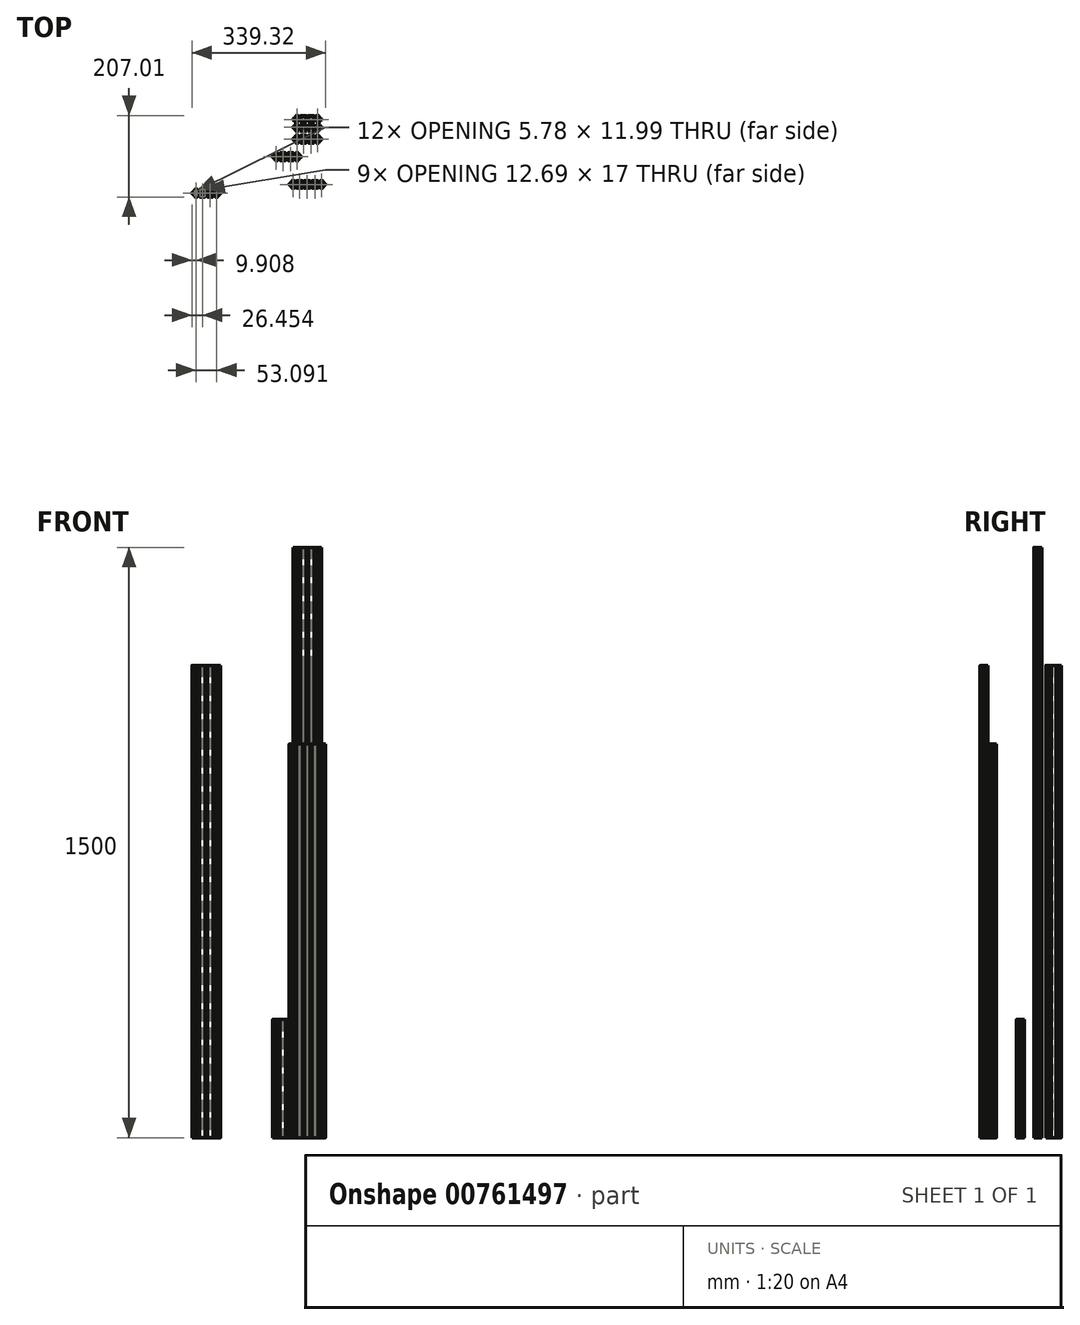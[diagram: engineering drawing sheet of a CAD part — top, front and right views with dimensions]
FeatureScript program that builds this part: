
annotation { "Feature Type Name" : "Feature", "Feature Type Description" : "" }
export const myFeature = defineFeature(function(context is Context, id is Id, definition is map)
    precondition{}
    {
        {
            var Q0;
            Q0=qCreatedBy(makeId("Top.planeOp"),FACE);
            var sketch = newSketch(context, id + "F0", { "sketchPlane" : qUnion([Q0])});
            skLineSegment(sketch, "E0", {"start": v(-3.65, 2.38) * mm, "end": v(-3.65, -2.38) * mm});
            skLineSegment(sketch, "E1", {"start": v(-17.88, 2.3) * mm, "end": v(-17.7, 2.12) * mm});
            skArc(sketch, "E2", {"start": v(-0.8, 1.94) * mm, "mid": v(-0.4, 2.06) * mm, "end": v(0, 2.1) * mm});
            skArc(sketch, "E3", {"start": v(-2.12, 2.3) * mm, "mid": v(-1.36, 2.5) * mm, "end": v(-0.8, 1.94) * mm});
            skLineSegment(sketch, "E4", {"start": v(-2.12, 2.3) * mm, "end": v(-2.3, 2.12) * mm});
            skArc(sketch, "E5", {"start": v(-1.94, 0.8) * mm, "mid": v(-2.5, 1.36) * mm, "end": v(-2.3, 2.12) * mm});
            skArc(sketch, "E6", {"start": v(-1.94, -0.8) * mm, "mid": v(-2.1, 0) * mm, "end": v(-1.94, 0.8) * mm});
            skArc(sketch, "E7", {"start": v(-2.3, -2.12) * mm, "mid": v(-2.5, -1.36) * mm, "end": v(-1.94, -0.8) * mm});
            skLineSegment(sketch, "E8", {"start": v(-2.3, -2.12) * mm, "end": v(-2.12, -2.3) * mm});
            skArc(sketch, "E9", {"start": v(-0.8, -1.94) * mm, "mid": v(-1.36, -2.5) * mm, "end": v(-2.12, -2.3) * mm});
            skArc(sketch, "E10", {"start": v(0, -2.1) * mm, "mid": v(-0.4, -2.06) * mm, "end": v(-0.8, -1.94) * mm});
            skArc(sketch, "E11", {"start": v(-17.88, 2.3) * mm, "mid": v(-18.64, 2.5) * mm, "end": v(-19.2, 1.94) * mm});
            skArc(sketch, "E12", {"start": v(-19.2, 1.94) * mm, "mid": v(-20, 2.1) * mm, "end": v(-20.8, 1.94) * mm});
            skArc(sketch, "E13", {"start": v(-20.8, 1.94) * mm, "mid": v(-21.36, 2.5) * mm, "end": v(-22.12, 2.3) * mm});
            skLineSegment(sketch, "E14", {"start": v(-22.3, 2.12) * mm, "end": v(-22.12, 2.3) * mm});
            skArc(sketch, "E15", {"start": v(-22.3, 2.12) * mm, "mid": v(-22.5, 1.36) * mm, "end": v(-21.94, 0.8) * mm});
            skArc(sketch, "E16", {"start": v(-21.94, 0.8) * mm, "mid": v(-22.1, 0) * mm, "end": v(-21.94, -0.8) * mm});
            skArc(sketch, "E17", {"start": v(-21.94, -0.8) * mm, "mid": v(-22.5, -1.36) * mm, "end": v(-22.3, -2.12) * mm});
            skLineSegment(sketch, "E18", {"start": v(-22.12, -2.3) * mm, "end": v(-22.3, -2.12) * mm});
            skArc(sketch, "E19", {"start": v(-22.12, -2.3) * mm, "mid": v(-21.36, -2.5) * mm, "end": v(-20.8, -1.94) * mm});
            skArc(sketch, "E20", {"start": v(-20.8, -1.94) * mm, "mid": v(-20, -2.1) * mm, "end": v(-19.2, -1.94) * mm});
            skArc(sketch, "E21", {"start": v(-19.2, -1.94) * mm, "mid": v(-18.64, -2.5) * mm, "end": v(-17.88, -2.3) * mm});
            skLineSegment(sketch, "E22", {"start": v(-17.7, -2.12) * mm, "end": v(-17.88, -2.3) * mm});
            skArc(sketch, "E23", {"start": v(-17.7, -2.12) * mm, "mid": v(-17.5, -1.36) * mm, "end": v(-18.06, -0.8) * mm});
            skArc(sketch, "E24", {"start": v(-18.06, -0.8) * mm, "mid": v(-17.9, 0) * mm, "end": v(-18.06, 0.8) * mm});
            skArc(sketch, "E25", {"start": v(-18.06, 0.8) * mm, "mid": v(-17.5, 1.36) * mm, "end": v(-17.7, 2.12) * mm});
            skLineSegment(sketch, "E26", {"start": v(0, -3.65) * mm, "end": v(-2.38, -3.65) * mm});
            skArc(sketch, "E27", {"start": v(-2.74, -3.8) * mm, "mid": v(-2.58, -3.7) * mm, "end": v(-2.38, -3.65) * mm});
            skLineSegment(sketch, "E28", {"start": v(-2.74, -3.8) * mm, "end": v(-5.85, -6.9) * mm});
            skArc(sketch, "E29", {"start": v(-6, -7.27) * mm, "mid": v(-5.96, -7.07) * mm, "end": v(-5.85, -6.9) * mm});
            skLineSegment(sketch, "E30", {"start": v(-6, -7.27) * mm, "end": v(-6, -8) * mm});
            skArc(sketch, "E31", {"start": v(-5.49, -8.5) * mm, "mid": v(-5.85, -8.35) * mm, "end": v(-6, -8) * mm});
            skLineSegment(sketch, "E32", {"start": v(-5.49, -8.5) * mm, "end": v(-3.14, -8.5) * mm});
            skArc(sketch, "E33", {"start": v(-3.14, -8.5) * mm, "mid": v(-2.78, -8.65) * mm, "end": v(-2.63, -9) * mm});
            skLineSegment(sketch, "E34", {"start": v(-2.63, -9.5) * mm, "end": v(-2.63, -9) * mm});
            skArc(sketch, "E35", {"start": v(-2.63, -9.5) * mm, "mid": v(-2.78, -9.85) * mm, "end": v(-3.14, -10) * mm});
            skLineSegment(sketch, "E36", {"start": v(-16.86, -10) * mm, "end": v(-3.14, -10) * mm});
            skArc(sketch, "E37", {"start": v(-17.37, -9.5) * mm, "mid": v(-17.22, -9.85) * mm, "end": v(-16.86, -10) * mm});
            skLineSegment(sketch, "E38", {"start": v(-17.37, -9.5) * mm, "end": v(-17.37, -9) * mm});
            skArc(sketch, "E39", {"start": v(-16.86, -8.5) * mm, "mid": v(-17.22, -8.65) * mm, "end": v(-17.37, -9) * mm});
            skLineSegment(sketch, "E40", {"start": v(-14.51, -8.5) * mm, "end": v(-16.86, -8.5) * mm});
            skArc(sketch, "E41", {"start": v(-14.51, -8.5) * mm, "mid": v(-14.15, -8.35) * mm, "end": v(-14, -8) * mm});
            skLineSegment(sketch, "E42", {"start": v(-14, -7.27) * mm, "end": v(-14, -8) * mm});
            skArc(sketch, "E43", {"start": v(-14, -7.27) * mm, "mid": v(-14.04, -7.07) * mm, "end": v(-14.15, -6.9) * mm});
            skLineSegment(sketch, "E44", {"start": v(-17.26, -3.8) * mm, "end": v(-14.15, -6.9) * mm});
            skArc(sketch, "E45", {"start": v(-17.26, -3.8) * mm, "mid": v(-17.42, -3.7) * mm, "end": v(-17.62, -3.65) * mm});
            skLineSegment(sketch, "E46", {"start": v(-22.38, -3.65) * mm, "end": v(-17.62, -3.65) * mm});
            skArc(sketch, "E47", {"start": v(-22.38, -3.65) * mm, "mid": v(-22.58, -3.7) * mm, "end": v(-22.74, -3.8) * mm});
            skLineSegment(sketch, "E48", {"start": v(-25.85, -6.9) * mm, "end": v(-22.74, -3.8) * mm});
            skArc(sketch, "E49", {"start": v(-25.85, -6.9) * mm, "mid": v(-25.96, -7.07) * mm, "end": v(-26, -7.27) * mm});
            skLineSegment(sketch, "E50", {"start": v(-26, -7.27) * mm, "end": v(-26, -8) * mm});
            skArc(sketch, "E51", {"start": v(-26, -8) * mm, "mid": v(-25.85, -8.35) * mm, "end": v(-25.49, -8.5) * mm});
            skLineSegment(sketch, "E52", {"start": v(-23.14, -8.5) * mm, "end": v(-25.49, -8.5) * mm});
            skArc(sketch, "E53", {"start": v(-22.63, -9) * mm, "mid": v(-22.78, -8.65) * mm, "end": v(-23.14, -8.5) * mm});
            skLineSegment(sketch, "E54", {"start": v(-22.63, -9) * mm, "end": v(-22.63, -9.5) * mm});
            skArc(sketch, "E55", {"start": v(-23.14, -10) * mm, "mid": v(-22.78, -9.85) * mm, "end": v(-22.63, -9.5) * mm});
            skLineSegment(sketch, "E56", {"start": v(-28.5, -10) * mm, "end": v(-23.14, -10) * mm});
            skArc(sketch, "E57", {"start": v(-30, -8.5) * mm, "mid": v(-29.56, -9.56) * mm, "end": v(-28.5, -10) * mm});
            skLineSegment(sketch, "E58", {"start": v(-30, -8.5) * mm, "end": v(-30, -3.14) * mm});
            skArc(sketch, "E59", {"start": v(-29.5, -2.63) * mm, "mid": v(-29.85, -2.78) * mm, "end": v(-30, -3.14) * mm});
            skLineSegment(sketch, "E60", {"start": v(-29.5, -2.63) * mm, "end": v(-29, -2.63) * mm});
            skArc(sketch, "E61", {"start": v(-28.5, -3.14) * mm, "mid": v(-28.65, -2.78) * mm, "end": v(-29, -2.63) * mm});
            skLineSegment(sketch, "E62", {"start": v(-28.5, -5.49) * mm, "end": v(-28.5, -3.14) * mm});
            skArc(sketch, "E63", {"start": v(-28.5, -5.49) * mm, "mid": v(-28.35, -5.85) * mm, "end": v(-28, -6) * mm});
            skLineSegment(sketch, "E64", {"start": v(-27.27, -6) * mm, "end": v(-28, -6) * mm});
            skArc(sketch, "E65", {"start": v(-27.27, -6) * mm, "mid": v(-27.07, -5.96) * mm, "end": v(-26.9, -5.85) * mm});
            skLineSegment(sketch, "E66", {"start": v(-23.8, -2.74) * mm, "end": v(-26.9, -5.85) * mm});
            skArc(sketch, "E67", {"start": v(-23.8, -2.74) * mm, "mid": v(-23.7, -2.58) * mm, "end": v(-23.66, -2.38) * mm});
            skLineSegment(sketch, "E68", {"start": v(-23.66, 2.38) * mm, "end": v(-23.66, -2.38) * mm});
            skArc(sketch, "E69", {"start": v(-23.66, 2.38) * mm, "mid": v(-23.7, 2.58) * mm, "end": v(-23.8, 2.74) * mm});
            skLineSegment(sketch, "E70", {"start": v(-23.8, 2.74) * mm, "end": v(-26.9, 5.85) * mm});
            skArc(sketch, "E71", {"start": v(-26.9, 5.85) * mm, "mid": v(-27.07, 5.96) * mm, "end": v(-27.27, 6) * mm});
            skLineSegment(sketch, "E72", {"start": v(-27.27, 6) * mm, "end": v(-28, 6) * mm});
            skArc(sketch, "E73", {"start": v(-28, 6) * mm, "mid": v(-28.35, 5.85) * mm, "end": v(-28.5, 5.49) * mm});
            skLineSegment(sketch, "E74", {"start": v(-28.5, 5.49) * mm, "end": v(-28.5, 3.14) * mm});
            skArc(sketch, "E75", {"start": v(-29, 2.63) * mm, "mid": v(-28.65, 2.78) * mm, "end": v(-28.5, 3.14) * mm});
            skLineSegment(sketch, "E76", {"start": v(-29, 2.63) * mm, "end": v(-29.5, 2.63) * mm});
            skArc(sketch, "E77", {"start": v(-30, 3.14) * mm, "mid": v(-29.85, 2.78) * mm, "end": v(-29.5, 2.63) * mm});
            skLineSegment(sketch, "E78", {"start": v(-30, 3.14) * mm, "end": v(-30, 8.5) * mm});
            skArc(sketch, "E79", {"start": v(-28.5, 10) * mm, "mid": v(-29.56, 9.56) * mm, "end": v(-30, 8.5) * mm});
            skLineSegment(sketch, "E80", {"start": v(-28.5, 10) * mm, "end": v(-23.14, 10) * mm});
            skArc(sketch, "E81", {"start": v(-22.63, 9.5) * mm, "mid": v(-22.78, 9.85) * mm, "end": v(-23.14, 10) * mm});
            skLineSegment(sketch, "E82", {"start": v(-22.63, 9.5) * mm, "end": v(-22.63, 9) * mm});
            skArc(sketch, "E83", {"start": v(-23.14, 8.5) * mm, "mid": v(-22.78, 8.65) * mm, "end": v(-22.63, 9) * mm});
            skLineSegment(sketch, "E84", {"start": v(-23.14, 8.5) * mm, "end": v(-25.49, 8.5) * mm});
            skArc(sketch, "E85", {"start": v(-25.49, 8.5) * mm, "mid": v(-25.85, 8.35) * mm, "end": v(-26, 8) * mm});
            skLineSegment(sketch, "E86", {"start": v(-26, 8) * mm, "end": v(-26, 7.27) * mm});
            skArc(sketch, "E87", {"start": v(-26, 7.27) * mm, "mid": v(-25.96, 7.07) * mm, "end": v(-25.85, 6.9) * mm});
            skLineSegment(sketch, "E88", {"start": v(-25.85, 6.9) * mm, "end": v(-22.74, 3.8) * mm});
            skArc(sketch, "E89", {"start": v(-22.74, 3.8) * mm, "mid": v(-22.58, 3.7) * mm, "end": v(-22.38, 3.65) * mm});
            skLineSegment(sketch, "E90", {"start": v(-22.38, 3.65) * mm, "end": v(-17.62, 3.65) * mm});
            skArc(sketch, "E91", {"start": v(-17.62, 3.65) * mm, "mid": v(-17.42, 3.7) * mm, "end": v(-17.26, 3.8) * mm});
            skLineSegment(sketch, "E92", {"start": v(-17.26, 3.8) * mm, "end": v(-14.15, 6.9) * mm});
            skArc(sketch, "E93", {"start": v(-14.15, 6.9) * mm, "mid": v(-14.04, 7.07) * mm, "end": v(-14, 7.27) * mm});
            skLineSegment(sketch, "E94", {"start": v(-14, 8) * mm, "end": v(-14, 7.27) * mm});
            skArc(sketch, "E95", {"start": v(-14, 8) * mm, "mid": v(-14.15, 8.35) * mm, "end": v(-14.51, 8.5) * mm});
            skLineSegment(sketch, "E96", {"start": v(-14.51, 8.5) * mm, "end": v(-16.86, 8.5) * mm});
            skArc(sketch, "E97", {"start": v(-17.37, 9) * mm, "mid": v(-17.22, 8.65) * mm, "end": v(-16.86, 8.5) * mm});
            skLineSegment(sketch, "E98", {"start": v(-17.37, 9) * mm, "end": v(-17.37, 9.5) * mm});
            skArc(sketch, "E99", {"start": v(-16.86, 10) * mm, "mid": v(-17.22, 9.85) * mm, "end": v(-17.37, 9.5) * mm});
            skLineSegment(sketch, "E100", {"start": v(-3.14, 10) * mm, "end": v(-16.86, 10) * mm});
            skArc(sketch, "E101", {"start": v(-3.14, 10) * mm, "mid": v(-2.78, 9.85) * mm, "end": v(-2.63, 9.5) * mm});
            skLineSegment(sketch, "E102", {"start": v(-2.63, 9) * mm, "end": v(-2.63, 9.5) * mm});
            skArc(sketch, "E103", {"start": v(-2.63, 9) * mm, "mid": v(-2.78, 8.65) * mm, "end": v(-3.14, 8.5) * mm});
            skLineSegment(sketch, "E104", {"start": v(-5.49, 8.5) * mm, "end": v(-3.14, 8.5) * mm});
            skArc(sketch, "E105", {"start": v(-6, 8) * mm, "mid": v(-5.85, 8.35) * mm, "end": v(-5.49, 8.5) * mm});
            skLineSegment(sketch, "E106", {"start": v(-6, 8) * mm, "end": v(-6, 7.27) * mm});
            skArc(sketch, "E107", {"start": v(-5.85, 6.9) * mm, "mid": v(-5.96, 7.07) * mm, "end": v(-6, 7.27) * mm});
            skLineSegment(sketch, "E108", {"start": v(-2.74, 3.8) * mm, "end": v(-5.85, 6.9) * mm});
            skArc(sketch, "E109", {"start": v(-2.38, 3.65) * mm, "mid": v(-2.58, 3.7) * mm, "end": v(-2.74, 3.8) * mm});
            skLineSegment(sketch, "E110", {"start": v(0, 3.65) * mm, "end": v(-2.38, 3.65) * mm});
            skArc(sketch, "E111", {"start": v(-3.65, 2.38) * mm, "mid": v(-3.7, 2.58) * mm, "end": v(-3.8, 2.74) * mm});
            skLineSegment(sketch, "E112", {"start": v(-3.8, 2.74) * mm, "end": v(-7.35, 6.29) * mm});
            skArc(sketch, "E113", {"start": v(-7.35, 6.29) * mm, "mid": v(-7.46, 6.45) * mm, "end": v(-7.5, 6.64) * mm});
            skLineSegment(sketch, "E114", {"start": v(-7.5, 8) * mm, "end": v(-7.5, 6.64) * mm});
            skArc(sketch, "E115", {"start": v(-8, 8.5) * mm, "mid": v(-7.64, 8.35) * mm, "end": v(-7.5, 8) * mm});
            skLineSegment(sketch, "E116", {"start": v(-12, 8.5) * mm, "end": v(-8, 8.5) * mm});
            skArc(sketch, "E117", {"start": v(-12, 8.5) * mm, "mid": v(-12.36, 8.35) * mm, "end": v(-12.5, 8) * mm});
            skLineSegment(sketch, "E118", {"start": v(-12.5, 8) * mm, "end": v(-12.5, 6.64) * mm});
            skArc(sketch, "E119", {"start": v(-12.65, 6.29) * mm, "mid": v(-12.54, 6.45) * mm, "end": v(-12.5, 6.64) * mm});
            skLineSegment(sketch, "E120", {"start": v(-16.2, 2.74) * mm, "end": v(-12.65, 6.29) * mm});
            skArc(sketch, "E121", {"start": v(-16.2, 2.74) * mm, "mid": v(-16.3, 2.58) * mm, "end": v(-16.35, 2.38) * mm});
            skLineSegment(sketch, "E122", {"start": v(-16.35, 2.38) * mm, "end": v(-16.35, -2.38) * mm});
            skArc(sketch, "E123", {"start": v(-16.35, -2.38) * mm, "mid": v(-16.3, -2.58) * mm, "end": v(-16.2, -2.74) * mm});
            skLineSegment(sketch, "E124", {"start": v(-16.2, -2.74) * mm, "end": v(-12.65, -6.29) * mm});
            skArc(sketch, "E125", {"start": v(-12.5, -6.64) * mm, "mid": v(-12.54, -6.45) * mm, "end": v(-12.65, -6.29) * mm});
            skLineSegment(sketch, "E126", {"start": v(-12.5, -6.64) * mm, "end": v(-12.5, -8) * mm});
            skArc(sketch, "E127", {"start": v(-12.5, -8) * mm, "mid": v(-12.36, -8.35) * mm, "end": v(-12, -8.5) * mm});
            skLineSegment(sketch, "E128", {"start": v(-12, -8.5) * mm, "end": v(-8, -8.5) * mm});
            skArc(sketch, "E129", {"start": v(-7.5, -8) * mm, "mid": v(-7.64, -8.35) * mm, "end": v(-8, -8.5) * mm});
            skLineSegment(sketch, "E130", {"start": v(-7.5, -6.64) * mm, "end": v(-7.5, -8) * mm});
            skArc(sketch, "E131", {"start": v(-7.5, -6.64) * mm, "mid": v(-7.46, -6.45) * mm, "end": v(-7.35, -6.29) * mm});
            skLineSegment(sketch, "E132", {"start": v(-3.8, -2.74) * mm, "end": v(-7.35, -6.29) * mm});
            skArc(sketch, "E133", {"start": v(-3.65, -2.38) * mm, "mid": v(-3.7, -2.58) * mm, "end": v(-3.8, -2.74) * mm});
            skLineSegment(sketch, "E134", {"start": v(3.65, 2.38) * mm, "end": v(3.65, -2.38) * mm});
            skLineSegment(sketch, "E135", {"start": v(17.88, 2.3) * mm, "end": v(17.7, 2.12) * mm});
            skArc(sketch, "E136", {"start": v(0.8, 1.94) * mm, "mid": v(1.36, 2.5) * mm, "end": v(2.12, 2.3) * mm});
            skLineSegment(sketch, "E137", {"start": v(2.12, 2.3) * mm, "end": v(2.3, 2.12) * mm});
            skArc(sketch, "E138", {"start": v(2.3, 2.12) * mm, "mid": v(2.5, 1.36) * mm, "end": v(1.94, 0.8) * mm});
            skArc(sketch, "E139", {"start": v(1.94, 0.8) * mm, "mid": v(2.1, 0) * mm, "end": v(1.94, -0.8) * mm});
            skArc(sketch, "E140", {"start": v(1.94, -0.8) * mm, "mid": v(2.5, -1.36) * mm, "end": v(2.3, -2.12) * mm});
            skLineSegment(sketch, "E141", {"start": v(2.3, -2.12) * mm, "end": v(2.12, -2.3) * mm});
            skArc(sketch, "E142", {"start": v(2.12, -2.3) * mm, "mid": v(1.36, -2.5) * mm, "end": v(0.8, -1.94) * mm});
            skArc(sketch, "E143", {"start": v(19.2, 1.94) * mm, "mid": v(18.64, 2.5) * mm, "end": v(17.88, 2.3) * mm});
            skArc(sketch, "E144", {"start": v(20.8, 1.94) * mm, "mid": v(20, 2.1) * mm, "end": v(19.2, 1.94) * mm});
            skArc(sketch, "E145", {"start": v(22.12, 2.3) * mm, "mid": v(21.36, 2.5) * mm, "end": v(20.8, 1.94) * mm});
            skLineSegment(sketch, "E146", {"start": v(22.3, 2.12) * mm, "end": v(22.12, 2.3) * mm});
            skArc(sketch, "E147", {"start": v(21.94, 0.8) * mm, "mid": v(22.5, 1.36) * mm, "end": v(22.3, 2.12) * mm});
            skArc(sketch, "E148", {"start": v(21.94, -0.8) * mm, "mid": v(22.1, 0) * mm, "end": v(21.94, 0.8) * mm});
            skArc(sketch, "E149", {"start": v(22.3, -2.12) * mm, "mid": v(22.5, -1.36) * mm, "end": v(21.94, -0.8) * mm});
            skLineSegment(sketch, "E150", {"start": v(22.12, -2.3) * mm, "end": v(22.3, -2.12) * mm});
            skArc(sketch, "E151", {"start": v(20.8, -1.94) * mm, "mid": v(21.36, -2.5) * mm, "end": v(22.12, -2.3) * mm});
            skArc(sketch, "E152", {"start": v(19.2, -1.94) * mm, "mid": v(20, -2.1) * mm, "end": v(20.8, -1.94) * mm});
            skArc(sketch, "E153", {"start": v(17.88, -2.3) * mm, "mid": v(18.64, -2.5) * mm, "end": v(19.2, -1.94) * mm});
            skLineSegment(sketch, "E154", {"start": v(17.7, -2.12) * mm, "end": v(17.88, -2.3) * mm});
            skArc(sketch, "E155", {"start": v(18.06, -0.8) * mm, "mid": v(17.5, -1.36) * mm, "end": v(17.7, -2.12) * mm});
            skArc(sketch, "E156", {"start": v(18.06, 0.8) * mm, "mid": v(17.9, 0) * mm, "end": v(18.06, -0.8) * mm});
            skArc(sketch, "E157", {"start": v(17.7, 2.12) * mm, "mid": v(17.5, 1.36) * mm, "end": v(18.06, 0.8) * mm});
            skLineSegment(sketch, "E158", {"start": v(0, -3.65) * mm, "end": v(2.38, -3.65) * mm});
            skArc(sketch, "E159", {"start": v(2.38, -3.65) * mm, "mid": v(2.58, -3.7) * mm, "end": v(2.74, -3.8) * mm});
            skLineSegment(sketch, "E160", {"start": v(2.74, -3.8) * mm, "end": v(5.85, -6.9) * mm});
            skArc(sketch, "E161", {"start": v(5.85, -6.9) * mm, "mid": v(5.96, -7.07) * mm, "end": v(6, -7.27) * mm});
            skLineSegment(sketch, "E162", {"start": v(6, -7.27) * mm, "end": v(6, -8) * mm});
            skArc(sketch, "E163", {"start": v(6, -8) * mm, "mid": v(5.85, -8.35) * mm, "end": v(5.49, -8.5) * mm});
            skLineSegment(sketch, "E164", {"start": v(5.49, -8.5) * mm, "end": v(3.14, -8.5) * mm});
            skArc(sketch, "E165", {"start": v(2.63, -9) * mm, "mid": v(2.78, -8.65) * mm, "end": v(3.14, -8.5) * mm});
            skLineSegment(sketch, "E166", {"start": v(2.63, -9.5) * mm, "end": v(2.63, -9) * mm});
            skArc(sketch, "E167", {"start": v(3.14, -10) * mm, "mid": v(2.78, -9.85) * mm, "end": v(2.63, -9.5) * mm});
            skLineSegment(sketch, "E168", {"start": v(16.86, -10) * mm, "end": v(3.14, -10) * mm});
            skArc(sketch, "E169", {"start": v(16.86, -10) * mm, "mid": v(17.22, -9.85) * mm, "end": v(17.37, -9.5) * mm});
            skLineSegment(sketch, "E170", {"start": v(17.37, -9.5) * mm, "end": v(17.37, -9) * mm});
            skArc(sketch, "E171", {"start": v(17.37, -9) * mm, "mid": v(17.22, -8.65) * mm, "end": v(16.86, -8.5) * mm});
            skLineSegment(sketch, "E172", {"start": v(14.51, -8.5) * mm, "end": v(16.86, -8.5) * mm});
            skArc(sketch, "E173", {"start": v(14, -8) * mm, "mid": v(14.15, -8.35) * mm, "end": v(14.51, -8.5) * mm});
            skLineSegment(sketch, "E174", {"start": v(14, -7.27) * mm, "end": v(14, -8) * mm});
            skArc(sketch, "E175", {"start": v(14.15, -6.9) * mm, "mid": v(14.04, -7.07) * mm, "end": v(14, -7.27) * mm});
            skLineSegment(sketch, "E176", {"start": v(17.26, -3.8) * mm, "end": v(14.15, -6.9) * mm});
            skArc(sketch, "E177", {"start": v(17.62, -3.65) * mm, "mid": v(17.42, -3.7) * mm, "end": v(17.26, -3.8) * mm});
            skLineSegment(sketch, "E178", {"start": v(22.38, -3.65) * mm, "end": v(17.62, -3.65) * mm});
            skArc(sketch, "E179", {"start": v(22.74, -3.8) * mm, "mid": v(22.58, -3.7) * mm, "end": v(22.38, -3.65) * mm});
            skLineSegment(sketch, "E180", {"start": v(25.85, -6.9) * mm, "end": v(22.74, -3.8) * mm});
            skArc(sketch, "E181", {"start": v(26, -7.27) * mm, "mid": v(25.96, -7.07) * mm, "end": v(25.85, -6.9) * mm});
            skLineSegment(sketch, "E182", {"start": v(26, -7.27) * mm, "end": v(26, -8) * mm});
            skArc(sketch, "E183", {"start": v(25.49, -8.5) * mm, "mid": v(25.85, -8.35) * mm, "end": v(26, -8) * mm});
            skLineSegment(sketch, "E184", {"start": v(23.14, -8.5) * mm, "end": v(25.49, -8.5) * mm});
            skArc(sketch, "E185", {"start": v(23.14, -8.5) * mm, "mid": v(22.78, -8.65) * mm, "end": v(22.63, -9) * mm});
            skLineSegment(sketch, "E186", {"start": v(22.63, -9) * mm, "end": v(22.63, -9.5) * mm});
            skArc(sketch, "E187", {"start": v(22.63, -9.5) * mm, "mid": v(22.78, -9.85) * mm, "end": v(23.14, -10) * mm});
            skLineSegment(sketch, "E188", {"start": v(28.5, -10) * mm, "end": v(23.14, -10) * mm});
            skArc(sketch, "E189", {"start": v(28.5, -10) * mm, "mid": v(29.56, -9.56) * mm, "end": v(30, -8.5) * mm});
            skLineSegment(sketch, "E190", {"start": v(30, -8.5) * mm, "end": v(30, -3.14) * mm});
            skArc(sketch, "E191", {"start": v(30, -3.14) * mm, "mid": v(29.85, -2.78) * mm, "end": v(29.5, -2.63) * mm});
            skLineSegment(sketch, "E192", {"start": v(29.5, -2.63) * mm, "end": v(29, -2.63) * mm});
            skArc(sketch, "E193", {"start": v(29, -2.63) * mm, "mid": v(28.65, -2.78) * mm, "end": v(28.5, -3.14) * mm});
            skLineSegment(sketch, "E194", {"start": v(28.5, -5.49) * mm, "end": v(28.5, -3.14) * mm});
            skArc(sketch, "E195", {"start": v(28, -6) * mm, "mid": v(28.35, -5.85) * mm, "end": v(28.5, -5.49) * mm});
            skLineSegment(sketch, "E196", {"start": v(27.27, -6) * mm, "end": v(28, -6) * mm});
            skArc(sketch, "E197", {"start": v(26.9, -5.85) * mm, "mid": v(27.07, -5.96) * mm, "end": v(27.27, -6) * mm});
            skLineSegment(sketch, "E198", {"start": v(23.8, -2.74) * mm, "end": v(26.9, -5.85) * mm});
            skArc(sketch, "E199", {"start": v(23.66, -2.38) * mm, "mid": v(23.7, -2.58) * mm, "end": v(23.8, -2.74) * mm});
            skLineSegment(sketch, "E200", {"start": v(23.66, 2.38) * mm, "end": v(23.66, -2.38) * mm});
            skArc(sketch, "E201", {"start": v(23.8, 2.74) * mm, "mid": v(23.7, 2.58) * mm, "end": v(23.66, 2.38) * mm});
            skLineSegment(sketch, "E202", {"start": v(23.8, 2.74) * mm, "end": v(26.9, 5.85) * mm});
            skArc(sketch, "E203", {"start": v(27.27, 6) * mm, "mid": v(27.07, 5.96) * mm, "end": v(26.9, 5.85) * mm});
            skLineSegment(sketch, "E204", {"start": v(27.27, 6) * mm, "end": v(28, 6) * mm});
            skArc(sketch, "E205", {"start": v(28.5, 5.49) * mm, "mid": v(28.35, 5.85) * mm, "end": v(28, 6) * mm});
            skLineSegment(sketch, "E206", {"start": v(28.5, 5.49) * mm, "end": v(28.5, 3.14) * mm});
            skArc(sketch, "E207", {"start": v(28.5, 3.14) * mm, "mid": v(28.65, 2.78) * mm, "end": v(29, 2.63) * mm});
            skLineSegment(sketch, "E208", {"start": v(29, 2.63) * mm, "end": v(29.5, 2.63) * mm});
            skArc(sketch, "E209", {"start": v(29.5, 2.63) * mm, "mid": v(29.85, 2.78) * mm, "end": v(30, 3.14) * mm});
            skLineSegment(sketch, "E210", {"start": v(30, 3.14) * mm, "end": v(30, 8.5) * mm});
            skArc(sketch, "E211", {"start": v(30, 8.5) * mm, "mid": v(29.56, 9.56) * mm, "end": v(28.5, 10) * mm});
            skLineSegment(sketch, "E212", {"start": v(28.5, 10) * mm, "end": v(23.14, 10) * mm});
            skArc(sketch, "E213", {"start": v(23.14, 10) * mm, "mid": v(22.78, 9.85) * mm, "end": v(22.63, 9.5) * mm});
            skLineSegment(sketch, "E214", {"start": v(22.63, 9.5) * mm, "end": v(22.63, 9) * mm});
            skArc(sketch, "E215", {"start": v(22.63, 9) * mm, "mid": v(22.78, 8.65) * mm, "end": v(23.14, 8.5) * mm});
            skLineSegment(sketch, "E216", {"start": v(23.14, 8.5) * mm, "end": v(25.49, 8.5) * mm});
            skArc(sketch, "E217", {"start": v(26, 8) * mm, "mid": v(25.85, 8.35) * mm, "end": v(25.49, 8.5) * mm});
            skLineSegment(sketch, "E218", {"start": v(26, 8) * mm, "end": v(26, 7.27) * mm});
            skArc(sketch, "E219", {"start": v(25.85, 6.9) * mm, "mid": v(25.96, 7.07) * mm, "end": v(26, 7.27) * mm});
            skLineSegment(sketch, "E220", {"start": v(25.85, 6.9) * mm, "end": v(22.74, 3.8) * mm});
            skArc(sketch, "E221", {"start": v(22.38, 3.65) * mm, "mid": v(22.58, 3.7) * mm, "end": v(22.74, 3.8) * mm});
            skLineSegment(sketch, "E222", {"start": v(22.38, 3.65) * mm, "end": v(17.62, 3.65) * mm});
            skArc(sketch, "E223", {"start": v(17.26, 3.8) * mm, "mid": v(17.42, 3.7) * mm, "end": v(17.62, 3.65) * mm});
            skLineSegment(sketch, "E224", {"start": v(17.26, 3.8) * mm, "end": v(14.15, 6.9) * mm});
            skArc(sketch, "E225", {"start": v(14, 7.27) * mm, "mid": v(14.04, 7.07) * mm, "end": v(14.15, 6.9) * mm});
            skLineSegment(sketch, "E226", {"start": v(14, 8) * mm, "end": v(14, 7.27) * mm});
            skArc(sketch, "E227", {"start": v(14.51, 8.5) * mm, "mid": v(14.15, 8.35) * mm, "end": v(14, 8) * mm});
            skLineSegment(sketch, "E228", {"start": v(14.51, 8.5) * mm, "end": v(16.86, 8.5) * mm});
            skArc(sketch, "E229", {"start": v(16.86, 8.5) * mm, "mid": v(17.22, 8.65) * mm, "end": v(17.37, 9) * mm});
            skLineSegment(sketch, "E230", {"start": v(17.37, 9) * mm, "end": v(17.37, 9.5) * mm});
            skArc(sketch, "E231", {"start": v(17.37, 9.5) * mm, "mid": v(17.22, 9.85) * mm, "end": v(16.86, 10) * mm});
            skLineSegment(sketch, "E232", {"start": v(3.14, 10) * mm, "end": v(16.86, 10) * mm});
            skArc(sketch, "E233", {"start": v(2.63, 9.5) * mm, "mid": v(2.78, 9.85) * mm, "end": v(3.14, 10) * mm});
            skLineSegment(sketch, "E234", {"start": v(2.63, 9) * mm, "end": v(2.63, 9.5) * mm});
            skArc(sketch, "E235", {"start": v(3.14, 8.5) * mm, "mid": v(2.78, 8.65) * mm, "end": v(2.63, 9) * mm});
            skLineSegment(sketch, "E236", {"start": v(5.49, 8.5) * mm, "end": v(3.14, 8.5) * mm});
            skArc(sketch, "E237", {"start": v(5.49, 8.5) * mm, "mid": v(5.85, 8.35) * mm, "end": v(6, 8) * mm});
            skLineSegment(sketch, "E238", {"start": v(6, 8) * mm, "end": v(6, 7.27) * mm});
            skArc(sketch, "E239", {"start": v(6, 7.27) * mm, "mid": v(5.96, 7.07) * mm, "end": v(5.85, 6.9) * mm});
            skLineSegment(sketch, "E240", {"start": v(2.74, 3.8) * mm, "end": v(5.85, 6.9) * mm});
            skArc(sketch, "E241", {"start": v(2.74, 3.8) * mm, "mid": v(2.58, 3.7) * mm, "end": v(2.38, 3.65) * mm});
            skLineSegment(sketch, "E242", {"start": v(0, 3.65) * mm, "end": v(2.38, 3.65) * mm});
            skArc(sketch, "E243", {"start": v(3.8, 2.74) * mm, "mid": v(3.7, 2.58) * mm, "end": v(3.65, 2.38) * mm});
            skLineSegment(sketch, "E244", {"start": v(3.8, 2.74) * mm, "end": v(7.35, 6.29) * mm});
            skArc(sketch, "E245", {"start": v(7.5, 6.64) * mm, "mid": v(7.46, 6.45) * mm, "end": v(7.35, 6.29) * mm});
            skLineSegment(sketch, "E246", {"start": v(7.5, 8) * mm, "end": v(7.5, 6.64) * mm});
            skArc(sketch, "E247", {"start": v(7.5, 8) * mm, "mid": v(7.64, 8.35) * mm, "end": v(8, 8.5) * mm});
            skLineSegment(sketch, "E248", {"start": v(12, 8.5) * mm, "end": v(8, 8.5) * mm});
            skArc(sketch, "E249", {"start": v(12.5, 8) * mm, "mid": v(12.36, 8.35) * mm, "end": v(12, 8.5) * mm});
            skLineSegment(sketch, "E250", {"start": v(12.5, 8) * mm, "end": v(12.5, 6.64) * mm});
            skArc(sketch, "E251", {"start": v(12.5, 6.64) * mm, "mid": v(12.54, 6.45) * mm, "end": v(12.65, 6.29) * mm});
            skLineSegment(sketch, "E252", {"start": v(16.2, 2.74) * mm, "end": v(12.65, 6.29) * mm});
            skArc(sketch, "E253", {"start": v(16.35, 2.38) * mm, "mid": v(16.3, 2.58) * mm, "end": v(16.2, 2.74) * mm});
            skLineSegment(sketch, "E254", {"start": v(16.35, 2.38) * mm, "end": v(16.35, -2.38) * mm});
            skArc(sketch, "E255", {"start": v(16.2, -2.74) * mm, "mid": v(16.3, -2.58) * mm, "end": v(16.35, -2.38) * mm});
            skLineSegment(sketch, "E256", {"start": v(16.2, -2.74) * mm, "end": v(12.65, -6.29) * mm});
            skArc(sketch, "E257", {"start": v(12.65, -6.29) * mm, "mid": v(12.54, -6.45) * mm, "end": v(12.5, -6.64) * mm});
            skLineSegment(sketch, "E258", {"start": v(12.5, -6.64) * mm, "end": v(12.5, -8) * mm});
            skArc(sketch, "E259", {"start": v(12, -8.5) * mm, "mid": v(12.36, -8.35) * mm, "end": v(12.5, -8) * mm});
            skLineSegment(sketch, "E260", {"start": v(12, -8.5) * mm, "end": v(8, -8.5) * mm});
            skArc(sketch, "E261", {"start": v(8, -8.5) * mm, "mid": v(7.64, -8.35) * mm, "end": v(7.5, -8) * mm});
            skLineSegment(sketch, "E262", {"start": v(7.5, -6.64) * mm, "end": v(7.5, -8) * mm});
            skArc(sketch, "E263", {"start": v(7.35, -6.29) * mm, "mid": v(7.46, -6.45) * mm, "end": v(7.5, -6.64) * mm});
            skLineSegment(sketch, "E264", {"start": v(3.8, -2.74) * mm, "end": v(7.35, -6.29) * mm});
            skArc(sketch, "E265", {"start": v(3.8, -2.74) * mm, "mid": v(3.7, -2.58) * mm, "end": v(3.65, -2.38) * mm});
            skArc(sketch, "E266", {"start": v(0, 2.1) * mm, "mid": v(0.4, 2.06) * mm, "end": v(0.8, 1.94) * mm});
            skArc(sketch, "E267", {"start": v(0.8, -1.94) * mm, "mid": v(0.4, -2.06) * mm, "end": v(0, -2.1) * mm});
            skCircle(sketch, "E268", {"center": v(-32.45, 0) * mm, "radius": 4 * mm});
            skCircle(sketch, "E269", {"center": v(32.45, 0) * mm, "radius": 4 * mm});
            skSolve(sketch);
        }
        {
            var Q0;
            Q0=qCreatedBy(makeId("Top.planeOp"),FACE);
            var sketch = newSketch(context, id + "F1", { "sketchPlane" : qUnion([Q0])});
            skLineSegment(sketch, "E270", {"start": v(-3.65, 52.38) * mm, "end": v(-3.65, 47.62) * mm});
            skLineSegment(sketch, "E271", {"start": v(-17.88, 52.3) * mm, "end": v(-17.7, 52.12) * mm});
            skArc(sketch, "E272", {"start": v(-0.8, 51.94) * mm, "mid": v(-0.4, 52.06) * mm, "end": v(0, 52.1) * mm});
            skArc(sketch, "E273", {"start": v(-2.12, 52.3) * mm, "mid": v(-1.36, 52.5) * mm, "end": v(-0.8, 51.94) * mm});
            skLineSegment(sketch, "E274", {"start": v(-2.12, 52.3) * mm, "end": v(-2.3, 52.12) * mm});
            skArc(sketch, "E275", {"start": v(-1.94, 50.8) * mm, "mid": v(-2.5, 51.36) * mm, "end": v(-2.3, 52.12) * mm});
            skArc(sketch, "E276", {"start": v(-1.94, 49.2) * mm, "mid": v(-2.1, 50) * mm, "end": v(-1.94, 50.8) * mm});
            skArc(sketch, "E277", {"start": v(-2.3, 47.88) * mm, "mid": v(-2.5, 48.64) * mm, "end": v(-1.94, 49.2) * mm});
            skLineSegment(sketch, "E278", {"start": v(-2.3, 47.88) * mm, "end": v(-2.12, 47.7) * mm});
            skArc(sketch, "E279", {"start": v(-0.8, 48.06) * mm, "mid": v(-1.36, 47.5) * mm, "end": v(-2.12, 47.7) * mm});
            skArc(sketch, "E280", {"start": v(0, 47.9) * mm, "mid": v(-0.4, 47.94) * mm, "end": v(-0.8, 48.06) * mm});
            skArc(sketch, "E281", {"start": v(-17.88, 52.3) * mm, "mid": v(-18.64, 52.5) * mm, "end": v(-19.2, 51.94) * mm});
            skArc(sketch, "E282", {"start": v(-19.2, 51.94) * mm, "mid": v(-20, 52.1) * mm, "end": v(-20.8, 51.94) * mm});
            skArc(sketch, "E283", {"start": v(-20.8, 51.94) * mm, "mid": v(-21.36, 52.5) * mm, "end": v(-22.12, 52.3) * mm});
            skLineSegment(sketch, "E284", {"start": v(-22.3, 52.12) * mm, "end": v(-22.12, 52.3) * mm});
            skArc(sketch, "E285", {"start": v(-22.3, 52.12) * mm, "mid": v(-22.5, 51.36) * mm, "end": v(-21.94, 50.8) * mm});
            skArc(sketch, "E286", {"start": v(-21.94, 50.8) * mm, "mid": v(-22.1, 50) * mm, "end": v(-21.94, 49.2) * mm});
            skArc(sketch, "E287", {"start": v(-21.94, 49.2) * mm, "mid": v(-22.5, 48.64) * mm, "end": v(-22.3, 47.88) * mm});
            skLineSegment(sketch, "E288", {"start": v(-22.12, 47.7) * mm, "end": v(-22.3, 47.88) * mm});
            skArc(sketch, "E289", {"start": v(-22.12, 47.7) * mm, "mid": v(-21.36, 47.5) * mm, "end": v(-20.8, 48.06) * mm});
            skArc(sketch, "E290", {"start": v(-20.8, 48.06) * mm, "mid": v(-20, 47.9) * mm, "end": v(-19.2, 48.06) * mm});
            skArc(sketch, "E291", {"start": v(-19.2, 48.06) * mm, "mid": v(-18.64, 47.5) * mm, "end": v(-17.88, 47.7) * mm});
            skLineSegment(sketch, "E292", {"start": v(-17.7, 47.88) * mm, "end": v(-17.88, 47.7) * mm});
            skArc(sketch, "E293", {"start": v(-17.7, 47.88) * mm, "mid": v(-17.5, 48.64) * mm, "end": v(-18.06, 49.2) * mm});
            skArc(sketch, "E294", {"start": v(-18.06, 49.2) * mm, "mid": v(-17.9, 50) * mm, "end": v(-18.06, 50.8) * mm});
            skArc(sketch, "E295", {"start": v(-18.06, 50.8) * mm, "mid": v(-17.5, 51.36) * mm, "end": v(-17.7, 52.12) * mm});
            skLineSegment(sketch, "E296", {"start": v(0, 46.35) * mm, "end": v(-2.38, 46.35) * mm});
            skArc(sketch, "E297", {"start": v(-2.74, 46.2) * mm, "mid": v(-2.58, 46.3) * mm, "end": v(-2.38, 46.35) * mm});
            skLineSegment(sketch, "E298", {"start": v(-2.74, 46.2) * mm, "end": v(-5.85, 43.1) * mm});
            skLineSegment(sketch, "E299", {"start": v(-17.26, 46.2) * mm, "end": v(-14.15, 43.1) * mm});
            skArc(sketch, "E300", {"start": v(-17.26, 46.2) * mm, "mid": v(-17.42, 46.3) * mm, "end": v(-17.62, 46.35) * mm});
            skLineSegment(sketch, "E301", {"start": v(-22.38, 46.35) * mm, "end": v(-17.62, 46.35) * mm});
            skArc(sketch, "E302", {"start": v(-22.38, 46.35) * mm, "mid": v(-22.58, 46.3) * mm, "end": v(-22.74, 46.2) * mm});
            skLineSegment(sketch, "E303", {"start": v(-25.85, 43.1) * mm, "end": v(-22.74, 46.2) * mm});
            skLineSegment(sketch, "E304", {"start": v(-30, 38.5) * mm, "end": v(-30, 46.86) * mm});
            skArc(sketch, "E305", {"start": v(-29.5, 47.37) * mm, "mid": v(-29.85, 47.22) * mm, "end": v(-30, 46.86) * mm});
            skLineSegment(sketch, "E306", {"start": v(-29.5, 47.37) * mm, "end": v(-29, 47.37) * mm});
            skArc(sketch, "E307", {"start": v(-28.5, 46.86) * mm, "mid": v(-28.65, 47.22) * mm, "end": v(-29, 47.37) * mm});
            skLineSegment(sketch, "E308", {"start": v(-28.5, 44.51) * mm, "end": v(-28.5, 46.86) * mm});
            skArc(sketch, "E309", {"start": v(-28.5, 44.51) * mm, "mid": v(-28.35, 44.15) * mm, "end": v(-28, 44) * mm});
            skLineSegment(sketch, "E310", {"start": v(-27.27, 44) * mm, "end": v(-28, 44) * mm});
            skArc(sketch, "E311", {"start": v(-27.27, 44) * mm, "mid": v(-27.07, 44.04) * mm, "end": v(-26.9, 44.15) * mm});
            skLineSegment(sketch, "E312", {"start": v(-23.8, 47.26) * mm, "end": v(-26.9, 44.15) * mm});
            skArc(sketch, "E313", {"start": v(-23.8, 47.26) * mm, "mid": v(-23.7, 47.42) * mm, "end": v(-23.65, 47.62) * mm});
            skLineSegment(sketch, "E314", {"start": v(-23.65, 52.38) * mm, "end": v(-23.65, 47.62) * mm});
            skArc(sketch, "E315", {"start": v(-23.65, 52.38) * mm, "mid": v(-23.7, 52.58) * mm, "end": v(-23.8, 52.74) * mm});
            skLineSegment(sketch, "E316", {"start": v(-23.8, 52.74) * mm, "end": v(-26.9, 55.85) * mm});
            skArc(sketch, "E317", {"start": v(-26.9, 55.85) * mm, "mid": v(-27.07, 55.96) * mm, "end": v(-27.27, 56) * mm});
            skLineSegment(sketch, "E318", {"start": v(-27.27, 56) * mm, "end": v(-28, 56) * mm});
            skArc(sketch, "E319", {"start": v(-28, 56) * mm, "mid": v(-28.35, 55.85) * mm, "end": v(-28.5, 55.49) * mm});
            skLineSegment(sketch, "E320", {"start": v(-28.5, 55.49) * mm, "end": v(-28.5, 53.14) * mm});
            skArc(sketch, "E321", {"start": v(-29, 52.63) * mm, "mid": v(-28.65, 52.78) * mm, "end": v(-28.5, 53.14) * mm});
            skLineSegment(sketch, "E322", {"start": v(-29, 52.63) * mm, "end": v(-29.5, 52.63) * mm});
            skArc(sketch, "E323", {"start": v(-30, 53.14) * mm, "mid": v(-29.85, 52.78) * mm, "end": v(-29.5, 52.63) * mm});
            skLineSegment(sketch, "E324", {"start": v(-30, 53.14) * mm, "end": v(-30, 58.5) * mm});
            skArc(sketch, "E325", {"start": v(-28.5, 60) * mm, "mid": v(-29.56, 59.56) * mm, "end": v(-30, 58.5) * mm});
            skLineSegment(sketch, "E326", {"start": v(-28.5, 60) * mm, "end": v(-23.14, 60) * mm});
            skArc(sketch, "E327", {"start": v(-22.63, 59.5) * mm, "mid": v(-22.78, 59.85) * mm, "end": v(-23.14, 60) * mm});
            skLineSegment(sketch, "E328", {"start": v(-22.63, 59.5) * mm, "end": v(-22.63, 59) * mm});
            skArc(sketch, "E329", {"start": v(-23.14, 58.5) * mm, "mid": v(-22.78, 58.65) * mm, "end": v(-22.63, 59) * mm});
            skLineSegment(sketch, "E330", {"start": v(-23.14, 58.5) * mm, "end": v(-25.49, 58.5) * mm});
            skArc(sketch, "E331", {"start": v(-25.49, 58.5) * mm, "mid": v(-25.85, 58.35) * mm, "end": v(-26, 58) * mm});
            skLineSegment(sketch, "E332", {"start": v(-26, 58) * mm, "end": v(-26, 57.27) * mm});
            skArc(sketch, "E333", {"start": v(-26, 57.27) * mm, "mid": v(-25.96, 57.07) * mm, "end": v(-25.85, 56.9) * mm});
            skLineSegment(sketch, "E334", {"start": v(-25.85, 56.9) * mm, "end": v(-22.74, 53.8) * mm});
            skArc(sketch, "E335", {"start": v(-22.74, 53.8) * mm, "mid": v(-22.58, 53.7) * mm, "end": v(-22.38, 53.66) * mm});
            skLineSegment(sketch, "E336", {"start": v(-22.38, 53.66) * mm, "end": v(-17.62, 53.66) * mm});
            skArc(sketch, "E337", {"start": v(-17.62, 53.66) * mm, "mid": v(-17.42, 53.7) * mm, "end": v(-17.26, 53.8) * mm});
            skLineSegment(sketch, "E338", {"start": v(-17.26, 53.8) * mm, "end": v(-14.15, 56.9) * mm});
            skArc(sketch, "E339", {"start": v(-14.15, 56.9) * mm, "mid": v(-14.04, 57.07) * mm, "end": v(-14, 57.27) * mm});
            skLineSegment(sketch, "E340", {"start": v(-14, 58) * mm, "end": v(-14, 57.27) * mm});
            skArc(sketch, "E341", {"start": v(-14, 58) * mm, "mid": v(-14.15, 58.35) * mm, "end": v(-14.51, 58.5) * mm});
            skLineSegment(sketch, "E342", {"start": v(-14.51, 58.5) * mm, "end": v(-16.86, 58.5) * mm});
            skArc(sketch, "E343", {"start": v(-17.37, 59) * mm, "mid": v(-17.22, 58.65) * mm, "end": v(-16.86, 58.5) * mm});
            skLineSegment(sketch, "E344", {"start": v(-17.37, 59) * mm, "end": v(-17.37, 59.5) * mm});
            skArc(sketch, "E345", {"start": v(-16.86, 60) * mm, "mid": v(-17.22, 59.85) * mm, "end": v(-17.37, 59.5) * mm});
            skLineSegment(sketch, "E346", {"start": v(-3.14, 60) * mm, "end": v(-16.86, 60) * mm});
            skArc(sketch, "E347", {"start": v(-3.14, 60) * mm, "mid": v(-2.78, 59.85) * mm, "end": v(-2.63, 59.5) * mm});
            skLineSegment(sketch, "E348", {"start": v(-2.63, 59) * mm, "end": v(-2.63, 59.5) * mm});
            skArc(sketch, "E349", {"start": v(-2.63, 59) * mm, "mid": v(-2.78, 58.65) * mm, "end": v(-3.14, 58.5) * mm});
            skLineSegment(sketch, "E350", {"start": v(-5.49, 58.5) * mm, "end": v(-3.14, 58.5) * mm});
            skArc(sketch, "E351", {"start": v(-6, 58) * mm, "mid": v(-5.85, 58.35) * mm, "end": v(-5.49, 58.5) * mm});
            skLineSegment(sketch, "E352", {"start": v(-6, 58) * mm, "end": v(-6, 57.27) * mm});
            skArc(sketch, "E353", {"start": v(-5.85, 56.9) * mm, "mid": v(-5.96, 57.07) * mm, "end": v(-6, 57.27) * mm});
            skLineSegment(sketch, "E354", {"start": v(-2.74, 53.8) * mm, "end": v(-5.85, 56.9) * mm});
            skArc(sketch, "E355", {"start": v(-2.38, 53.66) * mm, "mid": v(-2.58, 53.7) * mm, "end": v(-2.74, 53.8) * mm});
            skLineSegment(sketch, "E356", {"start": v(0, 53.66) * mm, "end": v(-2.38, 53.66) * mm});
            skArc(sketch, "E357", {"start": v(-3.65, 52.38) * mm, "mid": v(-3.7, 52.58) * mm, "end": v(-3.8, 52.74) * mm});
            skLineSegment(sketch, "E358", {"start": v(-3.8, 52.74) * mm, "end": v(-7.35, 56.29) * mm});
            skArc(sketch, "E359", {"start": v(-7.35, 56.29) * mm, "mid": v(-7.46, 56.45) * mm, "end": v(-7.5, 56.64) * mm});
            skLineSegment(sketch, "E360", {"start": v(-7.5, 58) * mm, "end": v(-7.5, 56.64) * mm});
            skArc(sketch, "E361", {"start": v(-8, 58.5) * mm, "mid": v(-7.64, 58.35) * mm, "end": v(-7.5, 58) * mm});
            skLineSegment(sketch, "E362", {"start": v(-12, 58.5) * mm, "end": v(-8, 58.5) * mm});
            skArc(sketch, "E363", {"start": v(-12, 58.5) * mm, "mid": v(-12.36, 58.35) * mm, "end": v(-12.5, 58) * mm});
            skLineSegment(sketch, "E364", {"start": v(-12.5, 58) * mm, "end": v(-12.5, 56.64) * mm});
            skArc(sketch, "E365", {"start": v(-12.65, 56.29) * mm, "mid": v(-12.54, 56.45) * mm, "end": v(-12.5, 56.64) * mm});
            skLineSegment(sketch, "E366", {"start": v(-16.2, 52.74) * mm, "end": v(-12.65, 56.29) * mm});
            skArc(sketch, "E367", {"start": v(-16.2, 52.74) * mm, "mid": v(-16.3, 52.58) * mm, "end": v(-16.35, 52.38) * mm});
            skLineSegment(sketch, "E368", {"start": v(-16.35, 52.38) * mm, "end": v(-16.35, 47.62) * mm});
            skArc(sketch, "E369", {"start": v(-16.35, 47.62) * mm, "mid": v(-16.3, 47.42) * mm, "end": v(-16.2, 47.26) * mm});
            skLineSegment(sketch, "E370", {"start": v(-16.2, 47.26) * mm, "end": v(-12.65, 43.71) * mm});
            skLineSegment(sketch, "E371", {"start": v(-3.8, 47.26) * mm, "end": v(-7.35, 43.71) * mm});
            skArc(sketch, "E372", {"start": v(-3.65, 47.62) * mm, "mid": v(-3.7, 47.42) * mm, "end": v(-3.8, 47.26) * mm});
            skLineSegment(sketch, "E373", {"start": v(3.65, 52.38) * mm, "end": v(3.65, 47.62) * mm});
            skLineSegment(sketch, "E374", {"start": v(17.88, 52.3) * mm, "end": v(17.7, 52.12) * mm});
            skArc(sketch, "E375", {"start": v(0.8, 51.94) * mm, "mid": v(1.36, 52.5) * mm, "end": v(2.12, 52.3) * mm});
            skLineSegment(sketch, "E376", {"start": v(2.12, 52.3) * mm, "end": v(2.3, 52.12) * mm});
            skArc(sketch, "E377", {"start": v(2.3, 52.12) * mm, "mid": v(2.5, 51.36) * mm, "end": v(1.94, 50.8) * mm});
            skArc(sketch, "E378", {"start": v(1.94, 50.8) * mm, "mid": v(2.1, 50) * mm, "end": v(1.94, 49.2) * mm});
            skArc(sketch, "E379", {"start": v(1.94, 49.2) * mm, "mid": v(2.5, 48.64) * mm, "end": v(2.3, 47.88) * mm});
            skLineSegment(sketch, "E380", {"start": v(2.3, 47.88) * mm, "end": v(2.12, 47.7) * mm});
            skArc(sketch, "E381", {"start": v(2.12, 47.7) * mm, "mid": v(1.36, 47.5) * mm, "end": v(0.8, 48.06) * mm});
            skArc(sketch, "E382", {"start": v(19.2, 51.94) * mm, "mid": v(18.64, 52.5) * mm, "end": v(17.88, 52.3) * mm});
            skArc(sketch, "E383", {"start": v(20.8, 51.94) * mm, "mid": v(20, 52.1) * mm, "end": v(19.2, 51.94) * mm});
            skArc(sketch, "E384", {"start": v(22.12, 52.3) * mm, "mid": v(21.36, 52.5) * mm, "end": v(20.8, 51.94) * mm});
            skLineSegment(sketch, "E385", {"start": v(22.3, 52.12) * mm, "end": v(22.12, 52.3) * mm});
            skArc(sketch, "E386", {"start": v(21.94, 50.8) * mm, "mid": v(22.5, 51.36) * mm, "end": v(22.3, 52.12) * mm});
            skArc(sketch, "E387", {"start": v(21.94, 49.2) * mm, "mid": v(22.1, 50) * mm, "end": v(21.94, 50.8) * mm});
            skArc(sketch, "E388", {"start": v(22.3, 47.88) * mm, "mid": v(22.5, 48.64) * mm, "end": v(21.94, 49.2) * mm});
            skLineSegment(sketch, "E389", {"start": v(22.12, 47.7) * mm, "end": v(22.3, 47.88) * mm});
            skArc(sketch, "E390", {"start": v(20.8, 48.06) * mm, "mid": v(21.36, 47.5) * mm, "end": v(22.12, 47.7) * mm});
            skArc(sketch, "E391", {"start": v(19.2, 48.06) * mm, "mid": v(20, 47.9) * mm, "end": v(20.8, 48.06) * mm});
            skArc(sketch, "E392", {"start": v(17.88, 47.7) * mm, "mid": v(18.64, 47.5) * mm, "end": v(19.2, 48.06) * mm});
            skLineSegment(sketch, "E393", {"start": v(17.7, 47.88) * mm, "end": v(17.88, 47.7) * mm});
            skArc(sketch, "E394", {"start": v(18.06, 49.2) * mm, "mid": v(17.5, 48.64) * mm, "end": v(17.7, 47.88) * mm});
            skArc(sketch, "E395", {"start": v(18.06, 50.8) * mm, "mid": v(17.9, 50) * mm, "end": v(18.06, 49.2) * mm});
            skArc(sketch, "E396", {"start": v(17.7, 52.12) * mm, "mid": v(17.5, 51.36) * mm, "end": v(18.06, 50.8) * mm});
            skLineSegment(sketch, "E397", {"start": v(0, 46.35) * mm, "end": v(2.38, 46.35) * mm});
            skArc(sketch, "E398", {"start": v(2.38, 46.35) * mm, "mid": v(2.58, 46.3) * mm, "end": v(2.74, 46.2) * mm});
            skLineSegment(sketch, "E399", {"start": v(2.74, 46.2) * mm, "end": v(5.85, 43.1) * mm});
            skLineSegment(sketch, "E400", {"start": v(17.26, 46.2) * mm, "end": v(14.15, 43.1) * mm});
            skArc(sketch, "E401", {"start": v(17.62, 46.35) * mm, "mid": v(17.42, 46.3) * mm, "end": v(17.26, 46.2) * mm});
            skLineSegment(sketch, "E402", {"start": v(22.38, 46.35) * mm, "end": v(17.62, 46.35) * mm});
            skArc(sketch, "E403", {"start": v(22.74, 46.2) * mm, "mid": v(22.58, 46.3) * mm, "end": v(22.38, 46.35) * mm});
            skLineSegment(sketch, "E404", {"start": v(25.85, 43.1) * mm, "end": v(22.74, 46.2) * mm});
            skLineSegment(sketch, "E405", {"start": v(30, 38.5) * mm, "end": v(30, 46.86) * mm});
            skArc(sketch, "E406", {"start": v(30, 46.86) * mm, "mid": v(29.85, 47.22) * mm, "end": v(29.5, 47.37) * mm});
            skLineSegment(sketch, "E407", {"start": v(29.5, 47.37) * mm, "end": v(29, 47.37) * mm});
            skArc(sketch, "E408", {"start": v(29, 47.37) * mm, "mid": v(28.65, 47.22) * mm, "end": v(28.5, 46.86) * mm});
            skLineSegment(sketch, "E409", {"start": v(28.5, 44.51) * mm, "end": v(28.5, 46.86) * mm});
            skArc(sketch, "E410", {"start": v(28, 44) * mm, "mid": v(28.35, 44.15) * mm, "end": v(28.5, 44.51) * mm});
            skLineSegment(sketch, "E411", {"start": v(27.27, 44) * mm, "end": v(28, 44) * mm});
            skArc(sketch, "E412", {"start": v(26.9, 44.15) * mm, "mid": v(27.07, 44.04) * mm, "end": v(27.27, 44) * mm});
            skLineSegment(sketch, "E413", {"start": v(23.8, 47.26) * mm, "end": v(26.9, 44.15) * mm});
            skArc(sketch, "E414", {"start": v(23.65, 47.62) * mm, "mid": v(23.7, 47.42) * mm, "end": v(23.8, 47.26) * mm});
            skLineSegment(sketch, "E415", {"start": v(23.65, 52.38) * mm, "end": v(23.65, 47.62) * mm});
            skArc(sketch, "E416", {"start": v(23.8, 52.74) * mm, "mid": v(23.7, 52.58) * mm, "end": v(23.65, 52.38) * mm});
            skLineSegment(sketch, "E417", {"start": v(23.8, 52.74) * mm, "end": v(26.9, 55.85) * mm});
            skArc(sketch, "E418", {"start": v(27.27, 56) * mm, "mid": v(27.07, 55.96) * mm, "end": v(26.9, 55.85) * mm});
            skLineSegment(sketch, "E419", {"start": v(27.27, 56) * mm, "end": v(28, 56) * mm});
            skArc(sketch, "E420", {"start": v(28.5, 55.49) * mm, "mid": v(28.35, 55.85) * mm, "end": v(28, 56) * mm});
            skLineSegment(sketch, "E421", {"start": v(28.5, 55.49) * mm, "end": v(28.5, 53.14) * mm});
            skArc(sketch, "E422", {"start": v(28.5, 53.14) * mm, "mid": v(28.65, 52.78) * mm, "end": v(29, 52.63) * mm});
            skLineSegment(sketch, "E423", {"start": v(29, 52.63) * mm, "end": v(29.5, 52.63) * mm});
            skArc(sketch, "E424", {"start": v(29.5, 52.63) * mm, "mid": v(29.85, 52.78) * mm, "end": v(30, 53.14) * mm});
            skLineSegment(sketch, "E425", {"start": v(30, 53.14) * mm, "end": v(30, 58.5) * mm});
            skArc(sketch, "E426", {"start": v(30, 58.5) * mm, "mid": v(29.56, 59.56) * mm, "end": v(28.5, 60) * mm});
            skLineSegment(sketch, "E427", {"start": v(28.5, 60) * mm, "end": v(23.14, 60) * mm});
            skArc(sketch, "E428", {"start": v(23.14, 60) * mm, "mid": v(22.78, 59.85) * mm, "end": v(22.63, 59.5) * mm});
            skLineSegment(sketch, "E429", {"start": v(22.63, 59.5) * mm, "end": v(22.63, 59) * mm});
            skArc(sketch, "E430", {"start": v(22.63, 59) * mm, "mid": v(22.78, 58.65) * mm, "end": v(23.14, 58.5) * mm});
            skLineSegment(sketch, "E431", {"start": v(23.14, 58.5) * mm, "end": v(25.49, 58.5) * mm});
            skArc(sketch, "E432", {"start": v(26, 58) * mm, "mid": v(25.85, 58.35) * mm, "end": v(25.49, 58.5) * mm});
            skLineSegment(sketch, "E433", {"start": v(26, 58) * mm, "end": v(26, 57.27) * mm});
            skArc(sketch, "E434", {"start": v(25.85, 56.9) * mm, "mid": v(25.96, 57.07) * mm, "end": v(26, 57.27) * mm});
            skLineSegment(sketch, "E435", {"start": v(25.85, 56.9) * mm, "end": v(22.74, 53.8) * mm});
            skArc(sketch, "E436", {"start": v(22.38, 53.66) * mm, "mid": v(22.58, 53.7) * mm, "end": v(22.74, 53.8) * mm});
            skLineSegment(sketch, "E437", {"start": v(22.38, 53.66) * mm, "end": v(17.62, 53.66) * mm});
            skArc(sketch, "E438", {"start": v(17.26, 53.8) * mm, "mid": v(17.42, 53.7) * mm, "end": v(17.62, 53.66) * mm});
            skLineSegment(sketch, "E439", {"start": v(17.26, 53.8) * mm, "end": v(14.15, 56.9) * mm});
            skArc(sketch, "E440", {"start": v(14, 57.27) * mm, "mid": v(14.04, 57.07) * mm, "end": v(14.15, 56.9) * mm});
            skLineSegment(sketch, "E441", {"start": v(14, 58) * mm, "end": v(14, 57.27) * mm});
            skArc(sketch, "E442", {"start": v(14.51, 58.5) * mm, "mid": v(14.15, 58.35) * mm, "end": v(14, 58) * mm});
            skLineSegment(sketch, "E443", {"start": v(14.51, 58.5) * mm, "end": v(16.86, 58.5) * mm});
            skArc(sketch, "E444", {"start": v(16.86, 58.5) * mm, "mid": v(17.22, 58.65) * mm, "end": v(17.37, 59) * mm});
            skLineSegment(sketch, "E445", {"start": v(17.37, 59) * mm, "end": v(17.37, 59.5) * mm});
            skArc(sketch, "E446", {"start": v(17.37, 59.5) * mm, "mid": v(17.22, 59.85) * mm, "end": v(16.86, 60) * mm});
            skLineSegment(sketch, "E447", {"start": v(3.14, 60) * mm, "end": v(16.86, 60) * mm});
            skArc(sketch, "E448", {"start": v(2.63, 59.5) * mm, "mid": v(2.78, 59.85) * mm, "end": v(3.14, 60) * mm});
            skLineSegment(sketch, "E449", {"start": v(2.63, 59) * mm, "end": v(2.63, 59.5) * mm});
            skArc(sketch, "E450", {"start": v(3.14, 58.5) * mm, "mid": v(2.78, 58.65) * mm, "end": v(2.63, 59) * mm});
            skLineSegment(sketch, "E451", {"start": v(5.49, 58.5) * mm, "end": v(3.14, 58.5) * mm});
            skArc(sketch, "E452", {"start": v(5.49, 58.5) * mm, "mid": v(5.85, 58.35) * mm, "end": v(6, 58) * mm});
            skLineSegment(sketch, "E453", {"start": v(6, 58) * mm, "end": v(6, 57.27) * mm});
            skArc(sketch, "E454", {"start": v(6, 57.27) * mm, "mid": v(5.96, 57.07) * mm, "end": v(5.85, 56.9) * mm});
            skLineSegment(sketch, "E455", {"start": v(2.74, 53.8) * mm, "end": v(5.85, 56.9) * mm});
            skArc(sketch, "E456", {"start": v(2.74, 53.8) * mm, "mid": v(2.58, 53.7) * mm, "end": v(2.38, 53.66) * mm});
            skLineSegment(sketch, "E457", {"start": v(0, 53.66) * mm, "end": v(2.38, 53.66) * mm});
            skArc(sketch, "E458", {"start": v(3.8, 52.74) * mm, "mid": v(3.7, 52.58) * mm, "end": v(3.65, 52.38) * mm});
            skLineSegment(sketch, "E459", {"start": v(3.8, 52.74) * mm, "end": v(7.35, 56.29) * mm});
            skArc(sketch, "E460", {"start": v(7.5, 56.64) * mm, "mid": v(7.46, 56.45) * mm, "end": v(7.35, 56.29) * mm});
            skLineSegment(sketch, "E461", {"start": v(7.5, 58) * mm, "end": v(7.5, 56.64) * mm});
            skArc(sketch, "E462", {"start": v(7.5, 58) * mm, "mid": v(7.64, 58.35) * mm, "end": v(8, 58.5) * mm});
            skLineSegment(sketch, "E463", {"start": v(12, 58.5) * mm, "end": v(8, 58.5) * mm});
            skArc(sketch, "E464", {"start": v(12.5, 58) * mm, "mid": v(12.36, 58.35) * mm, "end": v(12, 58.5) * mm});
            skLineSegment(sketch, "E465", {"start": v(12.5, 58) * mm, "end": v(12.5, 56.64) * mm});
            skArc(sketch, "E466", {"start": v(12.5, 56.64) * mm, "mid": v(12.54, 56.45) * mm, "end": v(12.65, 56.29) * mm});
            skLineSegment(sketch, "E467", {"start": v(16.2, 52.74) * mm, "end": v(12.65, 56.29) * mm});
            skArc(sketch, "E468", {"start": v(16.35, 52.38) * mm, "mid": v(16.3, 52.58) * mm, "end": v(16.2, 52.74) * mm});
            skLineSegment(sketch, "E469", {"start": v(16.35, 52.38) * mm, "end": v(16.35, 47.62) * mm});
            skArc(sketch, "E470", {"start": v(16.2, 47.26) * mm, "mid": v(16.3, 47.42) * mm, "end": v(16.35, 47.62) * mm});
            skLineSegment(sketch, "E471", {"start": v(16.2, 47.26) * mm, "end": v(12.65, 43.71) * mm});
            skLineSegment(sketch, "E472", {"start": v(3.8, 47.26) * mm, "end": v(7.35, 43.71) * mm});
            skArc(sketch, "E473", {"start": v(3.8, 47.26) * mm, "mid": v(3.7, 47.42) * mm, "end": v(3.65, 47.62) * mm});
            skArc(sketch, "E474", {"start": v(0, 52.1) * mm, "mid": v(0.4, 52.06) * mm, "end": v(0.8, 51.94) * mm});
            skArc(sketch, "E475", {"start": v(0.8, 48.06) * mm, "mid": v(0.4, 47.94) * mm, "end": v(0, 47.9) * mm});
            skCircle(sketch, "E476", {"center": v(-32.45, 50) * mm, "radius": 4 * mm});
            skCircle(sketch, "E477", {"center": v(32.45, 50) * mm, "radius": 4 * mm});
            skLineSegment(sketch, "E478", {"start": v(-3.65, 27.62) * mm, "end": v(-3.65, 32.38) * mm});
            skLineSegment(sketch, "E479", {"start": v(-17.88, 27.7) * mm, "end": v(-17.7, 27.88) * mm});
            skArc(sketch, "E480", {"start": v(0, 27.9) * mm, "mid": v(-0.4, 27.94) * mm, "end": v(-0.8, 28.06) * mm});
            skArc(sketch, "E481", {"start": v(-0.8, 28.06) * mm, "mid": v(-1.36, 27.5) * mm, "end": v(-2.12, 27.7) * mm});
            skLineSegment(sketch, "E482", {"start": v(-2.12, 27.7) * mm, "end": v(-2.3, 27.88) * mm});
            skArc(sketch, "E483", {"start": v(-2.3, 27.88) * mm, "mid": v(-2.5, 28.64) * mm, "end": v(-1.94, 29.2) * mm});
            skArc(sketch, "E484", {"start": v(-1.94, 29.2) * mm, "mid": v(-2.1, 30) * mm, "end": v(-1.94, 30.8) * mm});
            skArc(sketch, "E485", {"start": v(-1.94, 30.8) * mm, "mid": v(-2.5, 31.36) * mm, "end": v(-2.3, 32.12) * mm});
            skLineSegment(sketch, "E486", {"start": v(-2.3, 32.12) * mm, "end": v(-2.12, 32.3) * mm});
            skArc(sketch, "E487", {"start": v(-2.12, 32.3) * mm, "mid": v(-1.36, 32.5) * mm, "end": v(-0.8, 31.94) * mm});
            skArc(sketch, "E488", {"start": v(-0.8, 31.94) * mm, "mid": v(-0.4, 32.06) * mm, "end": v(0, 32.1) * mm});
            skArc(sketch, "E489", {"start": v(-19.2, 28.06) * mm, "mid": v(-18.64, 27.5) * mm, "end": v(-17.88, 27.7) * mm});
            skArc(sketch, "E490", {"start": v(-20.8, 28.06) * mm, "mid": v(-20, 27.9) * mm, "end": v(-19.2, 28.06) * mm});
            skArc(sketch, "E491", {"start": v(-22.12, 27.7) * mm, "mid": v(-21.36, 27.5) * mm, "end": v(-20.8, 28.06) * mm});
            skLineSegment(sketch, "E492", {"start": v(-22.3, 27.88) * mm, "end": v(-22.12, 27.7) * mm});
            skArc(sketch, "E493", {"start": v(-21.94, 29.2) * mm, "mid": v(-22.5, 28.64) * mm, "end": v(-22.3, 27.88) * mm});
            skArc(sketch, "E494", {"start": v(-21.94, 30.8) * mm, "mid": v(-22.1, 30) * mm, "end": v(-21.94, 29.2) * mm});
            skArc(sketch, "E495", {"start": v(-22.3, 32.12) * mm, "mid": v(-22.5, 31.36) * mm, "end": v(-21.94, 30.8) * mm});
            skLineSegment(sketch, "E496", {"start": v(-22.12, 32.3) * mm, "end": v(-22.3, 32.12) * mm});
            skArc(sketch, "E497", {"start": v(-20.8, 31.94) * mm, "mid": v(-21.36, 32.5) * mm, "end": v(-22.12, 32.3) * mm});
            skArc(sketch, "E498", {"start": v(-19.2, 31.94) * mm, "mid": v(-20, 32.1) * mm, "end": v(-20.8, 31.94) * mm});
            skArc(sketch, "E499", {"start": v(-17.88, 32.3) * mm, "mid": v(-18.64, 32.5) * mm, "end": v(-19.2, 31.94) * mm});
            skLineSegment(sketch, "E500", {"start": v(-17.7, 32.12) * mm, "end": v(-17.88, 32.3) * mm});
            skArc(sketch, "E501", {"start": v(-18.06, 30.8) * mm, "mid": v(-17.5, 31.36) * mm, "end": v(-17.7, 32.12) * mm});
            skArc(sketch, "E502", {"start": v(-18.06, 29.2) * mm, "mid": v(-17.9, 30) * mm, "end": v(-18.06, 30.8) * mm});
            skArc(sketch, "E503", {"start": v(-17.7, 27.88) * mm, "mid": v(-17.5, 28.64) * mm, "end": v(-18.06, 29.2) * mm});
            skLineSegment(sketch, "E504", {"start": v(0, 33.66) * mm, "end": v(-2.38, 33.66) * mm});
            skArc(sketch, "E505", {"start": v(-2.38, 33.66) * mm, "mid": v(-2.58, 33.7) * mm, "end": v(-2.74, 33.8) * mm});
            skLineSegment(sketch, "E506", {"start": v(-2.74, 33.8) * mm, "end": v(-5.85, 36.9) * mm});
            skLineSegment(sketch, "E507", {"start": v(-17.26, 33.8) * mm, "end": v(-14.15, 36.9) * mm});
            skArc(sketch, "E508", {"start": v(-17.62, 33.66) * mm, "mid": v(-17.42, 33.7) * mm, "end": v(-17.26, 33.8) * mm});
            skLineSegment(sketch, "E509", {"start": v(-22.38, 33.66) * mm, "end": v(-17.62, 33.66) * mm});
            skArc(sketch, "E510", {"start": v(-22.74, 33.8) * mm, "mid": v(-22.58, 33.7) * mm, "end": v(-22.38, 33.66) * mm});
            skLineSegment(sketch, "E511", {"start": v(-25.85, 36.9) * mm, "end": v(-22.74, 33.8) * mm});
            skLineSegment(sketch, "E512", {"start": v(-30, 38.5) * mm, "end": v(-30, 33.14) * mm});
            skArc(sketch, "E513", {"start": v(-30, 33.14) * mm, "mid": v(-29.85, 32.78) * mm, "end": v(-29.5, 32.63) * mm});
            skLineSegment(sketch, "E514", {"start": v(-29.5, 32.63) * mm, "end": v(-29, 32.63) * mm});
            skArc(sketch, "E515", {"start": v(-29, 32.63) * mm, "mid": v(-28.65, 32.78) * mm, "end": v(-28.5, 33.14) * mm});
            skLineSegment(sketch, "E516", {"start": v(-28.5, 35.49) * mm, "end": v(-28.5, 33.14) * mm});
            skArc(sketch, "E517", {"start": v(-28, 36) * mm, "mid": v(-28.35, 35.85) * mm, "end": v(-28.5, 35.49) * mm});
            skLineSegment(sketch, "E518", {"start": v(-27.27, 36) * mm, "end": v(-28, 36) * mm});
            skArc(sketch, "E519", {"start": v(-26.9, 35.85) * mm, "mid": v(-27.07, 35.96) * mm, "end": v(-27.27, 36) * mm});
            skLineSegment(sketch, "E520", {"start": v(-23.8, 32.74) * mm, "end": v(-26.9, 35.85) * mm});
            skArc(sketch, "E521", {"start": v(-23.65, 32.38) * mm, "mid": v(-23.7, 32.58) * mm, "end": v(-23.8, 32.74) * mm});
            skLineSegment(sketch, "E522", {"start": v(-23.65, 27.62) * mm, "end": v(-23.65, 32.38) * mm});
            skArc(sketch, "E523", {"start": v(-23.8, 27.26) * mm, "mid": v(-23.7, 27.42) * mm, "end": v(-23.65, 27.62) * mm});
            skLineSegment(sketch, "E524", {"start": v(-23.8, 27.26) * mm, "end": v(-26.9, 24.15) * mm});
            skArc(sketch, "E525", {"start": v(-27.27, 24) * mm, "mid": v(-27.07, 24.04) * mm, "end": v(-26.9, 24.15) * mm});
            skLineSegment(sketch, "E526", {"start": v(-27.27, 24) * mm, "end": v(-28, 24) * mm});
            skArc(sketch, "E527", {"start": v(-28.5, 24.51) * mm, "mid": v(-28.35, 24.15) * mm, "end": v(-28, 24) * mm});
            skLineSegment(sketch, "E528", {"start": v(-28.5, 24.51) * mm, "end": v(-28.5, 26.86) * mm});
            skArc(sketch, "E529", {"start": v(-28.5, 26.86) * mm, "mid": v(-28.65, 27.22) * mm, "end": v(-29, 27.37) * mm});
            skLineSegment(sketch, "E530", {"start": v(-29, 27.37) * mm, "end": v(-29.5, 27.37) * mm});
            skArc(sketch, "E531", {"start": v(-29.5, 27.37) * mm, "mid": v(-29.85, 27.22) * mm, "end": v(-30, 26.86) * mm});
            skLineSegment(sketch, "E532", {"start": v(-30, 26.86) * mm, "end": v(-30, 21.5) * mm});
            skArc(sketch, "E533", {"start": v(-30, 21.5) * mm, "mid": v(-29.56, 20.44) * mm, "end": v(-28.5, 20) * mm});
            skLineSegment(sketch, "E534", {"start": v(-28.5, 20) * mm, "end": v(-23.14, 20) * mm});
            skArc(sketch, "E535", {"start": v(-23.14, 20) * mm, "mid": v(-22.78, 20.15) * mm, "end": v(-22.63, 20.5) * mm});
            skLineSegment(sketch, "E536", {"start": v(-22.63, 20.5) * mm, "end": v(-22.63, 21) * mm});
            skArc(sketch, "E537", {"start": v(-22.63, 21) * mm, "mid": v(-22.78, 21.35) * mm, "end": v(-23.14, 21.5) * mm});
            skLineSegment(sketch, "E538", {"start": v(-23.14, 21.5) * mm, "end": v(-25.49, 21.5) * mm});
            skArc(sketch, "E539", {"start": v(-26, 22) * mm, "mid": v(-25.85, 21.65) * mm, "end": v(-25.49, 21.5) * mm});
            skLineSegment(sketch, "E540", {"start": v(-26, 22) * mm, "end": v(-26, 22.73) * mm});
            skArc(sketch, "E541", {"start": v(-25.85, 23.1) * mm, "mid": v(-25.96, 22.93) * mm, "end": v(-26, 22.73) * mm});
            skLineSegment(sketch, "E542", {"start": v(-25.85, 23.1) * mm, "end": v(-22.74, 26.2) * mm});
            skArc(sketch, "E543", {"start": v(-22.38, 26.35) * mm, "mid": v(-22.58, 26.3) * mm, "end": v(-22.74, 26.2) * mm});
            skLineSegment(sketch, "E544", {"start": v(-22.38, 26.35) * mm, "end": v(-17.62, 26.35) * mm});
            skArc(sketch, "E545", {"start": v(-17.26, 26.2) * mm, "mid": v(-17.42, 26.3) * mm, "end": v(-17.62, 26.35) * mm});
            skLineSegment(sketch, "E546", {"start": v(-17.26, 26.2) * mm, "end": v(-14.15, 23.1) * mm});
            skArc(sketch, "E547", {"start": v(-14, 22.73) * mm, "mid": v(-14.04, 22.93) * mm, "end": v(-14.15, 23.1) * mm});
            skLineSegment(sketch, "E548", {"start": v(-14, 22) * mm, "end": v(-14, 22.73) * mm});
            skArc(sketch, "E549", {"start": v(-14.51, 21.5) * mm, "mid": v(-14.15, 21.65) * mm, "end": v(-14, 22) * mm});
            skLineSegment(sketch, "E550", {"start": v(-14.51, 21.5) * mm, "end": v(-16.86, 21.5) * mm});
            skArc(sketch, "E551", {"start": v(-16.86, 21.5) * mm, "mid": v(-17.22, 21.35) * mm, "end": v(-17.37, 21) * mm});
            skLineSegment(sketch, "E552", {"start": v(-17.37, 21) * mm, "end": v(-17.37, 20.5) * mm});
            skArc(sketch, "E553", {"start": v(-17.37, 20.5) * mm, "mid": v(-17.22, 20.15) * mm, "end": v(-16.86, 20) * mm});
            skLineSegment(sketch, "E554", {"start": v(-3.14, 20) * mm, "end": v(-16.86, 20) * mm});
            skArc(sketch, "E555", {"start": v(-2.63, 20.5) * mm, "mid": v(-2.78, 20.15) * mm, "end": v(-3.14, 20) * mm});
            skLineSegment(sketch, "E556", {"start": v(-2.63, 21) * mm, "end": v(-2.63, 20.5) * mm});
            skArc(sketch, "E557", {"start": v(-3.14, 21.5) * mm, "mid": v(-2.78, 21.35) * mm, "end": v(-2.63, 21) * mm});
            skLineSegment(sketch, "E558", {"start": v(-5.49, 21.5) * mm, "end": v(-3.14, 21.5) * mm});
            skArc(sketch, "E559", {"start": v(-5.49, 21.5) * mm, "mid": v(-5.85, 21.65) * mm, "end": v(-6, 22) * mm});
            skLineSegment(sketch, "E560", {"start": v(-6, 22) * mm, "end": v(-6, 22.73) * mm});
            skArc(sketch, "E561", {"start": v(-6, 22.73) * mm, "mid": v(-5.96, 22.93) * mm, "end": v(-5.85, 23.1) * mm});
            skLineSegment(sketch, "E562", {"start": v(-2.74, 26.2) * mm, "end": v(-5.85, 23.1) * mm});
            skArc(sketch, "E563", {"start": v(-2.74, 26.2) * mm, "mid": v(-2.58, 26.3) * mm, "end": v(-2.38, 26.35) * mm});
            skLineSegment(sketch, "E564", {"start": v(0, 26.35) * mm, "end": v(-2.38, 26.35) * mm});
            skArc(sketch, "E565", {"start": v(-3.8, 27.26) * mm, "mid": v(-3.7, 27.42) * mm, "end": v(-3.65, 27.62) * mm});
            skLineSegment(sketch, "E566", {"start": v(-3.8, 27.26) * mm, "end": v(-7.35, 23.71) * mm});
            skArc(sketch, "E567", {"start": v(-7.5, 23.36) * mm, "mid": v(-7.46, 23.55) * mm, "end": v(-7.35, 23.71) * mm});
            skLineSegment(sketch, "E568", {"start": v(-7.5, 22) * mm, "end": v(-7.5, 23.36) * mm});
            skArc(sketch, "E569", {"start": v(-7.5, 22) * mm, "mid": v(-7.64, 21.65) * mm, "end": v(-8, 21.5) * mm});
            skLineSegment(sketch, "E570", {"start": v(-12, 21.5) * mm, "end": v(-8, 21.5) * mm});
            skArc(sketch, "E571", {"start": v(-12.5, 22) * mm, "mid": v(-12.36, 21.65) * mm, "end": v(-12, 21.5) * mm});
            skLineSegment(sketch, "E572", {"start": v(-12.5, 22) * mm, "end": v(-12.5, 23.36) * mm});
            skArc(sketch, "E573", {"start": v(-12.5, 23.36) * mm, "mid": v(-12.54, 23.55) * mm, "end": v(-12.65, 23.71) * mm});
            skLineSegment(sketch, "E574", {"start": v(-16.2, 27.26) * mm, "end": v(-12.65, 23.71) * mm});
            skArc(sketch, "E575", {"start": v(-16.35, 27.62) * mm, "mid": v(-16.3, 27.42) * mm, "end": v(-16.2, 27.26) * mm});
            skLineSegment(sketch, "E576", {"start": v(-16.35, 27.62) * mm, "end": v(-16.35, 32.38) * mm});
            skArc(sketch, "E577", {"start": v(-16.2, 32.74) * mm, "mid": v(-16.3, 32.58) * mm, "end": v(-16.35, 32.38) * mm});
            skLineSegment(sketch, "E578", {"start": v(-16.2, 32.74) * mm, "end": v(-12.65, 36.29) * mm});
            skLineSegment(sketch, "E579", {"start": v(-3.8, 32.74) * mm, "end": v(-7.35, 36.29) * mm});
            skArc(sketch, "E580", {"start": v(-3.8, 32.74) * mm, "mid": v(-3.7, 32.58) * mm, "end": v(-3.65, 32.38) * mm});
            skLineSegment(sketch, "E581", {"start": v(3.65, 27.62) * mm, "end": v(3.65, 32.38) * mm});
            skLineSegment(sketch, "E582", {"start": v(17.88, 27.7) * mm, "end": v(17.7, 27.88) * mm});
            skArc(sketch, "E583", {"start": v(2.12, 27.7) * mm, "mid": v(1.36, 27.5) * mm, "end": v(0.8, 28.06) * mm});
            skLineSegment(sketch, "E584", {"start": v(2.12, 27.7) * mm, "end": v(2.3, 27.88) * mm});
            skArc(sketch, "E585", {"start": v(1.94, 29.2) * mm, "mid": v(2.5, 28.64) * mm, "end": v(2.3, 27.88) * mm});
            skArc(sketch, "E586", {"start": v(1.94, 30.8) * mm, "mid": v(2.1, 30) * mm, "end": v(1.94, 29.2) * mm});
            skArc(sketch, "E587", {"start": v(2.3, 32.12) * mm, "mid": v(2.5, 31.36) * mm, "end": v(1.94, 30.8) * mm});
            skLineSegment(sketch, "E588", {"start": v(2.3, 32.12) * mm, "end": v(2.12, 32.3) * mm});
            skArc(sketch, "E589", {"start": v(0.8, 31.94) * mm, "mid": v(1.36, 32.5) * mm, "end": v(2.12, 32.3) * mm});
            skArc(sketch, "E590", {"start": v(17.88, 27.7) * mm, "mid": v(18.64, 27.5) * mm, "end": v(19.2, 28.06) * mm});
            skArc(sketch, "E591", {"start": v(19.2, 28.06) * mm, "mid": v(20, 27.9) * mm, "end": v(20.8, 28.06) * mm});
            skArc(sketch, "E592", {"start": v(20.8, 28.06) * mm, "mid": v(21.36, 27.5) * mm, "end": v(22.12, 27.7) * mm});
            skLineSegment(sketch, "E593", {"start": v(22.3, 27.88) * mm, "end": v(22.12, 27.7) * mm});
            skArc(sketch, "E594", {"start": v(22.3, 27.88) * mm, "mid": v(22.5, 28.64) * mm, "end": v(21.94, 29.2) * mm});
            skArc(sketch, "E595", {"start": v(21.94, 29.2) * mm, "mid": v(22.1, 30) * mm, "end": v(21.94, 30.8) * mm});
            skArc(sketch, "E596", {"start": v(21.94, 30.8) * mm, "mid": v(22.5, 31.36) * mm, "end": v(22.3, 32.12) * mm});
            skLineSegment(sketch, "E597", {"start": v(22.12, 32.3) * mm, "end": v(22.3, 32.12) * mm});
            skArc(sketch, "E598", {"start": v(22.12, 32.3) * mm, "mid": v(21.36, 32.5) * mm, "end": v(20.8, 31.94) * mm});
            skArc(sketch, "E599", {"start": v(20.8, 31.94) * mm, "mid": v(20, 32.1) * mm, "end": v(19.2, 31.94) * mm});
            skArc(sketch, "E600", {"start": v(19.2, 31.94) * mm, "mid": v(18.64, 32.5) * mm, "end": v(17.88, 32.3) * mm});
            skLineSegment(sketch, "E601", {"start": v(17.7, 32.12) * mm, "end": v(17.88, 32.3) * mm});
            skArc(sketch, "E602", {"start": v(17.7, 32.12) * mm, "mid": v(17.5, 31.36) * mm, "end": v(18.06, 30.8) * mm});
            skArc(sketch, "E603", {"start": v(18.06, 30.8) * mm, "mid": v(17.9, 30) * mm, "end": v(18.06, 29.2) * mm});
            skArc(sketch, "E604", {"start": v(18.06, 29.2) * mm, "mid": v(17.5, 28.64) * mm, "end": v(17.7, 27.88) * mm});
            skLineSegment(sketch, "E605", {"start": v(0, 33.66) * mm, "end": v(2.38, 33.66) * mm});
            skArc(sketch, "E606", {"start": v(2.74, 33.8) * mm, "mid": v(2.58, 33.7) * mm, "end": v(2.38, 33.66) * mm});
            skLineSegment(sketch, "E607", {"start": v(2.74, 33.8) * mm, "end": v(5.85, 36.9) * mm});
            skLineSegment(sketch, "E608", {"start": v(17.26, 33.8) * mm, "end": v(14.15, 36.9) * mm});
            skArc(sketch, "E609", {"start": v(17.26, 33.8) * mm, "mid": v(17.42, 33.7) * mm, "end": v(17.62, 33.66) * mm});
            skLineSegment(sketch, "E610", {"start": v(22.38, 33.66) * mm, "end": v(17.62, 33.66) * mm});
            skArc(sketch, "E611", {"start": v(22.38, 33.66) * mm, "mid": v(22.58, 33.7) * mm, "end": v(22.74, 33.8) * mm});
            skLineSegment(sketch, "E612", {"start": v(25.85, 36.9) * mm, "end": v(22.74, 33.8) * mm});
            skLineSegment(sketch, "E613", {"start": v(30, 38.5) * mm, "end": v(30, 33.14) * mm});
            skArc(sketch, "E614", {"start": v(29.5, 32.63) * mm, "mid": v(29.85, 32.78) * mm, "end": v(30, 33.14) * mm});
            skLineSegment(sketch, "E615", {"start": v(29.5, 32.63) * mm, "end": v(29, 32.63) * mm});
            skArc(sketch, "E616", {"start": v(28.5, 33.14) * mm, "mid": v(28.65, 32.78) * mm, "end": v(29, 32.63) * mm});
            skLineSegment(sketch, "E617", {"start": v(28.5, 35.49) * mm, "end": v(28.5, 33.14) * mm});
            skArc(sketch, "E618", {"start": v(28.5, 35.49) * mm, "mid": v(28.35, 35.85) * mm, "end": v(28, 36) * mm});
            skLineSegment(sketch, "E619", {"start": v(27.27, 36) * mm, "end": v(28, 36) * mm});
            skArc(sketch, "E620", {"start": v(27.27, 36) * mm, "mid": v(27.07, 35.96) * mm, "end": v(26.9, 35.85) * mm});
            skLineSegment(sketch, "E621", {"start": v(23.8, 32.74) * mm, "end": v(26.9, 35.85) * mm});
            skArc(sketch, "E622", {"start": v(23.8, 32.74) * mm, "mid": v(23.7, 32.58) * mm, "end": v(23.65, 32.38) * mm});
            skLineSegment(sketch, "E623", {"start": v(23.65, 27.62) * mm, "end": v(23.65, 32.38) * mm});
            skArc(sketch, "E624", {"start": v(23.65, 27.62) * mm, "mid": v(23.7, 27.42) * mm, "end": v(23.8, 27.26) * mm});
            skLineSegment(sketch, "E625", {"start": v(23.8, 27.26) * mm, "end": v(26.9, 24.15) * mm});
            skArc(sketch, "E626", {"start": v(26.9, 24.15) * mm, "mid": v(27.07, 24.04) * mm, "end": v(27.27, 24) * mm});
            skLineSegment(sketch, "E627", {"start": v(27.27, 24) * mm, "end": v(28, 24) * mm});
            skArc(sketch, "E628", {"start": v(28, 24) * mm, "mid": v(28.35, 24.15) * mm, "end": v(28.5, 24.51) * mm});
            skLineSegment(sketch, "E629", {"start": v(28.5, 24.51) * mm, "end": v(28.5, 26.86) * mm});
            skArc(sketch, "E630", {"start": v(29, 27.37) * mm, "mid": v(28.65, 27.22) * mm, "end": v(28.5, 26.86) * mm});
            skLineSegment(sketch, "E631", {"start": v(29, 27.37) * mm, "end": v(29.5, 27.37) * mm});
            skArc(sketch, "E632", {"start": v(30, 26.86) * mm, "mid": v(29.85, 27.22) * mm, "end": v(29.5, 27.37) * mm});
            skLineSegment(sketch, "E633", {"start": v(30, 26.86) * mm, "end": v(30, 21.5) * mm});
            skArc(sketch, "E634", {"start": v(28.5, 20) * mm, "mid": v(29.56, 20.44) * mm, "end": v(30, 21.5) * mm});
            skLineSegment(sketch, "E635", {"start": v(28.5, 20) * mm, "end": v(23.14, 20) * mm});
            skArc(sketch, "E636", {"start": v(22.63, 20.5) * mm, "mid": v(22.78, 20.15) * mm, "end": v(23.14, 20) * mm});
            skLineSegment(sketch, "E637", {"start": v(22.63, 20.5) * mm, "end": v(22.63, 21) * mm});
            skArc(sketch, "E638", {"start": v(23.14, 21.5) * mm, "mid": v(22.78, 21.35) * mm, "end": v(22.63, 21) * mm});
            skLineSegment(sketch, "E639", {"start": v(23.14, 21.5) * mm, "end": v(25.49, 21.5) * mm});
            skArc(sketch, "E640", {"start": v(25.49, 21.5) * mm, "mid": v(25.85, 21.65) * mm, "end": v(26, 22) * mm});
            skLineSegment(sketch, "E641", {"start": v(26, 22) * mm, "end": v(26, 22.73) * mm});
            skArc(sketch, "E642", {"start": v(26, 22.73) * mm, "mid": v(25.96, 22.93) * mm, "end": v(25.85, 23.1) * mm});
            skLineSegment(sketch, "E643", {"start": v(25.85, 23.1) * mm, "end": v(22.74, 26.2) * mm});
            skArc(sketch, "E644", {"start": v(22.74, 26.2) * mm, "mid": v(22.58, 26.3) * mm, "end": v(22.38, 26.35) * mm});
            skLineSegment(sketch, "E645", {"start": v(22.38, 26.35) * mm, "end": v(17.62, 26.35) * mm});
            skArc(sketch, "E646", {"start": v(17.62, 26.35) * mm, "mid": v(17.42, 26.3) * mm, "end": v(17.26, 26.2) * mm});
            skLineSegment(sketch, "E647", {"start": v(17.26, 26.2) * mm, "end": v(14.15, 23.1) * mm});
            skArc(sketch, "E648", {"start": v(14.15, 23.1) * mm, "mid": v(14.04, 22.93) * mm, "end": v(14, 22.73) * mm});
            skLineSegment(sketch, "E649", {"start": v(14, 22) * mm, "end": v(14, 22.73) * mm});
            skArc(sketch, "E650", {"start": v(14, 22) * mm, "mid": v(14.15, 21.65) * mm, "end": v(14.51, 21.5) * mm});
            skLineSegment(sketch, "E651", {"start": v(14.51, 21.5) * mm, "end": v(16.86, 21.5) * mm});
            skArc(sketch, "E652", {"start": v(17.37, 21) * mm, "mid": v(17.22, 21.35) * mm, "end": v(16.86, 21.5) * mm});
            skLineSegment(sketch, "E653", {"start": v(17.37, 21) * mm, "end": v(17.37, 20.5) * mm});
            skArc(sketch, "E654", {"start": v(16.86, 20) * mm, "mid": v(17.22, 20.15) * mm, "end": v(17.37, 20.5) * mm});
            skLineSegment(sketch, "E655", {"start": v(3.14, 20) * mm, "end": v(16.86, 20) * mm});
            skArc(sketch, "E656", {"start": v(3.14, 20) * mm, "mid": v(2.78, 20.15) * mm, "end": v(2.63, 20.5) * mm});
            skLineSegment(sketch, "E657", {"start": v(2.63, 21) * mm, "end": v(2.63, 20.5) * mm});
            skArc(sketch, "E658", {"start": v(2.63, 21) * mm, "mid": v(2.78, 21.35) * mm, "end": v(3.14, 21.5) * mm});
            skLineSegment(sketch, "E659", {"start": v(5.49, 21.5) * mm, "end": v(3.14, 21.5) * mm});
            skArc(sketch, "E660", {"start": v(6, 22) * mm, "mid": v(5.85, 21.65) * mm, "end": v(5.49, 21.5) * mm});
            skLineSegment(sketch, "E661", {"start": v(6, 22) * mm, "end": v(6, 22.73) * mm});
            skArc(sketch, "E662", {"start": v(5.85, 23.1) * mm, "mid": v(5.96, 22.93) * mm, "end": v(6, 22.73) * mm});
            skLineSegment(sketch, "E663", {"start": v(2.74, 26.2) * mm, "end": v(5.85, 23.1) * mm});
            skArc(sketch, "E664", {"start": v(2.38, 26.35) * mm, "mid": v(2.58, 26.3) * mm, "end": v(2.74, 26.2) * mm});
            skLineSegment(sketch, "E665", {"start": v(0, 26.35) * mm, "end": v(2.38, 26.35) * mm});
            skArc(sketch, "E666", {"start": v(3.65, 27.62) * mm, "mid": v(3.7, 27.42) * mm, "end": v(3.8, 27.26) * mm});
            skLineSegment(sketch, "E667", {"start": v(3.8, 27.26) * mm, "end": v(7.35, 23.71) * mm});
            skArc(sketch, "E668", {"start": v(7.35, 23.71) * mm, "mid": v(7.46, 23.55) * mm, "end": v(7.5, 23.36) * mm});
            skLineSegment(sketch, "E669", {"start": v(7.5, 22) * mm, "end": v(7.5, 23.36) * mm});
            skArc(sketch, "E670", {"start": v(8, 21.5) * mm, "mid": v(7.64, 21.65) * mm, "end": v(7.5, 22) * mm});
            skLineSegment(sketch, "E671", {"start": v(12, 21.5) * mm, "end": v(8, 21.5) * mm});
            skArc(sketch, "E672", {"start": v(12, 21.5) * mm, "mid": v(12.36, 21.65) * mm, "end": v(12.5, 22) * mm});
            skLineSegment(sketch, "E673", {"start": v(12.5, 22) * mm, "end": v(12.5, 23.36) * mm});
            skArc(sketch, "E674", {"start": v(12.65, 23.71) * mm, "mid": v(12.54, 23.55) * mm, "end": v(12.5, 23.36) * mm});
            skLineSegment(sketch, "E675", {"start": v(16.2, 27.26) * mm, "end": v(12.65, 23.71) * mm});
            skArc(sketch, "E676", {"start": v(16.2, 27.26) * mm, "mid": v(16.3, 27.42) * mm, "end": v(16.35, 27.62) * mm});
            skLineSegment(sketch, "E677", {"start": v(16.35, 27.62) * mm, "end": v(16.35, 32.38) * mm});
            skArc(sketch, "E678", {"start": v(16.35, 32.38) * mm, "mid": v(16.3, 32.58) * mm, "end": v(16.2, 32.74) * mm});
            skLineSegment(sketch, "E679", {"start": v(16.2, 32.74) * mm, "end": v(12.65, 36.29) * mm});
            skLineSegment(sketch, "E680", {"start": v(3.8, 32.74) * mm, "end": v(7.35, 36.29) * mm});
            skArc(sketch, "E681", {"start": v(3.65, 32.38) * mm, "mid": v(3.7, 32.58) * mm, "end": v(3.8, 32.74) * mm});
            skArc(sketch, "E682", {"start": v(0.8, 28.06) * mm, "mid": v(0.4, 27.94) * mm, "end": v(0, 27.9) * mm});
            skArc(sketch, "E683", {"start": v(0, 32.1) * mm, "mid": v(0.4, 32.06) * mm, "end": v(0.8, 31.94) * mm});
            skCircle(sketch, "E684", {"center": v(-32.45, 30) * mm, "radius": 4 * mm});
            skCircle(sketch, "E685", {"center": v(32.45, 30) * mm, "radius": 4 * mm});
            skLineSegment(sketch, "E686", {"start": v(-25.85, 36.9) * mm, "end": v(-25.85, 43.1) * mm});
            skLineSegment(sketch, "E687", {"start": v(-14.15, 43.1) * mm, "end": v(-14.15, 36.9) * mm});
            skLineSegment(sketch, "E688", {"start": v(-12.65, 36.29) * mm, "end": v(-7.35, 36.29) * mm});
            skLineSegment(sketch, "E689", {"start": v(7.35, 36.29) * mm, "end": v(12.65, 36.29) * mm});
            skLineSegment(sketch, "E690", {"start": v(25.85, 36.9) * mm, "end": v(25.85, 43.1) * mm});
            skLineSegment(sketch, "E691", {"start": v(14.15, 43.1) * mm, "end": v(14.15, 36.9) * mm});
            skLineSegment(sketch, "E692", {"start": v(12.65, 43.71) * mm, "end": v(7.35, 43.71) * mm});
            skLineSegment(sketch, "E693", {"start": v(5.85, 43.1) * mm, "end": v(5.85, 36.9) * mm});
            skLineSegment(sketch, "E694", {"start": v(-5.85, 36.9) * mm, "end": v(-5.85, 43.1) * mm});
            skLineSegment(sketch, "E695", {"start": v(-7.35, 43.71) * mm, "end": v(-12.65, 43.71) * mm});
            skSolve(sketch);
        }
        {
            var Q0;
            Q0 = qSketchRegion(id + "F0", true);
            extrude(context, id + "F2", {"entities" : qUnion([Q0]), "depth" : 1500 * mm, "offsetDistance" : 25 * mm});
        }
        {
            var Q0;
            Q0 = qSketchRegion(id + "F1", true);
            extrude(context, id + "F3", {"entities" : qUnion([Q0]), "depth" : 1200 * mm, "offsetDistance" : 25 * mm});
        }
        {
            var Q0;
            Q0=qCreatedBy(makeId("Top.planeOp"),FACE);
            var sketch = newSketch(context, id + "F4", { "sketchPlane" : qUnion([Q0])});
            skLineSegment(sketch, "E696", {"start": v(-55.77, -42.08) * mm, "end": v(-55.77, -46.85) * mm});
            skLineSegment(sketch, "E697", {"start": v(-69.99, -42.16) * mm, "end": v(-69.8, -42.34) * mm});
            skArc(sketch, "E698", {"start": v(-52.92, -42.53) * mm, "mid": v(-52.52, -42.41) * mm, "end": v(-52.11, -42.37) * mm});
            skArc(sketch, "E699", {"start": v(-54.24, -42.16) * mm, "mid": v(-53.47, -41.96) * mm, "end": v(-52.92, -42.53) * mm});
            skLineSegment(sketch, "E700", {"start": v(-54.24, -42.16) * mm, "end": v(-54.42, -42.34) * mm});
            skArc(sketch, "E701", {"start": v(-54.05, -43.66) * mm, "mid": v(-54.62, -43.11) * mm, "end": v(-54.42, -42.34) * mm});
            skArc(sketch, "E702", {"start": v(-54.05, -45.27) * mm, "mid": v(-54.2, -44.47) * mm, "end": v(-54.05, -43.66) * mm});
            skArc(sketch, "E703", {"start": v(-54.42, -46.6) * mm, "mid": v(-54.62, -45.82) * mm, "end": v(-54.05, -45.27) * mm});
            skLineSegment(sketch, "E704", {"start": v(-54.42, -46.6) * mm, "end": v(-54.24, -46.77) * mm});
            skArc(sketch, "E705", {"start": v(-52.92, -46.4) * mm, "mid": v(-53.47, -46.97) * mm, "end": v(-54.24, -46.77) * mm});
            skArc(sketch, "E706", {"start": v(-52.11, -46.56) * mm, "mid": v(-52.52, -46.52) * mm, "end": v(-52.92, -46.4) * mm});
            skArc(sketch, "E707", {"start": v(-69.99, -42.16) * mm, "mid": v(-70.76, -41.96) * mm, "end": v(-71.3, -42.53) * mm});
            skArc(sketch, "E708", {"start": v(-71.3, -42.53) * mm, "mid": v(-72.11, -42.37) * mm, "end": v(-72.92, -42.53) * mm});
            skArc(sketch, "E709", {"start": v(-72.92, -42.53) * mm, "mid": v(-73.47, -41.96) * mm, "end": v(-74.24, -42.16) * mm});
            skLineSegment(sketch, "E710", {"start": v(-74.42, -42.34) * mm, "end": v(-74.24, -42.16) * mm});
            skArc(sketch, "E711", {"start": v(-74.42, -42.34) * mm, "mid": v(-74.62, -43.11) * mm, "end": v(-74.05, -43.66) * mm});
            skArc(sketch, "E712", {"start": v(-74.05, -43.66) * mm, "mid": v(-74.2, -44.47) * mm, "end": v(-74.05, -45.27) * mm});
            skArc(sketch, "E713", {"start": v(-74.05, -45.27) * mm, "mid": v(-74.62, -45.82) * mm, "end": v(-74.42, -46.6) * mm});
            skLineSegment(sketch, "E714", {"start": v(-74.24, -46.77) * mm, "end": v(-74.42, -46.6) * mm});
            skArc(sketch, "E715", {"start": v(-74.24, -46.77) * mm, "mid": v(-73.47, -46.97) * mm, "end": v(-72.92, -46.4) * mm});
            skArc(sketch, "E716", {"start": v(-72.92, -46.4) * mm, "mid": v(-72.11, -46.56) * mm, "end": v(-71.3, -46.4) * mm});
            skArc(sketch, "E717", {"start": v(-71.3, -46.4) * mm, "mid": v(-70.76, -46.97) * mm, "end": v(-69.99, -46.77) * mm});
            skLineSegment(sketch, "E718", {"start": v(-69.8, -46.6) * mm, "end": v(-69.99, -46.77) * mm});
            skArc(sketch, "E719", {"start": v(-69.8, -46.6) * mm, "mid": v(-69.6, -45.82) * mm, "end": v(-70.18, -45.27) * mm});
            skArc(sketch, "E720", {"start": v(-70.18, -45.27) * mm, "mid": v(-70.02, -44.47) * mm, "end": v(-70.18, -43.66) * mm});
            skArc(sketch, "E721", {"start": v(-70.18, -43.66) * mm, "mid": v(-69.6, -43.11) * mm, "end": v(-69.8, -42.34) * mm});
            skLineSegment(sketch, "E722", {"start": v(-52.11, -48.12) * mm, "end": v(-54.5, -48.12) * mm});
            skArc(sketch, "E723", {"start": v(-54.86, -48.27) * mm, "mid": v(-54.7, -48.16) * mm, "end": v(-54.5, -48.12) * mm});
            skLineSegment(sketch, "E724", {"start": v(-54.86, -48.27) * mm, "end": v(-57.96, -51.37) * mm});
            skArc(sketch, "E725", {"start": v(-58.1, -51.73) * mm, "mid": v(-58.07, -51.54) * mm, "end": v(-57.96, -51.37) * mm});
            skLineSegment(sketch, "E726", {"start": v(-58.1, -51.73) * mm, "end": v(-58.1, -52.46) * mm});
            skArc(sketch, "E727", {"start": v(-57.6, -52.97) * mm, "mid": v(-57.96, -52.82) * mm, "end": v(-58.1, -52.46) * mm});
            skLineSegment(sketch, "E728", {"start": v(-57.6, -52.97) * mm, "end": v(-55.25, -52.97) * mm});
            skArc(sketch, "E729", {"start": v(-55.25, -52.97) * mm, "mid": v(-54.9, -53.12) * mm, "end": v(-54.74, -53.48) * mm});
            skLineSegment(sketch, "E730", {"start": v(-54.74, -53.96) * mm, "end": v(-54.74, -53.48) * mm});
            skArc(sketch, "E731", {"start": v(-54.74, -53.96) * mm, "mid": v(-54.9, -54.32) * mm, "end": v(-55.25, -54.47) * mm});
            skLineSegment(sketch, "E732", {"start": v(-68.97, -54.47) * mm, "end": v(-55.25, -54.47) * mm});
            skArc(sketch, "E733", {"start": v(-69.48, -53.96) * mm, "mid": v(-69.33, -54.32) * mm, "end": v(-68.97, -54.47) * mm});
            skLineSegment(sketch, "E734", {"start": v(-69.48, -53.96) * mm, "end": v(-69.48, -53.48) * mm});
            skArc(sketch, "E735", {"start": v(-68.97, -52.97) * mm, "mid": v(-69.33, -53.12) * mm, "end": v(-69.48, -53.48) * mm});
            skLineSegment(sketch, "E736", {"start": v(-66.63, -52.97) * mm, "end": v(-68.97, -52.97) * mm});
            skArc(sketch, "E737", {"start": v(-66.63, -52.97) * mm, "mid": v(-66.27, -52.82) * mm, "end": v(-66.12, -52.46) * mm});
            skLineSegment(sketch, "E738", {"start": v(-66.12, -51.73) * mm, "end": v(-66.12, -52.46) * mm});
            skArc(sketch, "E739", {"start": v(-66.12, -51.73) * mm, "mid": v(-66.16, -51.54) * mm, "end": v(-66.27, -51.37) * mm});
            skLineSegment(sketch, "E740", {"start": v(-69.37, -48.27) * mm, "end": v(-66.27, -51.37) * mm});
            skArc(sketch, "E741", {"start": v(-69.37, -48.27) * mm, "mid": v(-69.53, -48.16) * mm, "end": v(-69.73, -48.12) * mm});
            skLineSegment(sketch, "E742", {"start": v(-74.5, -48.12) * mm, "end": v(-69.73, -48.12) * mm});
            skArc(sketch, "E743", {"start": v(-74.5, -48.12) * mm, "mid": v(-74.7, -48.16) * mm, "end": v(-74.86, -48.27) * mm});
            skLineSegment(sketch, "E744", {"start": v(-77.96, -51.37) * mm, "end": v(-74.86, -48.27) * mm});
            skArc(sketch, "E745", {"start": v(-77.96, -51.37) * mm, "mid": v(-78.07, -51.54) * mm, "end": v(-78.1, -51.73) * mm});
            skLineSegment(sketch, "E746", {"start": v(-78.1, -51.73) * mm, "end": v(-78.1, -52.46) * mm});
            skArc(sketch, "E747", {"start": v(-78.1, -52.46) * mm, "mid": v(-77.96, -52.82) * mm, "end": v(-77.6, -52.97) * mm});
            skLineSegment(sketch, "E748", {"start": v(-75.25, -52.97) * mm, "end": v(-77.6, -52.97) * mm});
            skArc(sketch, "E749", {"start": v(-74.74, -53.48) * mm, "mid": v(-74.9, -53.12) * mm, "end": v(-75.25, -52.97) * mm});
            skLineSegment(sketch, "E750", {"start": v(-74.74, -53.48) * mm, "end": v(-74.74, -53.96) * mm});
            skArc(sketch, "E751", {"start": v(-75.25, -54.47) * mm, "mid": v(-74.9, -54.32) * mm, "end": v(-74.74, -53.96) * mm});
            skLineSegment(sketch, "E752", {"start": v(-80.61, -54.47) * mm, "end": v(-75.25, -54.47) * mm});
            skArc(sketch, "E753", {"start": v(-82.11, -52.97) * mm, "mid": v(-81.67, -54.03) * mm, "end": v(-80.61, -54.47) * mm});
            skLineSegment(sketch, "E754", {"start": v(-82.11, -52.97) * mm, "end": v(-82.11, -47.6) * mm});
            skArc(sketch, "E755", {"start": v(-81.6, -47.1) * mm, "mid": v(-81.96, -47.25) * mm, "end": v(-82.11, -47.6) * mm});
            skLineSegment(sketch, "E756", {"start": v(-81.6, -47.1) * mm, "end": v(-81.12, -47.1) * mm});
            skArc(sketch, "E757", {"start": v(-80.61, -47.6) * mm, "mid": v(-80.76, -47.25) * mm, "end": v(-81.12, -47.1) * mm});
            skLineSegment(sketch, "E758", {"start": v(-80.61, -49.95) * mm, "end": v(-80.61, -47.6) * mm});
            skArc(sketch, "E759", {"start": v(-80.61, -49.95) * mm, "mid": v(-80.46, -50.31) * mm, "end": v(-80.1, -50.46) * mm});
            skLineSegment(sketch, "E760", {"start": v(-79.38, -50.46) * mm, "end": v(-80.1, -50.46) * mm});
            skArc(sketch, "E761", {"start": v(-79.38, -50.46) * mm, "mid": v(-79.18, -50.42) * mm, "end": v(-79.02, -50.31) * mm});
            skLineSegment(sketch, "E762", {"start": v(-75.92, -47.21) * mm, "end": v(-79.02, -50.31) * mm});
            skArc(sketch, "E763", {"start": v(-75.92, -47.21) * mm, "mid": v(-75.8, -47.05) * mm, "end": v(-75.77, -46.85) * mm});
            skLineSegment(sketch, "E764", {"start": v(-75.77, -42.08) * mm, "end": v(-75.77, -46.85) * mm});
            skArc(sketch, "E765", {"start": v(-75.77, -42.08) * mm, "mid": v(-75.8, -41.89) * mm, "end": v(-75.92, -41.72) * mm});
            skLineSegment(sketch, "E766", {"start": v(-75.92, -41.72) * mm, "end": v(-79.02, -38.62) * mm});
            skArc(sketch, "E767", {"start": v(-79.02, -38.62) * mm, "mid": v(-79.18, -38.51) * mm, "end": v(-79.38, -38.47) * mm});
            skLineSegment(sketch, "E768", {"start": v(-79.38, -38.47) * mm, "end": v(-80.1, -38.47) * mm});
            skArc(sketch, "E769", {"start": v(-80.1, -38.47) * mm, "mid": v(-80.46, -38.62) * mm, "end": v(-80.61, -38.98) * mm});
            skLineSegment(sketch, "E770", {"start": v(-80.61, -38.98) * mm, "end": v(-80.61, -41.33) * mm});
            skArc(sketch, "E771", {"start": v(-81.12, -41.84) * mm, "mid": v(-80.76, -41.69) * mm, "end": v(-80.61, -41.33) * mm});
            skLineSegment(sketch, "E772", {"start": v(-81.12, -41.84) * mm, "end": v(-81.6, -41.84) * mm});
            skArc(sketch, "E773", {"start": v(-82.11, -41.33) * mm, "mid": v(-81.96, -41.69) * mm, "end": v(-81.6, -41.84) * mm});
            skLineSegment(sketch, "E774", {"start": v(-82.11, -41.33) * mm, "end": v(-82.11, -35.97) * mm});
            skArc(sketch, "E775", {"start": v(-80.61, -34.47) * mm, "mid": v(-81.67, -34.9) * mm, "end": v(-82.11, -35.97) * mm});
            skLineSegment(sketch, "E776", {"start": v(-80.61, -34.47) * mm, "end": v(-75.25, -34.47) * mm});
            skArc(sketch, "E777", {"start": v(-74.74, -34.98) * mm, "mid": v(-74.9, -34.62) * mm, "end": v(-75.25, -34.47) * mm});
            skLineSegment(sketch, "E778", {"start": v(-74.74, -34.98) * mm, "end": v(-74.74, -35.46) * mm});
            skArc(sketch, "E779", {"start": v(-75.25, -35.97) * mm, "mid": v(-74.9, -35.82) * mm, "end": v(-74.74, -35.46) * mm});
            skLineSegment(sketch, "E780", {"start": v(-75.25, -35.97) * mm, "end": v(-77.6, -35.97) * mm});
            skArc(sketch, "E781", {"start": v(-77.6, -35.97) * mm, "mid": v(-77.96, -36.12) * mm, "end": v(-78.1, -36.48) * mm});
            skLineSegment(sketch, "E782", {"start": v(-78.1, -36.48) * mm, "end": v(-78.1, -37.2) * mm});
            skArc(sketch, "E783", {"start": v(-78.1, -37.2) * mm, "mid": v(-78.07, -37.4) * mm, "end": v(-77.96, -37.56) * mm});
            skLineSegment(sketch, "E784", {"start": v(-77.96, -37.56) * mm, "end": v(-74.86, -40.66) * mm});
            skArc(sketch, "E785", {"start": v(-74.86, -40.66) * mm, "mid": v(-74.7, -40.77) * mm, "end": v(-74.5, -40.81) * mm});
            skLineSegment(sketch, "E786", {"start": v(-74.5, -40.81) * mm, "end": v(-69.73, -40.81) * mm});
            skArc(sketch, "E787", {"start": v(-69.73, -40.81) * mm, "mid": v(-69.53, -40.77) * mm, "end": v(-69.37, -40.66) * mm});
            skLineSegment(sketch, "E788", {"start": v(-69.37, -40.66) * mm, "end": v(-66.27, -37.56) * mm});
            skArc(sketch, "E789", {"start": v(-66.27, -37.56) * mm, "mid": v(-66.16, -37.4) * mm, "end": v(-66.12, -37.2) * mm});
            skLineSegment(sketch, "E790", {"start": v(-66.12, -36.48) * mm, "end": v(-66.12, -37.2) * mm});
            skArc(sketch, "E791", {"start": v(-66.12, -36.48) * mm, "mid": v(-66.27, -36.12) * mm, "end": v(-66.63, -35.97) * mm});
            skLineSegment(sketch, "E792", {"start": v(-66.63, -35.97) * mm, "end": v(-68.97, -35.97) * mm});
            skArc(sketch, "E793", {"start": v(-69.48, -35.46) * mm, "mid": v(-69.33, -35.82) * mm, "end": v(-68.97, -35.97) * mm});
            skLineSegment(sketch, "E794", {"start": v(-69.48, -35.46) * mm, "end": v(-69.48, -34.98) * mm});
            skArc(sketch, "E795", {"start": v(-68.97, -34.47) * mm, "mid": v(-69.33, -34.62) * mm, "end": v(-69.48, -34.98) * mm});
            skLineSegment(sketch, "E796", {"start": v(-55.25, -34.47) * mm, "end": v(-68.97, -34.47) * mm});
            skArc(sketch, "E797", {"start": v(-55.25, -34.47) * mm, "mid": v(-54.9, -34.62) * mm, "end": v(-54.74, -34.98) * mm});
            skLineSegment(sketch, "E798", {"start": v(-54.74, -35.46) * mm, "end": v(-54.74, -34.98) * mm});
            skArc(sketch, "E799", {"start": v(-54.74, -35.46) * mm, "mid": v(-54.9, -35.82) * mm, "end": v(-55.25, -35.97) * mm});
            skLineSegment(sketch, "E800", {"start": v(-57.6, -35.97) * mm, "end": v(-55.25, -35.97) * mm});
            skArc(sketch, "E801", {"start": v(-58.1, -36.48) * mm, "mid": v(-57.96, -36.12) * mm, "end": v(-57.6, -35.97) * mm});
            skLineSegment(sketch, "E802", {"start": v(-58.1, -36.48) * mm, "end": v(-58.1, -37.2) * mm});
            skArc(sketch, "E803", {"start": v(-57.96, -37.56) * mm, "mid": v(-58.07, -37.4) * mm, "end": v(-58.1, -37.2) * mm});
            skLineSegment(sketch, "E804", {"start": v(-54.86, -40.66) * mm, "end": v(-57.96, -37.56) * mm});
            skArc(sketch, "E805", {"start": v(-54.5, -40.81) * mm, "mid": v(-54.7, -40.77) * mm, "end": v(-54.86, -40.66) * mm});
            skLineSegment(sketch, "E806", {"start": v(-52.11, -40.81) * mm, "end": v(-54.5, -40.81) * mm});
            skArc(sketch, "E807", {"start": v(-55.77, -42.08) * mm, "mid": v(-55.8, -41.89) * mm, "end": v(-55.92, -41.72) * mm});
            skLineSegment(sketch, "E808", {"start": v(-55.92, -41.72) * mm, "end": v(-59.46, -38.18) * mm});
            skArc(sketch, "E809", {"start": v(-59.46, -38.18) * mm, "mid": v(-59.57, -38.02) * mm, "end": v(-59.6, -37.82) * mm});
            skLineSegment(sketch, "E810", {"start": v(-59.6, -36.48) * mm, "end": v(-59.6, -37.82) * mm});
            skArc(sketch, "E811", {"start": v(-60.12, -35.97) * mm, "mid": v(-59.76, -36.12) * mm, "end": v(-59.6, -36.48) * mm});
            skLineSegment(sketch, "E812", {"start": v(-64.1, -35.97) * mm, "end": v(-60.12, -35.97) * mm});
            skArc(sketch, "E813", {"start": v(-64.1, -35.97) * mm, "mid": v(-64.47, -36.12) * mm, "end": v(-64.62, -36.48) * mm});
            skLineSegment(sketch, "E814", {"start": v(-64.62, -36.48) * mm, "end": v(-64.62, -37.82) * mm});
            skArc(sketch, "E815", {"start": v(-64.77, -38.18) * mm, "mid": v(-64.66, -38.02) * mm, "end": v(-64.62, -37.82) * mm});
            skLineSegment(sketch, "E816", {"start": v(-68.3, -41.72) * mm, "end": v(-64.77, -38.18) * mm});
            skArc(sketch, "E817", {"start": v(-68.3, -41.72) * mm, "mid": v(-68.42, -41.89) * mm, "end": v(-68.46, -42.08) * mm});
            skLineSegment(sketch, "E818", {"start": v(-68.46, -42.08) * mm, "end": v(-68.46, -46.85) * mm});
            skArc(sketch, "E819", {"start": v(-68.46, -46.85) * mm, "mid": v(-68.42, -47.05) * mm, "end": v(-68.3, -47.21) * mm});
            skLineSegment(sketch, "E820", {"start": v(-68.3, -47.21) * mm, "end": v(-64.77, -50.75) * mm});
            skArc(sketch, "E821", {"start": v(-64.62, -51.11) * mm, "mid": v(-64.66, -50.92) * mm, "end": v(-64.77, -50.75) * mm});
            skLineSegment(sketch, "E822", {"start": v(-64.62, -51.11) * mm, "end": v(-64.62, -52.46) * mm});
            skArc(sketch, "E823", {"start": v(-64.62, -52.46) * mm, "mid": v(-64.47, -52.82) * mm, "end": v(-64.1, -52.97) * mm});
            skLineSegment(sketch, "E824", {"start": v(-64.1, -52.97) * mm, "end": v(-60.12, -52.97) * mm});
            skArc(sketch, "E825", {"start": v(-59.6, -52.46) * mm, "mid": v(-59.76, -52.82) * mm, "end": v(-60.12, -52.97) * mm});
            skLineSegment(sketch, "E826", {"start": v(-59.6, -51.11) * mm, "end": v(-59.6, -52.46) * mm});
            skArc(sketch, "E827", {"start": v(-59.6, -51.11) * mm, "mid": v(-59.57, -50.92) * mm, "end": v(-59.46, -50.75) * mm});
            skLineSegment(sketch, "E828", {"start": v(-55.92, -47.21) * mm, "end": v(-59.46, -50.75) * mm});
            skArc(sketch, "E829", {"start": v(-55.77, -46.85) * mm, "mid": v(-55.8, -47.05) * mm, "end": v(-55.92, -47.21) * mm});
            skLineSegment(sketch, "E830", {"start": v(-48.46, -42.08) * mm, "end": v(-48.46, -46.85) * mm});
            skLineSegment(sketch, "E831", {"start": v(-34.24, -42.16) * mm, "end": v(-34.42, -42.34) * mm});
            skArc(sketch, "E832", {"start": v(-51.3, -42.53) * mm, "mid": v(-50.76, -41.96) * mm, "end": v(-49.99, -42.16) * mm});
            skLineSegment(sketch, "E833", {"start": v(-49.99, -42.16) * mm, "end": v(-49.8, -42.34) * mm});
            skArc(sketch, "E834", {"start": v(-49.8, -42.34) * mm, "mid": v(-49.6, -43.11) * mm, "end": v(-50.18, -43.66) * mm});
            skArc(sketch, "E835", {"start": v(-50.18, -43.66) * mm, "mid": v(-50.02, -44.47) * mm, "end": v(-50.18, -45.27) * mm});
            skArc(sketch, "E836", {"start": v(-50.18, -45.27) * mm, "mid": v(-49.6, -45.82) * mm, "end": v(-49.8, -46.6) * mm});
            skLineSegment(sketch, "E837", {"start": v(-49.8, -46.6) * mm, "end": v(-49.99, -46.77) * mm});
            skArc(sketch, "E838", {"start": v(-49.99, -46.77) * mm, "mid": v(-50.76, -46.97) * mm, "end": v(-51.3, -46.4) * mm});
            skArc(sketch, "E839", {"start": v(-32.92, -42.53) * mm, "mid": v(-33.47, -41.96) * mm, "end": v(-34.24, -42.16) * mm});
            skArc(sketch, "E840", {"start": v(-31.3, -42.53) * mm, "mid": v(-32.11, -42.37) * mm, "end": v(-32.92, -42.53) * mm});
            skArc(sketch, "E841", {"start": v(-29.99, -42.16) * mm, "mid": v(-30.76, -41.96) * mm, "end": v(-31.3, -42.53) * mm});
            skLineSegment(sketch, "E842", {"start": v(-29.8, -42.34) * mm, "end": v(-29.99, -42.16) * mm});
            skArc(sketch, "E843", {"start": v(-30.18, -43.66) * mm, "mid": v(-29.6, -43.11) * mm, "end": v(-29.8, -42.34) * mm});
            skArc(sketch, "E844", {"start": v(-30.18, -45.27) * mm, "mid": v(-30.02, -44.47) * mm, "end": v(-30.18, -43.66) * mm});
            skArc(sketch, "E845", {"start": v(-29.8, -46.6) * mm, "mid": v(-29.6, -45.82) * mm, "end": v(-30.18, -45.27) * mm});
            skLineSegment(sketch, "E846", {"start": v(-29.99, -46.77) * mm, "end": v(-29.8, -46.6) * mm});
            skArc(sketch, "E847", {"start": v(-31.3, -46.4) * mm, "mid": v(-30.76, -46.97) * mm, "end": v(-29.99, -46.77) * mm});
            skArc(sketch, "E848", {"start": v(-32.92, -46.4) * mm, "mid": v(-32.11, -46.56) * mm, "end": v(-31.3, -46.4) * mm});
            skArc(sketch, "E849", {"start": v(-34.24, -46.77) * mm, "mid": v(-33.47, -46.97) * mm, "end": v(-32.92, -46.4) * mm});
            skLineSegment(sketch, "E850", {"start": v(-34.42, -46.6) * mm, "end": v(-34.24, -46.77) * mm});
            skArc(sketch, "E851", {"start": v(-34.05, -45.27) * mm, "mid": v(-34.62, -45.82) * mm, "end": v(-34.42, -46.6) * mm});
            skArc(sketch, "E852", {"start": v(-34.05, -43.66) * mm, "mid": v(-34.2, -44.47) * mm, "end": v(-34.05, -45.27) * mm});
            skArc(sketch, "E853", {"start": v(-34.42, -42.34) * mm, "mid": v(-34.62, -43.11) * mm, "end": v(-34.05, -43.66) * mm});
            skLineSegment(sketch, "E854", {"start": v(-52.11, -48.12) * mm, "end": v(-49.73, -48.12) * mm});
            skArc(sketch, "E855", {"start": v(-49.73, -48.12) * mm, "mid": v(-49.53, -48.16) * mm, "end": v(-49.37, -48.27) * mm});
            skLineSegment(sketch, "E856", {"start": v(-49.37, -48.27) * mm, "end": v(-46.27, -51.37) * mm});
            skArc(sketch, "E857", {"start": v(-46.27, -51.37) * mm, "mid": v(-46.16, -51.54) * mm, "end": v(-46.12, -51.73) * mm});
            skLineSegment(sketch, "E858", {"start": v(-46.12, -51.73) * mm, "end": v(-46.12, -52.46) * mm});
            skArc(sketch, "E859", {"start": v(-46.12, -52.46) * mm, "mid": v(-46.27, -52.82) * mm, "end": v(-46.63, -52.97) * mm});
            skLineSegment(sketch, "E860", {"start": v(-46.63, -52.97) * mm, "end": v(-48.97, -52.97) * mm});
            skArc(sketch, "E861", {"start": v(-49.48, -53.48) * mm, "mid": v(-49.33, -53.12) * mm, "end": v(-48.97, -52.97) * mm});
            skLineSegment(sketch, "E862", {"start": v(-49.48, -53.96) * mm, "end": v(-49.48, -53.48) * mm});
            skArc(sketch, "E863", {"start": v(-48.97, -54.47) * mm, "mid": v(-49.33, -54.32) * mm, "end": v(-49.48, -53.96) * mm});
            skLineSegment(sketch, "E864", {"start": v(-35.25, -54.47) * mm, "end": v(-48.97, -54.47) * mm});
            skArc(sketch, "E865", {"start": v(-35.25, -54.47) * mm, "mid": v(-34.9, -54.32) * mm, "end": v(-34.74, -53.96) * mm});
            skLineSegment(sketch, "E866", {"start": v(-34.74, -53.96) * mm, "end": v(-34.74, -53.48) * mm});
            skArc(sketch, "E867", {"start": v(-34.74, -53.48) * mm, "mid": v(-34.9, -53.12) * mm, "end": v(-35.25, -52.97) * mm});
            skLineSegment(sketch, "E868", {"start": v(-37.6, -52.97) * mm, "end": v(-35.25, -52.97) * mm});
            skArc(sketch, "E869", {"start": v(-38.1, -52.46) * mm, "mid": v(-37.96, -52.82) * mm, "end": v(-37.6, -52.97) * mm});
            skLineSegment(sketch, "E870", {"start": v(-38.1, -51.73) * mm, "end": v(-38.1, -52.46) * mm});
            skArc(sketch, "E871", {"start": v(-37.96, -51.37) * mm, "mid": v(-38.07, -51.54) * mm, "end": v(-38.1, -51.73) * mm});
            skLineSegment(sketch, "E872", {"start": v(-34.86, -48.27) * mm, "end": v(-37.96, -51.37) * mm});
            skArc(sketch, "E873", {"start": v(-34.5, -48.12) * mm, "mid": v(-34.7, -48.16) * mm, "end": v(-34.86, -48.27) * mm});
            skLineSegment(sketch, "E874", {"start": v(-29.73, -48.12) * mm, "end": v(-34.5, -48.12) * mm});
            skArc(sketch, "E875", {"start": v(-29.37, -48.27) * mm, "mid": v(-29.53, -48.16) * mm, "end": v(-29.73, -48.12) * mm});
            skLineSegment(sketch, "E876", {"start": v(-26.27, -51.37) * mm, "end": v(-29.37, -48.27) * mm});
            skArc(sketch, "E877", {"start": v(-26.12, -51.73) * mm, "mid": v(-26.16, -51.54) * mm, "end": v(-26.27, -51.37) * mm});
            skLineSegment(sketch, "E878", {"start": v(-26.12, -51.73) * mm, "end": v(-26.12, -52.46) * mm});
            skArc(sketch, "E879", {"start": v(-26.63, -52.97) * mm, "mid": v(-26.27, -52.82) * mm, "end": v(-26.12, -52.46) * mm});
            skLineSegment(sketch, "E880", {"start": v(-28.97, -52.97) * mm, "end": v(-26.63, -52.97) * mm});
            skArc(sketch, "E881", {"start": v(-28.97, -52.97) * mm, "mid": v(-29.33, -53.12) * mm, "end": v(-29.48, -53.48) * mm});
            skLineSegment(sketch, "E882", {"start": v(-29.48, -53.48) * mm, "end": v(-29.48, -53.96) * mm});
            skArc(sketch, "E883", {"start": v(-29.48, -53.96) * mm, "mid": v(-29.33, -54.32) * mm, "end": v(-28.97, -54.47) * mm});
            skLineSegment(sketch, "E884", {"start": v(-23.61, -54.47) * mm, "end": v(-28.97, -54.47) * mm});
            skArc(sketch, "E885", {"start": v(-23.61, -54.47) * mm, "mid": v(-22.55, -54.03) * mm, "end": v(-22.11, -52.97) * mm});
            skLineSegment(sketch, "E886", {"start": v(-22.11, -52.97) * mm, "end": v(-22.11, -47.6) * mm});
            skArc(sketch, "E887", {"start": v(-22.11, -47.6) * mm, "mid": v(-22.26, -47.25) * mm, "end": v(-22.62, -47.1) * mm});
            skLineSegment(sketch, "E888", {"start": v(-22.62, -47.1) * mm, "end": v(-23.1, -47.1) * mm});
            skArc(sketch, "E889", {"start": v(-23.1, -47.1) * mm, "mid": v(-23.46, -47.25) * mm, "end": v(-23.61, -47.6) * mm});
            skLineSegment(sketch, "E890", {"start": v(-23.61, -49.95) * mm, "end": v(-23.61, -47.6) * mm});
            skArc(sketch, "E891", {"start": v(-24.12, -50.46) * mm, "mid": v(-23.76, -50.31) * mm, "end": v(-23.61, -49.95) * mm});
            skLineSegment(sketch, "E892", {"start": v(-24.85, -50.46) * mm, "end": v(-24.12, -50.46) * mm});
            skArc(sketch, "E893", {"start": v(-25.2, -50.31) * mm, "mid": v(-25.04, -50.42) * mm, "end": v(-24.85, -50.46) * mm});
            skLineSegment(sketch, "E894", {"start": v(-28.3, -47.21) * mm, "end": v(-25.2, -50.31) * mm});
            skArc(sketch, "E895", {"start": v(-28.46, -46.85) * mm, "mid": v(-28.42, -47.05) * mm, "end": v(-28.3, -47.21) * mm});
            skLineSegment(sketch, "E896", {"start": v(-28.46, -42.08) * mm, "end": v(-28.46, -46.85) * mm});
            skArc(sketch, "E897", {"start": v(-28.3, -41.72) * mm, "mid": v(-28.42, -41.89) * mm, "end": v(-28.46, -42.08) * mm});
            skLineSegment(sketch, "E898", {"start": v(-28.3, -41.72) * mm, "end": v(-25.2, -38.62) * mm});
            skArc(sketch, "E899", {"start": v(-24.85, -38.47) * mm, "mid": v(-25.04, -38.51) * mm, "end": v(-25.2, -38.62) * mm});
            skLineSegment(sketch, "E900", {"start": v(-24.85, -38.47) * mm, "end": v(-24.12, -38.47) * mm});
            skArc(sketch, "E901", {"start": v(-23.61, -38.98) * mm, "mid": v(-23.76, -38.62) * mm, "end": v(-24.12, -38.47) * mm});
            skLineSegment(sketch, "E902", {"start": v(-23.61, -38.98) * mm, "end": v(-23.61, -41.33) * mm});
            skArc(sketch, "E903", {"start": v(-23.61, -41.33) * mm, "mid": v(-23.46, -41.69) * mm, "end": v(-23.1, -41.84) * mm});
            skLineSegment(sketch, "E904", {"start": v(-23.1, -41.84) * mm, "end": v(-22.62, -41.84) * mm});
            skArc(sketch, "E905", {"start": v(-22.62, -41.84) * mm, "mid": v(-22.26, -41.69) * mm, "end": v(-22.11, -41.33) * mm});
            skLineSegment(sketch, "E906", {"start": v(-22.11, -41.33) * mm, "end": v(-22.11, -35.97) * mm});
            skArc(sketch, "E907", {"start": v(-22.11, -35.97) * mm, "mid": v(-22.55, -34.9) * mm, "end": v(-23.61, -34.47) * mm});
            skLineSegment(sketch, "E908", {"start": v(-23.61, -34.47) * mm, "end": v(-28.97, -34.47) * mm});
            skArc(sketch, "E909", {"start": v(-28.97, -34.47) * mm, "mid": v(-29.33, -34.62) * mm, "end": v(-29.48, -34.98) * mm});
            skLineSegment(sketch, "E910", {"start": v(-29.48, -34.98) * mm, "end": v(-29.48, -35.46) * mm});
            skArc(sketch, "E911", {"start": v(-29.48, -35.46) * mm, "mid": v(-29.33, -35.82) * mm, "end": v(-28.97, -35.97) * mm});
            skLineSegment(sketch, "E912", {"start": v(-28.97, -35.97) * mm, "end": v(-26.63, -35.97) * mm});
            skArc(sketch, "E913", {"start": v(-26.12, -36.48) * mm, "mid": v(-26.27, -36.12) * mm, "end": v(-26.63, -35.97) * mm});
            skLineSegment(sketch, "E914", {"start": v(-26.12, -36.48) * mm, "end": v(-26.12, -37.2) * mm});
            skArc(sketch, "E915", {"start": v(-26.27, -37.56) * mm, "mid": v(-26.16, -37.4) * mm, "end": v(-26.12, -37.2) * mm});
            skLineSegment(sketch, "E916", {"start": v(-26.27, -37.56) * mm, "end": v(-29.37, -40.66) * mm});
            skArc(sketch, "E917", {"start": v(-29.73, -40.81) * mm, "mid": v(-29.53, -40.77) * mm, "end": v(-29.37, -40.66) * mm});
            skLineSegment(sketch, "E918", {"start": v(-29.73, -40.81) * mm, "end": v(-34.5, -40.81) * mm});
            skArc(sketch, "E919", {"start": v(-34.86, -40.66) * mm, "mid": v(-34.7, -40.77) * mm, "end": v(-34.5, -40.81) * mm});
            skLineSegment(sketch, "E920", {"start": v(-34.86, -40.66) * mm, "end": v(-37.96, -37.56) * mm});
            skArc(sketch, "E921", {"start": v(-38.1, -37.2) * mm, "mid": v(-38.07, -37.4) * mm, "end": v(-37.96, -37.56) * mm});
            skLineSegment(sketch, "E922", {"start": v(-38.1, -36.48) * mm, "end": v(-38.1, -37.2) * mm});
            skArc(sketch, "E923", {"start": v(-37.6, -35.97) * mm, "mid": v(-37.96, -36.12) * mm, "end": v(-38.1, -36.48) * mm});
            skLineSegment(sketch, "E924", {"start": v(-37.6, -35.97) * mm, "end": v(-35.25, -35.97) * mm});
            skArc(sketch, "E925", {"start": v(-35.25, -35.97) * mm, "mid": v(-34.9, -35.82) * mm, "end": v(-34.74, -35.46) * mm});
            skLineSegment(sketch, "E926", {"start": v(-34.74, -35.46) * mm, "end": v(-34.74, -34.98) * mm});
            skArc(sketch, "E927", {"start": v(-34.74, -34.98) * mm, "mid": v(-34.9, -34.62) * mm, "end": v(-35.25, -34.47) * mm});
            skLineSegment(sketch, "E928", {"start": v(-48.97, -34.47) * mm, "end": v(-35.25, -34.47) * mm});
            skArc(sketch, "E929", {"start": v(-49.48, -34.98) * mm, "mid": v(-49.33, -34.62) * mm, "end": v(-48.97, -34.47) * mm});
            skLineSegment(sketch, "E930", {"start": v(-49.48, -35.46) * mm, "end": v(-49.48, -34.98) * mm});
            skArc(sketch, "E931", {"start": v(-48.97, -35.97) * mm, "mid": v(-49.33, -35.82) * mm, "end": v(-49.48, -35.46) * mm});
            skLineSegment(sketch, "E932", {"start": v(-46.63, -35.97) * mm, "end": v(-48.97, -35.97) * mm});
            skArc(sketch, "E933", {"start": v(-46.63, -35.97) * mm, "mid": v(-46.27, -36.12) * mm, "end": v(-46.12, -36.48) * mm});
            skLineSegment(sketch, "E934", {"start": v(-46.12, -36.48) * mm, "end": v(-46.12, -37.2) * mm});
            skArc(sketch, "E935", {"start": v(-46.12, -37.2) * mm, "mid": v(-46.16, -37.4) * mm, "end": v(-46.27, -37.56) * mm});
            skLineSegment(sketch, "E936", {"start": v(-49.37, -40.66) * mm, "end": v(-46.27, -37.56) * mm});
            skArc(sketch, "E937", {"start": v(-49.37, -40.66) * mm, "mid": v(-49.53, -40.77) * mm, "end": v(-49.73, -40.81) * mm});
            skLineSegment(sketch, "E938", {"start": v(-52.11, -40.81) * mm, "end": v(-49.73, -40.81) * mm});
            skArc(sketch, "E939", {"start": v(-48.3, -41.72) * mm, "mid": v(-48.42, -41.89) * mm, "end": v(-48.46, -42.08) * mm});
            skLineSegment(sketch, "E940", {"start": v(-48.3, -41.72) * mm, "end": v(-44.77, -38.18) * mm});
            skArc(sketch, "E941", {"start": v(-44.62, -37.82) * mm, "mid": v(-44.66, -38.02) * mm, "end": v(-44.77, -38.18) * mm});
            skLineSegment(sketch, "E942", {"start": v(-44.62, -36.48) * mm, "end": v(-44.62, -37.82) * mm});
            skArc(sketch, "E943", {"start": v(-44.62, -36.48) * mm, "mid": v(-44.47, -36.12) * mm, "end": v(-44.1, -35.97) * mm});
            skLineSegment(sketch, "E944", {"start": v(-40.12, -35.97) * mm, "end": v(-44.1, -35.97) * mm});
            skArc(sketch, "E945", {"start": v(-39.6, -36.48) * mm, "mid": v(-39.76, -36.12) * mm, "end": v(-40.12, -35.97) * mm});
            skLineSegment(sketch, "E946", {"start": v(-39.6, -36.48) * mm, "end": v(-39.6, -37.82) * mm});
            skArc(sketch, "E947", {"start": v(-39.6, -37.82) * mm, "mid": v(-39.57, -38.02) * mm, "end": v(-39.46, -38.18) * mm});
            skLineSegment(sketch, "E948", {"start": v(-35.92, -41.72) * mm, "end": v(-39.46, -38.18) * mm});
            skArc(sketch, "E949", {"start": v(-35.77, -42.08) * mm, "mid": v(-35.8, -41.89) * mm, "end": v(-35.92, -41.72) * mm});
            skLineSegment(sketch, "E950", {"start": v(-35.77, -42.08) * mm, "end": v(-35.77, -46.85) * mm});
            skArc(sketch, "E951", {"start": v(-35.92, -47.21) * mm, "mid": v(-35.8, -47.05) * mm, "end": v(-35.77, -46.85) * mm});
            skLineSegment(sketch, "E952", {"start": v(-35.92, -47.21) * mm, "end": v(-39.46, -50.75) * mm});
            skArc(sketch, "E953", {"start": v(-39.46, -50.75) * mm, "mid": v(-39.57, -50.92) * mm, "end": v(-39.6, -51.11) * mm});
            skLineSegment(sketch, "E954", {"start": v(-39.6, -51.11) * mm, "end": v(-39.6, -52.46) * mm});
            skArc(sketch, "E955", {"start": v(-40.12, -52.97) * mm, "mid": v(-39.76, -52.82) * mm, "end": v(-39.6, -52.46) * mm});
            skLineSegment(sketch, "E956", {"start": v(-40.12, -52.97) * mm, "end": v(-44.1, -52.97) * mm});
            skArc(sketch, "E957", {"start": v(-44.1, -52.97) * mm, "mid": v(-44.47, -52.82) * mm, "end": v(-44.62, -52.46) * mm});
            skLineSegment(sketch, "E958", {"start": v(-44.62, -51.11) * mm, "end": v(-44.62, -52.46) * mm});
            skArc(sketch, "E959", {"start": v(-44.77, -50.75) * mm, "mid": v(-44.66, -50.92) * mm, "end": v(-44.62, -51.11) * mm});
            skLineSegment(sketch, "E960", {"start": v(-48.3, -47.21) * mm, "end": v(-44.77, -50.75) * mm});
            skArc(sketch, "E961", {"start": v(-48.3, -47.21) * mm, "mid": v(-48.42, -47.05) * mm, "end": v(-48.46, -46.85) * mm});
            skArc(sketch, "E962", {"start": v(-52.11, -42.37) * mm, "mid": v(-51.7, -42.41) * mm, "end": v(-51.3, -42.53) * mm});
            skArc(sketch, "E963", {"start": v(-51.3, -46.4) * mm, "mid": v(-51.7, -46.52) * mm, "end": v(-52.11, -46.56) * mm});
            skCircle(sketch, "E964", {"center": v(-84.56, -44.47) * mm, "radius": 4 * mm});
            skCircle(sketch, "E965", {"center": v(-19.66, -44.47) * mm, "radius": 4 * mm});
            skSolve(sketch);
        }
        {
            var Q0;
            Q0 = qSketchRegion(id + "F4", true);
            extrude(context, id + "F5", {"entities" : qUnion([Q0]), "depth" : 300 * mm, "offsetDistance" : 25 * mm});
        }
        {
            var Q0;
            Q0=qCreatedBy(makeId("Top.planeOp"),FACE);
            var sketch = newSketch(context, id + "F6", { "sketchPlane" : qUnion([Q0])});
            skLineSegment(sketch, "E966", {"start": v(-260.07, -134.62) * mm, "end": v(-260.07, -139.4) * mm});
            skLineSegment(sketch, "E967", {"start": v(-274.3, -134.7) * mm, "end": v(-274.11, -134.88) * mm});
            skArc(sketch, "E968", {"start": v(-257.22, -135.07) * mm, "mid": v(-256.83, -134.95) * mm, "end": v(-256.42, -134.91) * mm});
            skArc(sketch, "E969", {"start": v(-258.54, -134.7) * mm, "mid": v(-257.77, -134.5) * mm, "end": v(-257.22, -135.07) * mm});
            skLineSegment(sketch, "E970", {"start": v(-258.54, -134.7) * mm, "end": v(-258.72, -134.88) * mm});
            skArc(sketch, "E971", {"start": v(-258.35, -136.2) * mm, "mid": v(-258.92, -135.65) * mm, "end": v(-258.72, -134.88) * mm});
            skArc(sketch, "E972", {"start": v(-258.35, -137.81) * mm, "mid": v(-258.51, -137) * mm, "end": v(-258.35, -136.2) * mm});
            skArc(sketch, "E973", {"start": v(-258.72, -139.13) * mm, "mid": v(-258.92, -138.36) * mm, "end": v(-258.35, -137.81) * mm});
            skLineSegment(sketch, "E974", {"start": v(-258.72, -139.13) * mm, "end": v(-258.54, -139.31) * mm});
            skArc(sketch, "E975", {"start": v(-257.22, -138.94) * mm, "mid": v(-257.77, -139.51) * mm, "end": v(-258.54, -139.31) * mm});
            skArc(sketch, "E976", {"start": v(-256.42, -139.1) * mm, "mid": v(-256.83, -139.06) * mm, "end": v(-257.22, -138.94) * mm});
            skArc(sketch, "E977", {"start": v(-274.3, -134.7) * mm, "mid": v(-275.06, -134.5) * mm, "end": v(-275.61, -135.07) * mm});
            skArc(sketch, "E978", {"start": v(-275.61, -135.07) * mm, "mid": v(-276.42, -134.91) * mm, "end": v(-277.22, -135.07) * mm});
            skArc(sketch, "E979", {"start": v(-277.22, -135.07) * mm, "mid": v(-277.77, -134.5) * mm, "end": v(-278.54, -134.7) * mm});
            skLineSegment(sketch, "E980", {"start": v(-278.72, -134.88) * mm, "end": v(-278.54, -134.7) * mm});
            skArc(sketch, "E981", {"start": v(-278.72, -134.88) * mm, "mid": v(-278.92, -135.65) * mm, "end": v(-278.35, -136.2) * mm});
            skArc(sketch, "E982", {"start": v(-278.35, -136.2) * mm, "mid": v(-278.51, -137) * mm, "end": v(-278.35, -137.81) * mm});
            skArc(sketch, "E983", {"start": v(-278.35, -137.81) * mm, "mid": v(-278.92, -138.36) * mm, "end": v(-278.72, -139.13) * mm});
            skLineSegment(sketch, "E984", {"start": v(-278.54, -139.31) * mm, "end": v(-278.72, -139.13) * mm});
            skArc(sketch, "E985", {"start": v(-278.54, -139.31) * mm, "mid": v(-277.77, -139.51) * mm, "end": v(-277.22, -138.94) * mm});
            skArc(sketch, "E986", {"start": v(-277.22, -138.94) * mm, "mid": v(-276.42, -139.1) * mm, "end": v(-275.61, -138.94) * mm});
            skArc(sketch, "E987", {"start": v(-275.61, -138.94) * mm, "mid": v(-275.06, -139.51) * mm, "end": v(-274.3, -139.31) * mm});
            skLineSegment(sketch, "E988", {"start": v(-274.11, -139.13) * mm, "end": v(-274.3, -139.31) * mm});
            skArc(sketch, "E989", {"start": v(-274.11, -139.13) * mm, "mid": v(-273.91, -138.36) * mm, "end": v(-274.48, -137.81) * mm});
            skArc(sketch, "E990", {"start": v(-274.48, -137.81) * mm, "mid": v(-274.32, -137) * mm, "end": v(-274.48, -136.2) * mm});
            skArc(sketch, "E991", {"start": v(-274.48, -136.2) * mm, "mid": v(-273.91, -135.65) * mm, "end": v(-274.11, -134.88) * mm});
            skLineSegment(sketch, "E992", {"start": v(-256.42, -140.66) * mm, "end": v(-258.8, -140.66) * mm});
            skArc(sketch, "E993", {"start": v(-259.16, -140.81) * mm, "mid": v(-259, -140.7) * mm, "end": v(-258.8, -140.66) * mm});
            skLineSegment(sketch, "E994", {"start": v(-259.16, -140.81) * mm, "end": v(-262.26, -143.92) * mm});
            skArc(sketch, "E995", {"start": v(-262.41, -144.27) * mm, "mid": v(-262.37, -144.08) * mm, "end": v(-262.26, -143.92) * mm});
            skLineSegment(sketch, "E996", {"start": v(-262.41, -144.27) * mm, "end": v(-262.41, -145) * mm});
            skArc(sketch, "E997", {"start": v(-261.9, -145.5) * mm, "mid": v(-262.26, -145.36) * mm, "end": v(-262.41, -145) * mm});
            skLineSegment(sketch, "E998", {"start": v(-261.9, -145.5) * mm, "end": v(-259.55, -145.5) * mm});
            skArc(sketch, "E999", {"start": v(-259.55, -145.5) * mm, "mid": v(-259.2, -145.66) * mm, "end": v(-259.05, -146.02) * mm});
            skLineSegment(sketch, "E1000", {"start": v(-259.05, -146.5) * mm, "end": v(-259.05, -146.02) * mm});
            skArc(sketch, "E1001", {"start": v(-259.05, -146.5) * mm, "mid": v(-259.2, -146.86) * mm, "end": v(-259.55, -147) * mm});
            skLineSegment(sketch, "E1002", {"start": v(-273.28, -147) * mm, "end": v(-259.55, -147) * mm});
            skArc(sketch, "E1003", {"start": v(-273.79, -146.5) * mm, "mid": v(-273.64, -146.86) * mm, "end": v(-273.28, -147) * mm});
            skLineSegment(sketch, "E1004", {"start": v(-273.79, -146.5) * mm, "end": v(-273.79, -146.02) * mm});
            skArc(sketch, "E1005", {"start": v(-273.28, -145.5) * mm, "mid": v(-273.64, -145.66) * mm, "end": v(-273.79, -146.02) * mm});
            skLineSegment(sketch, "E1006", {"start": v(-270.93, -145.5) * mm, "end": v(-273.28, -145.5) * mm});
            skArc(sketch, "E1007", {"start": v(-270.93, -145.5) * mm, "mid": v(-270.57, -145.36) * mm, "end": v(-270.42, -145) * mm});
            skLineSegment(sketch, "E1008", {"start": v(-270.42, -144.27) * mm, "end": v(-270.42, -145) * mm});
            skArc(sketch, "E1009", {"start": v(-270.42, -144.27) * mm, "mid": v(-270.46, -144.08) * mm, "end": v(-270.57, -143.92) * mm});
            skLineSegment(sketch, "E1010", {"start": v(-273.67, -140.81) * mm, "end": v(-270.57, -143.92) * mm});
            skArc(sketch, "E1011", {"start": v(-273.67, -140.81) * mm, "mid": v(-273.84, -140.7) * mm, "end": v(-274.03, -140.66) * mm});
            skLineSegment(sketch, "E1012", {"start": v(-278.8, -140.66) * mm, "end": v(-274.03, -140.66) * mm});
            skArc(sketch, "E1013", {"start": v(-278.8, -140.66) * mm, "mid": v(-279, -140.7) * mm, "end": v(-279.16, -140.81) * mm});
            skLineSegment(sketch, "E1014", {"start": v(-282.26, -143.92) * mm, "end": v(-279.16, -140.81) * mm});
            skArc(sketch, "E1015", {"start": v(-282.26, -143.92) * mm, "mid": v(-282.37, -144.08) * mm, "end": v(-282.41, -144.27) * mm});
            skLineSegment(sketch, "E1016", {"start": v(-282.41, -144.27) * mm, "end": v(-282.41, -145) * mm});
            skArc(sketch, "E1017", {"start": v(-282.41, -145) * mm, "mid": v(-282.26, -145.36) * mm, "end": v(-281.9, -145.5) * mm});
            skLineSegment(sketch, "E1018", {"start": v(-279.55, -145.5) * mm, "end": v(-281.9, -145.5) * mm});
            skArc(sketch, "E1019", {"start": v(-279.05, -146.02) * mm, "mid": v(-279.2, -145.66) * mm, "end": v(-279.55, -145.5) * mm});
            skLineSegment(sketch, "E1020", {"start": v(-279.05, -146.02) * mm, "end": v(-279.05, -146.5) * mm});
            skArc(sketch, "E1021", {"start": v(-279.55, -147) * mm, "mid": v(-279.2, -146.86) * mm, "end": v(-279.05, -146.5) * mm});
            skLineSegment(sketch, "E1022", {"start": v(-284.92, -147) * mm, "end": v(-279.55, -147) * mm});
            skArc(sketch, "E1023", {"start": v(-286.42, -145.5) * mm, "mid": v(-285.98, -146.57) * mm, "end": v(-284.92, -147) * mm});
            skLineSegment(sketch, "E1024", {"start": v(-286.42, -145.5) * mm, "end": v(-286.42, -140.15) * mm});
            skArc(sketch, "E1025", {"start": v(-285.9, -139.64) * mm, "mid": v(-286.27, -139.79) * mm, "end": v(-286.42, -140.15) * mm});
            skLineSegment(sketch, "E1026", {"start": v(-285.9, -139.64) * mm, "end": v(-285.42, -139.64) * mm});
            skArc(sketch, "E1027", {"start": v(-284.92, -140.15) * mm, "mid": v(-285.07, -139.79) * mm, "end": v(-285.42, -139.64) * mm});
            skLineSegment(sketch, "E1028", {"start": v(-284.92, -142.5) * mm, "end": v(-284.92, -140.15) * mm});
            skArc(sketch, "E1029", {"start": v(-284.92, -142.5) * mm, "mid": v(-284.77, -142.85) * mm, "end": v(-284.4, -143) * mm});
            skLineSegment(sketch, "E1030", {"start": v(-283.68, -143) * mm, "end": v(-284.4, -143) * mm});
            skArc(sketch, "E1031", {"start": v(-283.68, -143) * mm, "mid": v(-283.49, -142.96) * mm, "end": v(-283.32, -142.85) * mm});
            skLineSegment(sketch, "E1032", {"start": v(-280.22, -139.75) * mm, "end": v(-283.32, -142.85) * mm});
            skArc(sketch, "E1033", {"start": v(-280.22, -139.75) * mm, "mid": v(-280.11, -139.59) * mm, "end": v(-280.07, -139.4) * mm});
            skLineSegment(sketch, "E1034", {"start": v(-280.07, -134.62) * mm, "end": v(-280.07, -139.4) * mm});
            skArc(sketch, "E1035", {"start": v(-280.07, -134.62) * mm, "mid": v(-280.11, -134.43) * mm, "end": v(-280.22, -134.27) * mm});
            skLineSegment(sketch, "E1036", {"start": v(-280.22, -134.27) * mm, "end": v(-283.32, -131.16) * mm});
            skArc(sketch, "E1037", {"start": v(-283.32, -131.16) * mm, "mid": v(-283.49, -131.05) * mm, "end": v(-283.68, -131.01) * mm});
            skLineSegment(sketch, "E1038", {"start": v(-283.68, -131.01) * mm, "end": v(-284.4, -131.01) * mm});
            skArc(sketch, "E1039", {"start": v(-284.4, -131.01) * mm, "mid": v(-284.77, -131.16) * mm, "end": v(-284.92, -131.52) * mm});
            skLineSegment(sketch, "E1040", {"start": v(-284.92, -131.52) * mm, "end": v(-284.92, -133.87) * mm});
            skArc(sketch, "E1041", {"start": v(-285.42, -134.38) * mm, "mid": v(-285.07, -134.23) * mm, "end": v(-284.92, -133.87) * mm});
            skLineSegment(sketch, "E1042", {"start": v(-285.42, -134.38) * mm, "end": v(-285.9, -134.38) * mm});
            skArc(sketch, "E1043", {"start": v(-286.42, -133.87) * mm, "mid": v(-286.27, -134.23) * mm, "end": v(-285.9, -134.38) * mm});
            skLineSegment(sketch, "E1044", {"start": v(-286.42, -133.87) * mm, "end": v(-286.42, -128.5) * mm});
            skArc(sketch, "E1045", {"start": v(-284.92, -127) * mm, "mid": v(-285.98, -127.45) * mm, "end": v(-286.42, -128.5) * mm});
            skLineSegment(sketch, "E1046", {"start": v(-284.92, -127) * mm, "end": v(-279.55, -127) * mm});
            skArc(sketch, "E1047", {"start": v(-279.05, -127.52) * mm, "mid": v(-279.2, -127.16) * mm, "end": v(-279.55, -127) * mm});
            skLineSegment(sketch, "E1048", {"start": v(-279.05, -127.52) * mm, "end": v(-279.05, -128) * mm});
            skArc(sketch, "E1049", {"start": v(-279.55, -128.5) * mm, "mid": v(-279.2, -128.36) * mm, "end": v(-279.05, -128) * mm});
            skLineSegment(sketch, "E1050", {"start": v(-279.55, -128.5) * mm, "end": v(-281.9, -128.5) * mm});
            skArc(sketch, "E1051", {"start": v(-281.9, -128.5) * mm, "mid": v(-282.26, -128.66) * mm, "end": v(-282.41, -129.02) * mm});
            skLineSegment(sketch, "E1052", {"start": v(-282.41, -129.02) * mm, "end": v(-282.41, -129.74) * mm});
            skArc(sketch, "E1053", {"start": v(-282.41, -129.74) * mm, "mid": v(-282.37, -129.94) * mm, "end": v(-282.26, -130.1) * mm});
            skLineSegment(sketch, "E1054", {"start": v(-282.26, -130.1) * mm, "end": v(-279.16, -133.2) * mm});
            skArc(sketch, "E1055", {"start": v(-279.16, -133.2) * mm, "mid": v(-279, -133.31) * mm, "end": v(-278.8, -133.35) * mm});
            skLineSegment(sketch, "E1056", {"start": v(-278.8, -133.35) * mm, "end": v(-274.03, -133.35) * mm});
            skArc(sketch, "E1057", {"start": v(-274.03, -133.35) * mm, "mid": v(-273.84, -133.31) * mm, "end": v(-273.67, -133.2) * mm});
            skLineSegment(sketch, "E1058", {"start": v(-273.67, -133.2) * mm, "end": v(-270.57, -130.1) * mm});
            skArc(sketch, "E1059", {"start": v(-270.57, -130.1) * mm, "mid": v(-270.46, -129.94) * mm, "end": v(-270.42, -129.74) * mm});
            skLineSegment(sketch, "E1060", {"start": v(-270.42, -129.02) * mm, "end": v(-270.42, -129.74) * mm});
            skArc(sketch, "E1061", {"start": v(-270.42, -129.02) * mm, "mid": v(-270.57, -128.66) * mm, "end": v(-270.93, -128.5) * mm});
            skLineSegment(sketch, "E1062", {"start": v(-270.93, -128.5) * mm, "end": v(-273.28, -128.5) * mm});
            skArc(sketch, "E1063", {"start": v(-273.79, -128) * mm, "mid": v(-273.64, -128.36) * mm, "end": v(-273.28, -128.5) * mm});
            skLineSegment(sketch, "E1064", {"start": v(-273.79, -128) * mm, "end": v(-273.79, -127.52) * mm});
            skArc(sketch, "E1065", {"start": v(-273.28, -127) * mm, "mid": v(-273.64, -127.16) * mm, "end": v(-273.79, -127.52) * mm});
            skLineSegment(sketch, "E1066", {"start": v(-259.55, -127) * mm, "end": v(-273.28, -127) * mm});
            skArc(sketch, "E1067", {"start": v(-259.55, -127) * mm, "mid": v(-259.2, -127.16) * mm, "end": v(-259.05, -127.52) * mm});
            skLineSegment(sketch, "E1068", {"start": v(-259.05, -128) * mm, "end": v(-259.05, -127.52) * mm});
            skArc(sketch, "E1069", {"start": v(-259.05, -128) * mm, "mid": v(-259.2, -128.36) * mm, "end": v(-259.55, -128.5) * mm});
            skLineSegment(sketch, "E1070", {"start": v(-261.9, -128.5) * mm, "end": v(-259.55, -128.5) * mm});
            skArc(sketch, "E1071", {"start": v(-262.41, -129.02) * mm, "mid": v(-262.26, -128.66) * mm, "end": v(-261.9, -128.5) * mm});
            skLineSegment(sketch, "E1072", {"start": v(-262.41, -129.02) * mm, "end": v(-262.41, -129.74) * mm});
            skArc(sketch, "E1073", {"start": v(-262.26, -130.1) * mm, "mid": v(-262.37, -129.94) * mm, "end": v(-262.41, -129.74) * mm});
            skLineSegment(sketch, "E1074", {"start": v(-259.16, -133.2) * mm, "end": v(-262.26, -130.1) * mm});
            skArc(sketch, "E1075", {"start": v(-258.8, -133.35) * mm, "mid": v(-259, -133.31) * mm, "end": v(-259.16, -133.2) * mm});
            skLineSegment(sketch, "E1076", {"start": v(-256.42, -133.35) * mm, "end": v(-258.8, -133.35) * mm});
            skArc(sketch, "E1077", {"start": v(-260.07, -134.62) * mm, "mid": v(-260.11, -134.43) * mm, "end": v(-260.22, -134.27) * mm});
            skLineSegment(sketch, "E1078", {"start": v(-260.22, -134.27) * mm, "end": v(-263.76, -130.72) * mm});
            skArc(sketch, "E1079", {"start": v(-263.76, -130.72) * mm, "mid": v(-263.87, -130.56) * mm, "end": v(-263.91, -130.36) * mm});
            skLineSegment(sketch, "E1080", {"start": v(-263.91, -129.02) * mm, "end": v(-263.91, -130.36) * mm});
            skArc(sketch, "E1081", {"start": v(-264.42, -128.5) * mm, "mid": v(-264.06, -128.66) * mm, "end": v(-263.91, -129.02) * mm});
            skLineSegment(sketch, "E1082", {"start": v(-268.41, -128.5) * mm, "end": v(-264.42, -128.5) * mm});
            skArc(sketch, "E1083", {"start": v(-268.41, -128.5) * mm, "mid": v(-268.77, -128.66) * mm, "end": v(-268.92, -129.02) * mm});
            skLineSegment(sketch, "E1084", {"start": v(-268.92, -129.02) * mm, "end": v(-268.92, -130.36) * mm});
            skArc(sketch, "E1085", {"start": v(-269.07, -130.72) * mm, "mid": v(-268.96, -130.56) * mm, "end": v(-268.92, -130.36) * mm});
            skLineSegment(sketch, "E1086", {"start": v(-272.61, -134.27) * mm, "end": v(-269.07, -130.72) * mm});
            skArc(sketch, "E1087", {"start": v(-272.61, -134.27) * mm, "mid": v(-272.72, -134.43) * mm, "end": v(-272.76, -134.62) * mm});
            skLineSegment(sketch, "E1088", {"start": v(-272.76, -134.62) * mm, "end": v(-272.76, -139.4) * mm});
            skArc(sketch, "E1089", {"start": v(-272.76, -139.4) * mm, "mid": v(-272.72, -139.59) * mm, "end": v(-272.61, -139.75) * mm});
            skLineSegment(sketch, "E1090", {"start": v(-272.61, -139.75) * mm, "end": v(-269.07, -143.3) * mm});
            skArc(sketch, "E1091", {"start": v(-268.92, -143.65) * mm, "mid": v(-268.96, -143.46) * mm, "end": v(-269.07, -143.3) * mm});
            skLineSegment(sketch, "E1092", {"start": v(-268.92, -143.65) * mm, "end": v(-268.92, -145) * mm});
            skArc(sketch, "E1093", {"start": v(-268.92, -145) * mm, "mid": v(-268.77, -145.36) * mm, "end": v(-268.41, -145.5) * mm});
            skLineSegment(sketch, "E1094", {"start": v(-268.41, -145.5) * mm, "end": v(-264.42, -145.5) * mm});
            skArc(sketch, "E1095", {"start": v(-263.91, -145) * mm, "mid": v(-264.06, -145.36) * mm, "end": v(-264.42, -145.5) * mm});
            skLineSegment(sketch, "E1096", {"start": v(-263.91, -143.65) * mm, "end": v(-263.91, -145) * mm});
            skArc(sketch, "E1097", {"start": v(-263.91, -143.65) * mm, "mid": v(-263.87, -143.46) * mm, "end": v(-263.76, -143.3) * mm});
            skLineSegment(sketch, "E1098", {"start": v(-260.22, -139.75) * mm, "end": v(-263.76, -143.3) * mm});
            skArc(sketch, "E1099", {"start": v(-260.07, -139.4) * mm, "mid": v(-260.11, -139.59) * mm, "end": v(-260.22, -139.75) * mm});
            skLineSegment(sketch, "E1100", {"start": v(-252.76, -134.62) * mm, "end": v(-252.76, -139.4) * mm});
            skLineSegment(sketch, "E1101", {"start": v(-238.54, -134.7) * mm, "end": v(-238.72, -134.88) * mm});
            skArc(sketch, "E1102", {"start": v(-255.61, -135.07) * mm, "mid": v(-255.06, -134.5) * mm, "end": v(-254.3, -134.7) * mm});
            skLineSegment(sketch, "E1103", {"start": v(-254.3, -134.7) * mm, "end": v(-254.11, -134.88) * mm});
            skArc(sketch, "E1104", {"start": v(-254.11, -134.88) * mm, "mid": v(-253.91, -135.65) * mm, "end": v(-254.48, -136.2) * mm});
            skArc(sketch, "E1105", {"start": v(-254.48, -136.2) * mm, "mid": v(-254.32, -137) * mm, "end": v(-254.48, -137.81) * mm});
            skArc(sketch, "E1106", {"start": v(-254.48, -137.81) * mm, "mid": v(-253.91, -138.36) * mm, "end": v(-254.11, -139.13) * mm});
            skLineSegment(sketch, "E1107", {"start": v(-254.11, -139.13) * mm, "end": v(-254.3, -139.31) * mm});
            skArc(sketch, "E1108", {"start": v(-254.3, -139.31) * mm, "mid": v(-255.06, -139.51) * mm, "end": v(-255.61, -138.94) * mm});
            skArc(sketch, "E1109", {"start": v(-237.22, -135.07) * mm, "mid": v(-237.77, -134.5) * mm, "end": v(-238.54, -134.7) * mm});
            skArc(sketch, "E1110", {"start": v(-235.61, -135.07) * mm, "mid": v(-236.42, -134.91) * mm, "end": v(-237.22, -135.07) * mm});
            skArc(sketch, "E1111", {"start": v(-234.3, -134.7) * mm, "mid": v(-235.06, -134.5) * mm, "end": v(-235.61, -135.07) * mm});
            skLineSegment(sketch, "E1112", {"start": v(-234.11, -134.88) * mm, "end": v(-234.3, -134.7) * mm});
            skArc(sketch, "E1113", {"start": v(-234.48, -136.2) * mm, "mid": v(-233.91, -135.65) * mm, "end": v(-234.11, -134.88) * mm});
            skArc(sketch, "E1114", {"start": v(-234.48, -137.81) * mm, "mid": v(-234.32, -137) * mm, "end": v(-234.48, -136.2) * mm});
            skArc(sketch, "E1115", {"start": v(-234.11, -139.13) * mm, "mid": v(-233.91, -138.36) * mm, "end": v(-234.48, -137.81) * mm});
            skLineSegment(sketch, "E1116", {"start": v(-234.3, -139.31) * mm, "end": v(-234.11, -139.13) * mm});
            skArc(sketch, "E1117", {"start": v(-235.61, -138.94) * mm, "mid": v(-235.06, -139.51) * mm, "end": v(-234.3, -139.31) * mm});
            skArc(sketch, "E1118", {"start": v(-237.22, -138.94) * mm, "mid": v(-236.42, -139.1) * mm, "end": v(-235.61, -138.94) * mm});
            skArc(sketch, "E1119", {"start": v(-238.54, -139.31) * mm, "mid": v(-237.77, -139.51) * mm, "end": v(-237.22, -138.94) * mm});
            skLineSegment(sketch, "E1120", {"start": v(-238.72, -139.13) * mm, "end": v(-238.54, -139.31) * mm});
            skArc(sketch, "E1121", {"start": v(-238.35, -137.81) * mm, "mid": v(-238.92, -138.36) * mm, "end": v(-238.72, -139.13) * mm});
            skArc(sketch, "E1122", {"start": v(-238.35, -136.2) * mm, "mid": v(-238.51, -137) * mm, "end": v(-238.35, -137.81) * mm});
            skArc(sketch, "E1123", {"start": v(-238.72, -134.88) * mm, "mid": v(-238.92, -135.65) * mm, "end": v(-238.35, -136.2) * mm});
            skLineSegment(sketch, "E1124", {"start": v(-256.42, -140.66) * mm, "end": v(-254.03, -140.66) * mm});
            skArc(sketch, "E1125", {"start": v(-254.03, -140.66) * mm, "mid": v(-253.84, -140.7) * mm, "end": v(-253.67, -140.81) * mm});
            skLineSegment(sketch, "E1126", {"start": v(-253.67, -140.81) * mm, "end": v(-250.57, -143.92) * mm});
            skArc(sketch, "E1127", {"start": v(-250.57, -143.92) * mm, "mid": v(-250.46, -144.08) * mm, "end": v(-250.42, -144.27) * mm});
            skLineSegment(sketch, "E1128", {"start": v(-250.42, -144.27) * mm, "end": v(-250.42, -145) * mm});
            skArc(sketch, "E1129", {"start": v(-250.42, -145) * mm, "mid": v(-250.57, -145.36) * mm, "end": v(-250.93, -145.5) * mm});
            skLineSegment(sketch, "E1130", {"start": v(-250.93, -145.5) * mm, "end": v(-253.28, -145.5) * mm});
            skArc(sketch, "E1131", {"start": v(-253.79, -146.02) * mm, "mid": v(-253.64, -145.66) * mm, "end": v(-253.28, -145.5) * mm});
            skLineSegment(sketch, "E1132", {"start": v(-253.79, -146.5) * mm, "end": v(-253.79, -146.02) * mm});
            skArc(sketch, "E1133", {"start": v(-253.28, -147) * mm, "mid": v(-253.64, -146.86) * mm, "end": v(-253.79, -146.5) * mm});
            skLineSegment(sketch, "E1134", {"start": v(-239.55, -147) * mm, "end": v(-253.28, -147) * mm});
            skArc(sketch, "E1135", {"start": v(-239.55, -147) * mm, "mid": v(-239.2, -146.86) * mm, "end": v(-239.05, -146.5) * mm});
            skLineSegment(sketch, "E1136", {"start": v(-239.05, -146.5) * mm, "end": v(-239.05, -146.02) * mm});
            skArc(sketch, "E1137", {"start": v(-239.05, -146.02) * mm, "mid": v(-239.2, -145.66) * mm, "end": v(-239.55, -145.5) * mm});
            skLineSegment(sketch, "E1138", {"start": v(-241.9, -145.5) * mm, "end": v(-239.55, -145.5) * mm});
            skArc(sketch, "E1139", {"start": v(-242.41, -145) * mm, "mid": v(-242.26, -145.36) * mm, "end": v(-241.9, -145.5) * mm});
            skLineSegment(sketch, "E1140", {"start": v(-242.41, -144.27) * mm, "end": v(-242.41, -145) * mm});
            skArc(sketch, "E1141", {"start": v(-242.26, -143.92) * mm, "mid": v(-242.37, -144.08) * mm, "end": v(-242.41, -144.27) * mm});
            skLineSegment(sketch, "E1142", {"start": v(-239.16, -140.81) * mm, "end": v(-242.26, -143.92) * mm});
            skArc(sketch, "E1143", {"start": v(-238.8, -140.66) * mm, "mid": v(-239, -140.7) * mm, "end": v(-239.16, -140.81) * mm});
            skLineSegment(sketch, "E1144", {"start": v(-234.03, -140.66) * mm, "end": v(-238.8, -140.66) * mm});
            skArc(sketch, "E1145", {"start": v(-233.67, -140.81) * mm, "mid": v(-233.84, -140.7) * mm, "end": v(-234.03, -140.66) * mm});
            skLineSegment(sketch, "E1146", {"start": v(-230.57, -143.92) * mm, "end": v(-233.67, -140.81) * mm});
            skArc(sketch, "E1147", {"start": v(-230.42, -144.27) * mm, "mid": v(-230.46, -144.08) * mm, "end": v(-230.57, -143.92) * mm});
            skLineSegment(sketch, "E1148", {"start": v(-230.42, -144.27) * mm, "end": v(-230.42, -145) * mm});
            skArc(sketch, "E1149", {"start": v(-230.93, -145.5) * mm, "mid": v(-230.57, -145.36) * mm, "end": v(-230.42, -145) * mm});
            skLineSegment(sketch, "E1150", {"start": v(-233.28, -145.5) * mm, "end": v(-230.93, -145.5) * mm});
            skArc(sketch, "E1151", {"start": v(-233.28, -145.5) * mm, "mid": v(-233.64, -145.66) * mm, "end": v(-233.79, -146.02) * mm});
            skLineSegment(sketch, "E1152", {"start": v(-233.79, -146.02) * mm, "end": v(-233.79, -146.5) * mm});
            skArc(sketch, "E1153", {"start": v(-233.79, -146.5) * mm, "mid": v(-233.64, -146.86) * mm, "end": v(-233.28, -147) * mm});
            skLineSegment(sketch, "E1154", {"start": v(-227.92, -147) * mm, "end": v(-233.28, -147) * mm});
            skArc(sketch, "E1155", {"start": v(-227.92, -147) * mm, "mid": v(-226.86, -146.57) * mm, "end": v(-226.42, -145.5) * mm});
            skLineSegment(sketch, "E1156", {"start": v(-226.42, -145.5) * mm, "end": v(-226.42, -140.15) * mm});
            skArc(sketch, "E1157", {"start": v(-226.42, -140.15) * mm, "mid": v(-226.57, -139.79) * mm, "end": v(-226.92, -139.64) * mm});
            skLineSegment(sketch, "E1158", {"start": v(-226.92, -139.64) * mm, "end": v(-227.4, -139.64) * mm});
            skArc(sketch, "E1159", {"start": v(-227.4, -139.64) * mm, "mid": v(-227.77, -139.79) * mm, "end": v(-227.92, -140.15) * mm});
            skLineSegment(sketch, "E1160", {"start": v(-227.92, -142.5) * mm, "end": v(-227.92, -140.15) * mm});
            skArc(sketch, "E1161", {"start": v(-228.42, -143) * mm, "mid": v(-228.07, -142.85) * mm, "end": v(-227.92, -142.5) * mm});
            skLineSegment(sketch, "E1162", {"start": v(-229.15, -143) * mm, "end": v(-228.42, -143) * mm});
            skArc(sketch, "E1163", {"start": v(-229.5, -142.85) * mm, "mid": v(-229.34, -142.96) * mm, "end": v(-229.15, -143) * mm});
            skLineSegment(sketch, "E1164", {"start": v(-232.61, -139.75) * mm, "end": v(-229.5, -142.85) * mm});
            skArc(sketch, "E1165", {"start": v(-232.76, -139.4) * mm, "mid": v(-232.72, -139.59) * mm, "end": v(-232.61, -139.75) * mm});
            skLineSegment(sketch, "E1166", {"start": v(-232.76, -134.62) * mm, "end": v(-232.76, -139.4) * mm});
            skArc(sketch, "E1167", {"start": v(-232.61, -134.27) * mm, "mid": v(-232.72, -134.43) * mm, "end": v(-232.76, -134.62) * mm});
            skLineSegment(sketch, "E1168", {"start": v(-232.61, -134.27) * mm, "end": v(-229.5, -131.16) * mm});
            skArc(sketch, "E1169", {"start": v(-229.15, -131.01) * mm, "mid": v(-229.34, -131.05) * mm, "end": v(-229.5, -131.16) * mm});
            skLineSegment(sketch, "E1170", {"start": v(-229.15, -131.01) * mm, "end": v(-228.42, -131.01) * mm});
            skArc(sketch, "E1171", {"start": v(-227.92, -131.52) * mm, "mid": v(-228.07, -131.16) * mm, "end": v(-228.42, -131.01) * mm});
            skLineSegment(sketch, "E1172", {"start": v(-227.92, -131.52) * mm, "end": v(-227.92, -133.87) * mm});
            skArc(sketch, "E1173", {"start": v(-227.92, -133.87) * mm, "mid": v(-227.77, -134.23) * mm, "end": v(-227.4, -134.38) * mm});
            skLineSegment(sketch, "E1174", {"start": v(-227.4, -134.38) * mm, "end": v(-226.92, -134.38) * mm});
            skArc(sketch, "E1175", {"start": v(-226.92, -134.38) * mm, "mid": v(-226.57, -134.23) * mm, "end": v(-226.42, -133.87) * mm});
            skLineSegment(sketch, "E1176", {"start": v(-226.42, -133.87) * mm, "end": v(-226.42, -128.5) * mm});
            skArc(sketch, "E1177", {"start": v(-226.42, -128.5) * mm, "mid": v(-226.86, -127.45) * mm, "end": v(-227.92, -127) * mm});
            skLineSegment(sketch, "E1178", {"start": v(-227.92, -127) * mm, "end": v(-233.28, -127) * mm});
            skArc(sketch, "E1179", {"start": v(-233.28, -127) * mm, "mid": v(-233.64, -127.16) * mm, "end": v(-233.79, -127.52) * mm});
            skLineSegment(sketch, "E1180", {"start": v(-233.79, -127.52) * mm, "end": v(-233.79, -128) * mm});
            skArc(sketch, "E1181", {"start": v(-233.79, -128) * mm, "mid": v(-233.64, -128.36) * mm, "end": v(-233.28, -128.5) * mm});
            skLineSegment(sketch, "E1182", {"start": v(-233.28, -128.5) * mm, "end": v(-230.93, -128.5) * mm});
            skArc(sketch, "E1183", {"start": v(-230.42, -129.02) * mm, "mid": v(-230.57, -128.66) * mm, "end": v(-230.93, -128.5) * mm});
            skLineSegment(sketch, "E1184", {"start": v(-230.42, -129.02) * mm, "end": v(-230.42, -129.74) * mm});
            skArc(sketch, "E1185", {"start": v(-230.57, -130.1) * mm, "mid": v(-230.46, -129.94) * mm, "end": v(-230.42, -129.74) * mm});
            skLineSegment(sketch, "E1186", {"start": v(-230.57, -130.1) * mm, "end": v(-233.67, -133.2) * mm});
            skArc(sketch, "E1187", {"start": v(-234.03, -133.35) * mm, "mid": v(-233.84, -133.31) * mm, "end": v(-233.67, -133.2) * mm});
            skLineSegment(sketch, "E1188", {"start": v(-234.03, -133.35) * mm, "end": v(-238.8, -133.35) * mm});
            skArc(sketch, "E1189", {"start": v(-239.16, -133.2) * mm, "mid": v(-239, -133.31) * mm, "end": v(-238.8, -133.35) * mm});
            skLineSegment(sketch, "E1190", {"start": v(-239.16, -133.2) * mm, "end": v(-242.26, -130.1) * mm});
            skArc(sketch, "E1191", {"start": v(-242.41, -129.74) * mm, "mid": v(-242.37, -129.94) * mm, "end": v(-242.26, -130.1) * mm});
            skLineSegment(sketch, "E1192", {"start": v(-242.41, -129.02) * mm, "end": v(-242.41, -129.74) * mm});
            skArc(sketch, "E1193", {"start": v(-241.9, -128.5) * mm, "mid": v(-242.26, -128.66) * mm, "end": v(-242.41, -129.02) * mm});
            skLineSegment(sketch, "E1194", {"start": v(-241.9, -128.5) * mm, "end": v(-239.55, -128.5) * mm});
            skArc(sketch, "E1195", {"start": v(-239.55, -128.5) * mm, "mid": v(-239.2, -128.36) * mm, "end": v(-239.05, -128) * mm});
            skLineSegment(sketch, "E1196", {"start": v(-239.05, -128) * mm, "end": v(-239.05, -127.52) * mm});
            skArc(sketch, "E1197", {"start": v(-239.05, -127.52) * mm, "mid": v(-239.2, -127.16) * mm, "end": v(-239.55, -127) * mm});
            skLineSegment(sketch, "E1198", {"start": v(-253.28, -127) * mm, "end": v(-239.55, -127) * mm});
            skArc(sketch, "E1199", {"start": v(-253.79, -127.52) * mm, "mid": v(-253.64, -127.16) * mm, "end": v(-253.28, -127) * mm});
            skLineSegment(sketch, "E1200", {"start": v(-253.79, -128) * mm, "end": v(-253.79, -127.52) * mm});
            skArc(sketch, "E1201", {"start": v(-253.28, -128.5) * mm, "mid": v(-253.64, -128.36) * mm, "end": v(-253.79, -128) * mm});
            skLineSegment(sketch, "E1202", {"start": v(-250.93, -128.5) * mm, "end": v(-253.28, -128.5) * mm});
            skArc(sketch, "E1203", {"start": v(-250.93, -128.5) * mm, "mid": v(-250.57, -128.66) * mm, "end": v(-250.42, -129.02) * mm});
            skLineSegment(sketch, "E1204", {"start": v(-250.42, -129.02) * mm, "end": v(-250.42, -129.74) * mm});
            skArc(sketch, "E1205", {"start": v(-250.42, -129.74) * mm, "mid": v(-250.46, -129.94) * mm, "end": v(-250.57, -130.1) * mm});
            skLineSegment(sketch, "E1206", {"start": v(-253.67, -133.2) * mm, "end": v(-250.57, -130.1) * mm});
            skArc(sketch, "E1207", {"start": v(-253.67, -133.2) * mm, "mid": v(-253.84, -133.31) * mm, "end": v(-254.03, -133.35) * mm});
            skLineSegment(sketch, "E1208", {"start": v(-256.42, -133.35) * mm, "end": v(-254.03, -133.35) * mm});
            skArc(sketch, "E1209", {"start": v(-252.61, -134.27) * mm, "mid": v(-252.72, -134.43) * mm, "end": v(-252.76, -134.62) * mm});
            skLineSegment(sketch, "E1210", {"start": v(-252.61, -134.27) * mm, "end": v(-249.07, -130.72) * mm});
            skArc(sketch, "E1211", {"start": v(-248.92, -130.36) * mm, "mid": v(-248.96, -130.56) * mm, "end": v(-249.07, -130.72) * mm});
            skLineSegment(sketch, "E1212", {"start": v(-248.92, -129.02) * mm, "end": v(-248.92, -130.36) * mm});
            skArc(sketch, "E1213", {"start": v(-248.92, -129.02) * mm, "mid": v(-248.77, -128.66) * mm, "end": v(-248.41, -128.5) * mm});
            skLineSegment(sketch, "E1214", {"start": v(-244.42, -128.5) * mm, "end": v(-248.41, -128.5) * mm});
            skArc(sketch, "E1215", {"start": v(-243.91, -129.02) * mm, "mid": v(-244.06, -128.66) * mm, "end": v(-244.42, -128.5) * mm});
            skLineSegment(sketch, "E1216", {"start": v(-243.91, -129.02) * mm, "end": v(-243.91, -130.36) * mm});
            skArc(sketch, "E1217", {"start": v(-243.91, -130.36) * mm, "mid": v(-243.87, -130.56) * mm, "end": v(-243.76, -130.72) * mm});
            skLineSegment(sketch, "E1218", {"start": v(-240.22, -134.27) * mm, "end": v(-243.76, -130.72) * mm});
            skArc(sketch, "E1219", {"start": v(-240.07, -134.62) * mm, "mid": v(-240.11, -134.43) * mm, "end": v(-240.22, -134.27) * mm});
            skLineSegment(sketch, "E1220", {"start": v(-240.07, -134.62) * mm, "end": v(-240.07, -139.4) * mm});
            skArc(sketch, "E1221", {"start": v(-240.22, -139.75) * mm, "mid": v(-240.11, -139.59) * mm, "end": v(-240.07, -139.4) * mm});
            skLineSegment(sketch, "E1222", {"start": v(-240.22, -139.75) * mm, "end": v(-243.76, -143.3) * mm});
            skArc(sketch, "E1223", {"start": v(-243.76, -143.3) * mm, "mid": v(-243.87, -143.46) * mm, "end": v(-243.91, -143.65) * mm});
            skLineSegment(sketch, "E1224", {"start": v(-243.91, -143.65) * mm, "end": v(-243.91, -145) * mm});
            skArc(sketch, "E1225", {"start": v(-244.42, -145.5) * mm, "mid": v(-244.06, -145.36) * mm, "end": v(-243.91, -145) * mm});
            skLineSegment(sketch, "E1226", {"start": v(-244.42, -145.5) * mm, "end": v(-248.41, -145.5) * mm});
            skArc(sketch, "E1227", {"start": v(-248.41, -145.5) * mm, "mid": v(-248.77, -145.36) * mm, "end": v(-248.92, -145) * mm});
            skLineSegment(sketch, "E1228", {"start": v(-248.92, -143.65) * mm, "end": v(-248.92, -145) * mm});
            skArc(sketch, "E1229", {"start": v(-249.07, -143.3) * mm, "mid": v(-248.96, -143.46) * mm, "end": v(-248.92, -143.65) * mm});
            skLineSegment(sketch, "E1230", {"start": v(-252.61, -139.75) * mm, "end": v(-249.07, -143.3) * mm});
            skArc(sketch, "E1231", {"start": v(-252.61, -139.75) * mm, "mid": v(-252.72, -139.59) * mm, "end": v(-252.76, -139.4) * mm});
            skArc(sketch, "E1232", {"start": v(-256.42, -134.91) * mm, "mid": v(-256, -134.95) * mm, "end": v(-255.61, -135.07) * mm});
            skArc(sketch, "E1233", {"start": v(-255.61, -138.94) * mm, "mid": v(-256, -139.06) * mm, "end": v(-256.42, -139.1) * mm});
            skCircle(sketch, "E1234", {"center": v(-288.87, -137) * mm, "radius": 4 * mm});
            skCircle(sketch, "E1235", {"center": v(-223.97, -137) * mm, "radius": 4 * mm});
            skSolve(sketch);
        }
        {
            var Q0;
            Q0 = qSketchRegion(id + "F6", true);
            extrude(context, id + "F7", {"entities" : qUnion([Q0]), "depth" : 1200 * mm, "offsetDistance" : 25 * mm});
        }
        {
            var Q0;
            Q0=qCreatedBy(makeId("Top.planeOp"),FACE);
            var sketch = newSketch(context, id + "F8", { "sketchPlane" : qUnion([Q0])});
            skLineSegment(sketch, "E1236", {"start": v(-13.65, -112.62) * mm, "end": v(-13.65, -117.38) * mm});
            skLineSegment(sketch, "E1237", {"start": v(-27.88, -112.7) * mm, "end": v(-27.7, -112.88) * mm});
            skArc(sketch, "E1238", {"start": v(-10.8, -113.06) * mm, "mid": v(-10.4, -112.94) * mm, "end": v(-10, -112.9) * mm});
            skArc(sketch, "E1239", {"start": v(-12.12, -112.7) * mm, "mid": v(-11.36, -112.5) * mm, "end": v(-10.8, -113.06) * mm});
            skLineSegment(sketch, "E1240", {"start": v(-12.12, -112.7) * mm, "end": v(-12.3, -112.88) * mm});
            skArc(sketch, "E1241", {"start": v(-11.94, -114.2) * mm, "mid": v(-12.5, -113.64) * mm, "end": v(-12.3, -112.88) * mm});
            skArc(sketch, "E1242", {"start": v(-11.94, -115.8) * mm, "mid": v(-12.1, -115) * mm, "end": v(-11.94, -114.2) * mm});
            skArc(sketch, "E1243", {"start": v(-12.3, -117.12) * mm, "mid": v(-12.5, -116.36) * mm, "end": v(-11.94, -115.8) * mm});
            skLineSegment(sketch, "E1244", {"start": v(-12.3, -117.12) * mm, "end": v(-12.12, -117.3) * mm});
            skArc(sketch, "E1245", {"start": v(-10.8, -116.94) * mm, "mid": v(-11.36, -117.5) * mm, "end": v(-12.12, -117.3) * mm});
            skArc(sketch, "E1246", {"start": v(-10, -117.1) * mm, "mid": v(-10.4, -117.06) * mm, "end": v(-10.8, -116.94) * mm});
            skArc(sketch, "E1247", {"start": v(-27.88, -112.7) * mm, "mid": v(-28.64, -112.5) * mm, "end": v(-29.2, -113.06) * mm});
            skArc(sketch, "E1248", {"start": v(-29.2, -113.06) * mm, "mid": v(-30, -112.9) * mm, "end": v(-30.8, -113.06) * mm});
            skArc(sketch, "E1249", {"start": v(-30.8, -113.06) * mm, "mid": v(-31.36, -112.5) * mm, "end": v(-32.12, -112.7) * mm});
            skLineSegment(sketch, "E1250", {"start": v(-32.3, -112.88) * mm, "end": v(-32.12, -112.7) * mm});
            skArc(sketch, "E1251", {"start": v(-32.3, -112.88) * mm, "mid": v(-32.5, -113.64) * mm, "end": v(-31.94, -114.2) * mm});
            skArc(sketch, "E1252", {"start": v(-31.94, -114.2) * mm, "mid": v(-32.1, -115) * mm, "end": v(-31.94, -115.8) * mm});
            skArc(sketch, "E1253", {"start": v(-31.94, -115.8) * mm, "mid": v(-32.5, -116.36) * mm, "end": v(-32.3, -117.12) * mm});
            skLineSegment(sketch, "E1254", {"start": v(-32.12, -117.3) * mm, "end": v(-32.3, -117.12) * mm});
            skArc(sketch, "E1255", {"start": v(-32.12, -117.3) * mm, "mid": v(-31.36, -117.5) * mm, "end": v(-30.8, -116.94) * mm});
            skArc(sketch, "E1256", {"start": v(-30.8, -116.94) * mm, "mid": v(-30, -117.1) * mm, "end": v(-29.2, -116.94) * mm});
            skArc(sketch, "E1257", {"start": v(-29.2, -116.94) * mm, "mid": v(-28.64, -117.5) * mm, "end": v(-27.88, -117.3) * mm});
            skLineSegment(sketch, "E1258", {"start": v(-27.7, -117.12) * mm, "end": v(-27.88, -117.3) * mm});
            skArc(sketch, "E1259", {"start": v(-27.7, -117.12) * mm, "mid": v(-27.5, -116.36) * mm, "end": v(-28.06, -115.8) * mm});
            skArc(sketch, "E1260", {"start": v(-28.06, -115.8) * mm, "mid": v(-27.9, -115) * mm, "end": v(-28.06, -114.2) * mm});
            skArc(sketch, "E1261", {"start": v(-28.06, -114.2) * mm, "mid": v(-27.5, -113.64) * mm, "end": v(-27.7, -112.88) * mm});
            skLineSegment(sketch, "E1262", {"start": v(-10, -118.65) * mm, "end": v(-12.38, -118.65) * mm});
            skArc(sketch, "E1263", {"start": v(-12.74, -118.8) * mm, "mid": v(-12.58, -118.7) * mm, "end": v(-12.38, -118.65) * mm});
            skLineSegment(sketch, "E1264", {"start": v(-12.74, -118.8) * mm, "end": v(-15.85, -121.9) * mm});
            skArc(sketch, "E1265", {"start": v(-16, -122.27) * mm, "mid": v(-15.96, -122.07) * mm, "end": v(-15.85, -121.9) * mm});
            skLineSegment(sketch, "E1266", {"start": v(-16, -122.27) * mm, "end": v(-16, -123) * mm});
            skArc(sketch, "E1267", {"start": v(-15.49, -123.5) * mm, "mid": v(-15.85, -123.35) * mm, "end": v(-16, -123) * mm});
            skLineSegment(sketch, "E1268", {"start": v(-15.49, -123.5) * mm, "end": v(-13.14, -123.5) * mm});
            skArc(sketch, "E1269", {"start": v(-13.14, -123.5) * mm, "mid": v(-12.78, -123.65) * mm, "end": v(-12.63, -124) * mm});
            skLineSegment(sketch, "E1270", {"start": v(-12.63, -124.5) * mm, "end": v(-12.63, -124) * mm});
            skArc(sketch, "E1271", {"start": v(-12.63, -124.5) * mm, "mid": v(-12.78, -124.85) * mm, "end": v(-13.14, -125) * mm});
            skLineSegment(sketch, "E1272", {"start": v(-26.86, -125) * mm, "end": v(-13.14, -125) * mm});
            skArc(sketch, "E1273", {"start": v(-27.37, -124.5) * mm, "mid": v(-27.22, -124.85) * mm, "end": v(-26.86, -125) * mm});
            skLineSegment(sketch, "E1274", {"start": v(-27.37, -124.5) * mm, "end": v(-27.37, -124) * mm});
            skArc(sketch, "E1275", {"start": v(-26.86, -123.5) * mm, "mid": v(-27.22, -123.65) * mm, "end": v(-27.37, -124) * mm});
            skLineSegment(sketch, "E1276", {"start": v(-24.51, -123.5) * mm, "end": v(-26.86, -123.5) * mm});
            skArc(sketch, "E1277", {"start": v(-24.51, -123.5) * mm, "mid": v(-24.15, -123.35) * mm, "end": v(-24, -123) * mm});
            skLineSegment(sketch, "E1278", {"start": v(-24, -122.27) * mm, "end": v(-24, -123) * mm});
            skArc(sketch, "E1279", {"start": v(-24, -122.27) * mm, "mid": v(-24.04, -122.07) * mm, "end": v(-24.15, -121.9) * mm});
            skLineSegment(sketch, "E1280", {"start": v(-27.26, -118.8) * mm, "end": v(-24.15, -121.9) * mm});
            skArc(sketch, "E1281", {"start": v(-27.26, -118.8) * mm, "mid": v(-27.42, -118.7) * mm, "end": v(-27.62, -118.65) * mm});
            skLineSegment(sketch, "E1282", {"start": v(-32.38, -118.65) * mm, "end": v(-27.62, -118.65) * mm});
            skArc(sketch, "E1283", {"start": v(-32.38, -118.65) * mm, "mid": v(-32.58, -118.7) * mm, "end": v(-32.74, -118.8) * mm});
            skLineSegment(sketch, "E1284", {"start": v(-35.85, -121.9) * mm, "end": v(-32.74, -118.8) * mm});
            skArc(sketch, "E1285", {"start": v(-35.85, -121.9) * mm, "mid": v(-35.96, -122.07) * mm, "end": v(-36, -122.27) * mm});
            skLineSegment(sketch, "E1286", {"start": v(-36, -122.27) * mm, "end": v(-36, -123) * mm});
            skArc(sketch, "E1287", {"start": v(-36, -123) * mm, "mid": v(-35.85, -123.35) * mm, "end": v(-35.49, -123.5) * mm});
            skLineSegment(sketch, "E1288", {"start": v(-33.14, -123.5) * mm, "end": v(-35.49, -123.5) * mm});
            skArc(sketch, "E1289", {"start": v(-32.63, -124) * mm, "mid": v(-32.78, -123.65) * mm, "end": v(-33.14, -123.5) * mm});
            skLineSegment(sketch, "E1290", {"start": v(-32.63, -124) * mm, "end": v(-32.63, -124.5) * mm});
            skArc(sketch, "E1291", {"start": v(-33.14, -125) * mm, "mid": v(-32.78, -124.85) * mm, "end": v(-32.63, -124.5) * mm});
            skLineSegment(sketch, "E1292", {"start": v(-38.5, -125) * mm, "end": v(-33.14, -125) * mm});
            skArc(sketch, "E1293", {"start": v(-40, -123.5) * mm, "mid": v(-39.56, -124.56) * mm, "end": v(-38.5, -125) * mm});
            skLineSegment(sketch, "E1294", {"start": v(-40, -123.5) * mm, "end": v(-40, -118.14) * mm});
            skArc(sketch, "E1295", {"start": v(-39.5, -117.63) * mm, "mid": v(-39.85, -117.78) * mm, "end": v(-40, -118.14) * mm});
            skLineSegment(sketch, "E1296", {"start": v(-39.5, -117.63) * mm, "end": v(-39, -117.63) * mm});
            skArc(sketch, "E1297", {"start": v(-38.5, -118.14) * mm, "mid": v(-38.65, -117.78) * mm, "end": v(-39, -117.63) * mm});
            skLineSegment(sketch, "E1298", {"start": v(-38.5, -120.49) * mm, "end": v(-38.5, -118.14) * mm});
            skArc(sketch, "E1299", {"start": v(-38.5, -120.49) * mm, "mid": v(-38.35, -120.85) * mm, "end": v(-38, -121) * mm});
            skLineSegment(sketch, "E1300", {"start": v(-37.27, -121) * mm, "end": v(-38, -121) * mm});
            skArc(sketch, "E1301", {"start": v(-37.27, -121) * mm, "mid": v(-37.07, -120.96) * mm, "end": v(-36.9, -120.85) * mm});
            skLineSegment(sketch, "E1302", {"start": v(-33.8, -117.74) * mm, "end": v(-36.9, -120.85) * mm});
            skArc(sketch, "E1303", {"start": v(-33.8, -117.74) * mm, "mid": v(-33.7, -117.58) * mm, "end": v(-33.66, -117.38) * mm});
            skLineSegment(sketch, "E1304", {"start": v(-33.66, -112.62) * mm, "end": v(-33.66, -117.38) * mm});
            skArc(sketch, "E1305", {"start": v(-33.66, -112.62) * mm, "mid": v(-33.7, -112.42) * mm, "end": v(-33.8, -112.26) * mm});
            skLineSegment(sketch, "E1306", {"start": v(-33.8, -112.26) * mm, "end": v(-36.9, -109.15) * mm});
            skArc(sketch, "E1307", {"start": v(-36.9, -109.15) * mm, "mid": v(-37.07, -109.04) * mm, "end": v(-37.27, -109) * mm});
            skLineSegment(sketch, "E1308", {"start": v(-37.27, -109) * mm, "end": v(-38, -109) * mm});
            skArc(sketch, "E1309", {"start": v(-38, -109) * mm, "mid": v(-38.35, -109.15) * mm, "end": v(-38.5, -109.51) * mm});
            skLineSegment(sketch, "E1310", {"start": v(-38.5, -109.51) * mm, "end": v(-38.5, -111.86) * mm});
            skArc(sketch, "E1311", {"start": v(-39, -112.37) * mm, "mid": v(-38.65, -112.22) * mm, "end": v(-38.5, -111.86) * mm});
            skLineSegment(sketch, "E1312", {"start": v(-39, -112.37) * mm, "end": v(-39.5, -112.37) * mm});
            skArc(sketch, "E1313", {"start": v(-40, -111.86) * mm, "mid": v(-39.85, -112.22) * mm, "end": v(-39.5, -112.37) * mm});
            skLineSegment(sketch, "E1314", {"start": v(-40, -111.86) * mm, "end": v(-40, -106.5) * mm});
            skArc(sketch, "E1315", {"start": v(-38.5, -105) * mm, "mid": v(-39.56, -105.44) * mm, "end": v(-40, -106.5) * mm});
            skLineSegment(sketch, "E1316", {"start": v(-38.5, -105) * mm, "end": v(-33.14, -105) * mm});
            skArc(sketch, "E1317", {"start": v(-32.63, -105.5) * mm, "mid": v(-32.78, -105.15) * mm, "end": v(-33.14, -105) * mm});
            skLineSegment(sketch, "E1318", {"start": v(-32.63, -105.5) * mm, "end": v(-32.63, -106) * mm});
            skArc(sketch, "E1319", {"start": v(-33.14, -106.5) * mm, "mid": v(-32.78, -106.35) * mm, "end": v(-32.63, -106) * mm});
            skLineSegment(sketch, "E1320", {"start": v(-33.14, -106.5) * mm, "end": v(-35.49, -106.5) * mm});
            skArc(sketch, "E1321", {"start": v(-35.49, -106.5) * mm, "mid": v(-35.85, -106.65) * mm, "end": v(-36, -107) * mm});
            skLineSegment(sketch, "E1322", {"start": v(-36, -107) * mm, "end": v(-36, -107.73) * mm});
            skArc(sketch, "E1323", {"start": v(-36, -107.73) * mm, "mid": v(-35.96, -107.93) * mm, "end": v(-35.85, -108.1) * mm});
            skLineSegment(sketch, "E1324", {"start": v(-35.85, -108.1) * mm, "end": v(-32.74, -111.2) * mm});
            skArc(sketch, "E1325", {"start": v(-32.74, -111.2) * mm, "mid": v(-32.58, -111.3) * mm, "end": v(-32.38, -111.35) * mm});
            skLineSegment(sketch, "E1326", {"start": v(-32.38, -111.35) * mm, "end": v(-27.62, -111.35) * mm});
            skArc(sketch, "E1327", {"start": v(-27.62, -111.35) * mm, "mid": v(-27.42, -111.3) * mm, "end": v(-27.26, -111.2) * mm});
            skLineSegment(sketch, "E1328", {"start": v(-27.26, -111.2) * mm, "end": v(-24.15, -108.1) * mm});
            skArc(sketch, "E1329", {"start": v(-24.15, -108.1) * mm, "mid": v(-24.04, -107.93) * mm, "end": v(-24, -107.73) * mm});
            skLineSegment(sketch, "E1330", {"start": v(-24, -107) * mm, "end": v(-24, -107.73) * mm});
            skArc(sketch, "E1331", {"start": v(-24, -107) * mm, "mid": v(-24.15, -106.65) * mm, "end": v(-24.51, -106.5) * mm});
            skLineSegment(sketch, "E1332", {"start": v(-24.51, -106.5) * mm, "end": v(-26.86, -106.5) * mm});
            skArc(sketch, "E1333", {"start": v(-27.37, -106) * mm, "mid": v(-27.22, -106.35) * mm, "end": v(-26.86, -106.5) * mm});
            skLineSegment(sketch, "E1334", {"start": v(-27.37, -106) * mm, "end": v(-27.37, -105.5) * mm});
            skArc(sketch, "E1335", {"start": v(-26.86, -105) * mm, "mid": v(-27.22, -105.15) * mm, "end": v(-27.37, -105.5) * mm});
            skLineSegment(sketch, "E1336", {"start": v(-13.14, -105) * mm, "end": v(-26.86, -105) * mm});
            skArc(sketch, "E1337", {"start": v(-13.14, -105) * mm, "mid": v(-12.78, -105.15) * mm, "end": v(-12.63, -105.5) * mm});
            skLineSegment(sketch, "E1338", {"start": v(-12.63, -106) * mm, "end": v(-12.63, -105.5) * mm});
            skArc(sketch, "E1339", {"start": v(-12.63, -106) * mm, "mid": v(-12.78, -106.35) * mm, "end": v(-13.14, -106.5) * mm});
            skLineSegment(sketch, "E1340", {"start": v(-15.49, -106.5) * mm, "end": v(-13.14, -106.5) * mm});
            skArc(sketch, "E1341", {"start": v(-16, -107) * mm, "mid": v(-15.85, -106.65) * mm, "end": v(-15.49, -106.5) * mm});
            skLineSegment(sketch, "E1342", {"start": v(-16, -107) * mm, "end": v(-16, -107.73) * mm});
            skArc(sketch, "E1343", {"start": v(-15.85, -108.1) * mm, "mid": v(-15.96, -107.93) * mm, "end": v(-16, -107.73) * mm});
            skLineSegment(sketch, "E1344", {"start": v(-12.74, -111.2) * mm, "end": v(-15.85, -108.1) * mm});
            skArc(sketch, "E1345", {"start": v(-12.38, -111.35) * mm, "mid": v(-12.58, -111.3) * mm, "end": v(-12.74, -111.2) * mm});
            skLineSegment(sketch, "E1346", {"start": v(-10, -111.35) * mm, "end": v(-12.38, -111.35) * mm});
            skArc(sketch, "E1347", {"start": v(-13.65, -112.62) * mm, "mid": v(-13.7, -112.42) * mm, "end": v(-13.8, -112.26) * mm});
            skLineSegment(sketch, "E1348", {"start": v(-13.8, -112.26) * mm, "end": v(-17.35, -108.71) * mm});
            skArc(sketch, "E1349", {"start": v(-17.35, -108.71) * mm, "mid": v(-17.46, -108.55) * mm, "end": v(-17.5, -108.36) * mm});
            skLineSegment(sketch, "E1350", {"start": v(-17.5, -107) * mm, "end": v(-17.5, -108.36) * mm});
            skArc(sketch, "E1351", {"start": v(-18, -106.5) * mm, "mid": v(-17.64, -106.65) * mm, "end": v(-17.5, -107) * mm});
            skLineSegment(sketch, "E1352", {"start": v(-22, -106.5) * mm, "end": v(-18, -106.5) * mm});
            skArc(sketch, "E1353", {"start": v(-22, -106.5) * mm, "mid": v(-22.36, -106.65) * mm, "end": v(-22.5, -107) * mm});
            skLineSegment(sketch, "E1354", {"start": v(-22.5, -107) * mm, "end": v(-22.5, -108.36) * mm});
            skArc(sketch, "E1355", {"start": v(-22.65, -108.71) * mm, "mid": v(-22.54, -108.55) * mm, "end": v(-22.5, -108.36) * mm});
            skLineSegment(sketch, "E1356", {"start": v(-26.2, -112.26) * mm, "end": v(-22.65, -108.71) * mm});
            skArc(sketch, "E1357", {"start": v(-26.2, -112.26) * mm, "mid": v(-26.3, -112.42) * mm, "end": v(-26.35, -112.62) * mm});
            skLineSegment(sketch, "E1358", {"start": v(-26.35, -112.62) * mm, "end": v(-26.35, -117.38) * mm});
            skArc(sketch, "E1359", {"start": v(-26.35, -117.38) * mm, "mid": v(-26.3, -117.58) * mm, "end": v(-26.2, -117.74) * mm});
            skLineSegment(sketch, "E1360", {"start": v(-26.2, -117.74) * mm, "end": v(-22.65, -121.29) * mm});
            skArc(sketch, "E1361", {"start": v(-22.5, -121.64) * mm, "mid": v(-22.54, -121.45) * mm, "end": v(-22.65, -121.29) * mm});
            skLineSegment(sketch, "E1362", {"start": v(-22.5, -121.64) * mm, "end": v(-22.5, -123) * mm});
            skArc(sketch, "E1363", {"start": v(-22.5, -123) * mm, "mid": v(-22.36, -123.35) * mm, "end": v(-22, -123.5) * mm});
            skLineSegment(sketch, "E1364", {"start": v(-22, -123.5) * mm, "end": v(-18, -123.5) * mm});
            skArc(sketch, "E1365", {"start": v(-17.5, -123) * mm, "mid": v(-17.64, -123.35) * mm, "end": v(-18, -123.5) * mm});
            skLineSegment(sketch, "E1366", {"start": v(-17.5, -121.64) * mm, "end": v(-17.5, -123) * mm});
            skArc(sketch, "E1367", {"start": v(-17.5, -121.64) * mm, "mid": v(-17.46, -121.45) * mm, "end": v(-17.35, -121.29) * mm});
            skLineSegment(sketch, "E1368", {"start": v(-13.8, -117.74) * mm, "end": v(-17.35, -121.29) * mm});
            skArc(sketch, "E1369", {"start": v(-13.65, -117.38) * mm, "mid": v(-13.7, -117.58) * mm, "end": v(-13.8, -117.74) * mm});
            skLineSegment(sketch, "E1370", {"start": v(-6.35, -112.62) * mm, "end": v(-6.35, -117.38) * mm});
            skArc(sketch, "E1371", {"start": v(-9.2, -113.06) * mm, "mid": v(-8.64, -112.5) * mm, "end": v(-7.88, -112.7) * mm});
            skLineSegment(sketch, "E1372", {"start": v(-7.88, -112.7) * mm, "end": v(-7.7, -112.88) * mm});
            skArc(sketch, "E1373", {"start": v(-7.7, -112.88) * mm, "mid": v(-7.5, -113.64) * mm, "end": v(-8.06, -114.2) * mm});
            skArc(sketch, "E1374", {"start": v(-8.06, -114.2) * mm, "mid": v(-7.9, -115) * mm, "end": v(-8.06, -115.8) * mm});
            skArc(sketch, "E1375", {"start": v(-8.06, -115.8) * mm, "mid": v(-7.5, -116.36) * mm, "end": v(-7.7, -117.12) * mm});
            skLineSegment(sketch, "E1376", {"start": v(-7.7, -117.12) * mm, "end": v(-7.88, -117.3) * mm});
            skArc(sketch, "E1377", {"start": v(-7.88, -117.3) * mm, "mid": v(-8.64, -117.5) * mm, "end": v(-9.2, -116.94) * mm});
            skLineSegment(sketch, "E1378", {"start": v(-10, -118.65) * mm, "end": v(-7.62, -118.65) * mm});
            skArc(sketch, "E1379", {"start": v(-7.62, -118.65) * mm, "mid": v(-7.42, -118.7) * mm, "end": v(-7.26, -118.8) * mm});
            skLineSegment(sketch, "E1380", {"start": v(-7.26, -118.8) * mm, "end": v(-4.15, -121.9) * mm});
            skArc(sketch, "E1381", {"start": v(-4.15, -121.9) * mm, "mid": v(-4.04, -122.07) * mm, "end": v(-4, -122.27) * mm});
            skLineSegment(sketch, "E1382", {"start": v(-4, -122.27) * mm, "end": v(-4, -123) * mm});
            skArc(sketch, "E1383", {"start": v(-4, -123) * mm, "mid": v(-4.15, -123.35) * mm, "end": v(-4.51, -123.5) * mm});
            skLineSegment(sketch, "E1384", {"start": v(-4.51, -123.5) * mm, "end": v(-6.86, -123.5) * mm});
            skArc(sketch, "E1385", {"start": v(-7.37, -124) * mm, "mid": v(-7.22, -123.65) * mm, "end": v(-6.86, -123.5) * mm});
            skLineSegment(sketch, "E1386", {"start": v(-7.37, -124.5) * mm, "end": v(-7.37, -124) * mm});
            skArc(sketch, "E1387", {"start": v(-6.86, -125) * mm, "mid": v(-7.22, -124.85) * mm, "end": v(-7.37, -124.5) * mm});
            skLineSegment(sketch, "E1388", {"start": v(6.86, -125) * mm, "end": v(-6.86, -125) * mm});
            skLineSegment(sketch, "E1389", {"start": v(-6.86, -105) * mm, "end": v(6.86, -105) * mm});
            skArc(sketch, "E1390", {"start": v(-7.37, -105.5) * mm, "mid": v(-7.22, -105.15) * mm, "end": v(-6.86, -105) * mm});
            skLineSegment(sketch, "E1391", {"start": v(-7.37, -106) * mm, "end": v(-7.37, -105.5) * mm});
            skArc(sketch, "E1392", {"start": v(-6.86, -106.5) * mm, "mid": v(-7.22, -106.35) * mm, "end": v(-7.37, -106) * mm});
            skLineSegment(sketch, "E1393", {"start": v(-4.51, -106.5) * mm, "end": v(-6.86, -106.5) * mm});
            skArc(sketch, "E1394", {"start": v(-4.51, -106.5) * mm, "mid": v(-4.15, -106.65) * mm, "end": v(-4, -107) * mm});
            skLineSegment(sketch, "E1395", {"start": v(-4, -107) * mm, "end": v(-4, -107.73) * mm});
            skArc(sketch, "E1396", {"start": v(-4, -107.73) * mm, "mid": v(-4.04, -107.93) * mm, "end": v(-4.15, -108.1) * mm});
            skLineSegment(sketch, "E1397", {"start": v(-7.26, -111.2) * mm, "end": v(-4.15, -108.1) * mm});
            skArc(sketch, "E1398", {"start": v(-7.26, -111.2) * mm, "mid": v(-7.42, -111.3) * mm, "end": v(-7.62, -111.35) * mm});
            skLineSegment(sketch, "E1399", {"start": v(-10, -111.35) * mm, "end": v(-7.62, -111.35) * mm});
            skArc(sketch, "E1400", {"start": v(-6.2, -112.26) * mm, "mid": v(-6.3, -112.42) * mm, "end": v(-6.35, -112.62) * mm});
            skLineSegment(sketch, "E1401", {"start": v(-6.2, -112.26) * mm, "end": v(-2.65, -108.71) * mm});
            skArc(sketch, "E1402", {"start": v(-2.5, -108.36) * mm, "mid": v(-2.54, -108.55) * mm, "end": v(-2.65, -108.71) * mm});
            skLineSegment(sketch, "E1403", {"start": v(-2.5, -107) * mm, "end": v(-2.5, -108.36) * mm});
            skArc(sketch, "E1404", {"start": v(-2.5, -107) * mm, "mid": v(-2.36, -106.65) * mm, "end": v(-2, -106.5) * mm});
            skLineSegment(sketch, "E1405", {"start": v(2, -106.5) * mm, "end": v(-2, -106.5) * mm});
            skLineSegment(sketch, "E1406", {"start": v(2, -123.5) * mm, "end": v(-2, -123.5) * mm});
            skArc(sketch, "E1407", {"start": v(-2, -123.5) * mm, "mid": v(-2.36, -123.35) * mm, "end": v(-2.5, -123) * mm});
            skLineSegment(sketch, "E1408", {"start": v(-2.5, -121.64) * mm, "end": v(-2.5, -123) * mm});
            skArc(sketch, "E1409", {"start": v(-2.65, -121.29) * mm, "mid": v(-2.54, -121.45) * mm, "end": v(-2.5, -121.64) * mm});
            skLineSegment(sketch, "E1410", {"start": v(-6.2, -117.74) * mm, "end": v(-2.65, -121.29) * mm});
            skArc(sketch, "E1411", {"start": v(-6.2, -117.74) * mm, "mid": v(-6.3, -117.58) * mm, "end": v(-6.35, -117.38) * mm});
            skArc(sketch, "E1412", {"start": v(-10, -112.9) * mm, "mid": v(-9.6, -112.94) * mm, "end": v(-9.2, -113.06) * mm});
            skArc(sketch, "E1413", {"start": v(-9.2, -116.94) * mm, "mid": v(-9.6, -117.06) * mm, "end": v(-10, -117.1) * mm});
            skCircle(sketch, "E1414", {"center": v(-42.45, -115) * mm, "radius": 4 * mm});
            skLineSegment(sketch, "E1415", {"start": v(13.66, -112.62) * mm, "end": v(13.66, -117.38) * mm});
            skLineSegment(sketch, "E1416", {"start": v(27.88, -112.7) * mm, "end": v(27.7, -112.88) * mm});
            skArc(sketch, "E1417", {"start": v(10, -112.9) * mm, "mid": v(10.4, -112.94) * mm, "end": v(10.8, -113.06) * mm});
            skArc(sketch, "E1418", {"start": v(10.8, -113.06) * mm, "mid": v(11.36, -112.5) * mm, "end": v(12.12, -112.7) * mm});
            skLineSegment(sketch, "E1419", {"start": v(12.12, -112.7) * mm, "end": v(12.3, -112.88) * mm});
            skArc(sketch, "E1420", {"start": v(12.3, -112.88) * mm, "mid": v(12.5, -113.64) * mm, "end": v(11.94, -114.2) * mm});
            skArc(sketch, "E1421", {"start": v(11.94, -114.2) * mm, "mid": v(12.1, -115) * mm, "end": v(11.94, -115.8) * mm});
            skArc(sketch, "E1422", {"start": v(11.94, -115.8) * mm, "mid": v(12.5, -116.36) * mm, "end": v(12.3, -117.12) * mm});
            skLineSegment(sketch, "E1423", {"start": v(12.3, -117.12) * mm, "end": v(12.12, -117.3) * mm});
            skArc(sketch, "E1424", {"start": v(12.12, -117.3) * mm, "mid": v(11.36, -117.5) * mm, "end": v(10.8, -116.94) * mm});
            skArc(sketch, "E1425", {"start": v(10.8, -116.94) * mm, "mid": v(10.4, -117.06) * mm, "end": v(10, -117.1) * mm});
            skArc(sketch, "E1426", {"start": v(29.2, -113.06) * mm, "mid": v(28.64, -112.5) * mm, "end": v(27.88, -112.7) * mm});
            skArc(sketch, "E1427", {"start": v(30.8, -113.06) * mm, "mid": v(30, -112.9) * mm, "end": v(29.2, -113.06) * mm});
            skArc(sketch, "E1428", {"start": v(32.12, -112.7) * mm, "mid": v(31.36, -112.5) * mm, "end": v(30.8, -113.06) * mm});
            skLineSegment(sketch, "E1429", {"start": v(32.3, -112.88) * mm, "end": v(32.12, -112.7) * mm});
            skArc(sketch, "E1430", {"start": v(31.94, -114.2) * mm, "mid": v(32.5, -113.64) * mm, "end": v(32.3, -112.88) * mm});
            skArc(sketch, "E1431", {"start": v(31.94, -115.8) * mm, "mid": v(32.1, -115) * mm, "end": v(31.94, -114.2) * mm});
            skArc(sketch, "E1432", {"start": v(32.3, -117.12) * mm, "mid": v(32.5, -116.36) * mm, "end": v(31.94, -115.8) * mm});
            skLineSegment(sketch, "E1433", {"start": v(32.12, -117.3) * mm, "end": v(32.3, -117.12) * mm});
            skArc(sketch, "E1434", {"start": v(30.8, -116.94) * mm, "mid": v(31.36, -117.5) * mm, "end": v(32.12, -117.3) * mm});
            skArc(sketch, "E1435", {"start": v(29.2, -116.94) * mm, "mid": v(30, -117.1) * mm, "end": v(30.8, -116.94) * mm});
            skArc(sketch, "E1436", {"start": v(27.88, -117.3) * mm, "mid": v(28.64, -117.5) * mm, "end": v(29.2, -116.94) * mm});
            skLineSegment(sketch, "E1437", {"start": v(27.7, -117.12) * mm, "end": v(27.88, -117.3) * mm});
            skArc(sketch, "E1438", {"start": v(28.06, -115.8) * mm, "mid": v(27.5, -116.36) * mm, "end": v(27.7, -117.12) * mm});
            skArc(sketch, "E1439", {"start": v(28.06, -114.2) * mm, "mid": v(27.9, -115) * mm, "end": v(28.06, -115.8) * mm});
            skArc(sketch, "E1440", {"start": v(27.7, -112.88) * mm, "mid": v(27.5, -113.64) * mm, "end": v(28.06, -114.2) * mm});
            skLineSegment(sketch, "E1441", {"start": v(10, -118.65) * mm, "end": v(12.38, -118.65) * mm});
            skArc(sketch, "E1442", {"start": v(12.38, -118.65) * mm, "mid": v(12.58, -118.7) * mm, "end": v(12.74, -118.8) * mm});
            skLineSegment(sketch, "E1443", {"start": v(12.74, -118.8) * mm, "end": v(15.85, -121.9) * mm});
            skArc(sketch, "E1444", {"start": v(15.85, -121.9) * mm, "mid": v(15.96, -122.07) * mm, "end": v(16, -122.27) * mm});
            skLineSegment(sketch, "E1445", {"start": v(16, -122.27) * mm, "end": v(16, -123) * mm});
            skArc(sketch, "E1446", {"start": v(16, -123) * mm, "mid": v(15.85, -123.35) * mm, "end": v(15.49, -123.5) * mm});
            skLineSegment(sketch, "E1447", {"start": v(15.49, -123.5) * mm, "end": v(13.14, -123.5) * mm});
            skArc(sketch, "E1448", {"start": v(12.63, -124) * mm, "mid": v(12.78, -123.65) * mm, "end": v(13.14, -123.5) * mm});
            skLineSegment(sketch, "E1449", {"start": v(12.63, -124.5) * mm, "end": v(12.63, -124) * mm});
            skArc(sketch, "E1450", {"start": v(13.14, -125) * mm, "mid": v(12.78, -124.85) * mm, "end": v(12.63, -124.5) * mm});
            skLineSegment(sketch, "E1451", {"start": v(26.86, -125) * mm, "end": v(13.14, -125) * mm});
            skArc(sketch, "E1452", {"start": v(26.86, -125) * mm, "mid": v(27.22, -124.85) * mm, "end": v(27.37, -124.5) * mm});
            skLineSegment(sketch, "E1453", {"start": v(27.37, -124.5) * mm, "end": v(27.37, -124) * mm});
            skArc(sketch, "E1454", {"start": v(27.37, -124) * mm, "mid": v(27.22, -123.65) * mm, "end": v(26.86, -123.5) * mm});
            skLineSegment(sketch, "E1455", {"start": v(24.51, -123.5) * mm, "end": v(26.86, -123.5) * mm});
            skArc(sketch, "E1456", {"start": v(24, -123) * mm, "mid": v(24.15, -123.35) * mm, "end": v(24.51, -123.5) * mm});
            skLineSegment(sketch, "E1457", {"start": v(24, -122.27) * mm, "end": v(24, -123) * mm});
            skArc(sketch, "E1458", {"start": v(24.15, -121.9) * mm, "mid": v(24.04, -122.07) * mm, "end": v(24, -122.27) * mm});
            skLineSegment(sketch, "E1459", {"start": v(27.26, -118.8) * mm, "end": v(24.15, -121.9) * mm});
            skArc(sketch, "E1460", {"start": v(27.62, -118.65) * mm, "mid": v(27.42, -118.7) * mm, "end": v(27.26, -118.8) * mm});
            skLineSegment(sketch, "E1461", {"start": v(32.38, -118.65) * mm, "end": v(27.62, -118.65) * mm});
            skArc(sketch, "E1462", {"start": v(32.74, -118.8) * mm, "mid": v(32.58, -118.7) * mm, "end": v(32.38, -118.65) * mm});
            skLineSegment(sketch, "E1463", {"start": v(35.85, -121.9) * mm, "end": v(32.74, -118.8) * mm});
            skArc(sketch, "E1464", {"start": v(36, -122.27) * mm, "mid": v(35.96, -122.07) * mm, "end": v(35.85, -121.9) * mm});
            skLineSegment(sketch, "E1465", {"start": v(36, -122.27) * mm, "end": v(36, -123) * mm});
            skArc(sketch, "E1466", {"start": v(35.49, -123.5) * mm, "mid": v(35.85, -123.35) * mm, "end": v(36, -123) * mm});
            skLineSegment(sketch, "E1467", {"start": v(33.14, -123.5) * mm, "end": v(35.49, -123.5) * mm});
            skArc(sketch, "E1468", {"start": v(33.14, -123.5) * mm, "mid": v(32.78, -123.65) * mm, "end": v(32.63, -124) * mm});
            skLineSegment(sketch, "E1469", {"start": v(32.63, -124) * mm, "end": v(32.63, -124.5) * mm});
            skArc(sketch, "E1470", {"start": v(32.63, -124.5) * mm, "mid": v(32.78, -124.85) * mm, "end": v(33.14, -125) * mm});
            skLineSegment(sketch, "E1471", {"start": v(38.5, -125) * mm, "end": v(33.14, -125) * mm});
            skArc(sketch, "E1472", {"start": v(38.5, -125) * mm, "mid": v(39.56, -124.56) * mm, "end": v(40, -123.5) * mm});
            skLineSegment(sketch, "E1473", {"start": v(40, -123.5) * mm, "end": v(40, -118.14) * mm});
            skArc(sketch, "E1474", {"start": v(40, -118.14) * mm, "mid": v(39.85, -117.78) * mm, "end": v(39.5, -117.63) * mm});
            skLineSegment(sketch, "E1475", {"start": v(39.5, -117.63) * mm, "end": v(39, -117.63) * mm});
            skArc(sketch, "E1476", {"start": v(39, -117.63) * mm, "mid": v(38.65, -117.78) * mm, "end": v(38.5, -118.14) * mm});
            skLineSegment(sketch, "E1477", {"start": v(38.5, -120.49) * mm, "end": v(38.5, -118.14) * mm});
            skArc(sketch, "E1478", {"start": v(38, -121) * mm, "mid": v(38.35, -120.85) * mm, "end": v(38.5, -120.49) * mm});
            skLineSegment(sketch, "E1479", {"start": v(37.27, -121) * mm, "end": v(38, -121) * mm});
            skArc(sketch, "E1480", {"start": v(36.9, -120.85) * mm, "mid": v(37.07, -120.96) * mm, "end": v(37.27, -121) * mm});
            skLineSegment(sketch, "E1481", {"start": v(33.8, -117.74) * mm, "end": v(36.9, -120.85) * mm});
            skArc(sketch, "E1482", {"start": v(33.66, -117.38) * mm, "mid": v(33.7, -117.58) * mm, "end": v(33.8, -117.74) * mm});
            skLineSegment(sketch, "E1483", {"start": v(33.66, -112.62) * mm, "end": v(33.66, -117.38) * mm});
            skArc(sketch, "E1484", {"start": v(33.8, -112.26) * mm, "mid": v(33.7, -112.42) * mm, "end": v(33.66, -112.62) * mm});
            skLineSegment(sketch, "E1485", {"start": v(33.8, -112.26) * mm, "end": v(36.9, -109.15) * mm});
            skArc(sketch, "E1486", {"start": v(37.27, -109) * mm, "mid": v(37.07, -109.04) * mm, "end": v(36.9, -109.15) * mm});
            skLineSegment(sketch, "E1487", {"start": v(37.27, -109) * mm, "end": v(38, -109) * mm});
            skArc(sketch, "E1488", {"start": v(38.5, -109.51) * mm, "mid": v(38.35, -109.15) * mm, "end": v(38, -109) * mm});
            skLineSegment(sketch, "E1489", {"start": v(38.5, -109.51) * mm, "end": v(38.5, -111.86) * mm});
            skArc(sketch, "E1490", {"start": v(38.5, -111.86) * mm, "mid": v(38.65, -112.22) * mm, "end": v(39, -112.37) * mm});
            skLineSegment(sketch, "E1491", {"start": v(39, -112.37) * mm, "end": v(39.5, -112.37) * mm});
            skArc(sketch, "E1492", {"start": v(39.5, -112.37) * mm, "mid": v(39.85, -112.22) * mm, "end": v(40, -111.86) * mm});
            skLineSegment(sketch, "E1493", {"start": v(40, -111.86) * mm, "end": v(40, -106.5) * mm});
            skArc(sketch, "E1494", {"start": v(40, -106.5) * mm, "mid": v(39.56, -105.44) * mm, "end": v(38.5, -105) * mm});
            skLineSegment(sketch, "E1495", {"start": v(38.5, -105) * mm, "end": v(33.14, -105) * mm});
            skArc(sketch, "E1496", {"start": v(33.14, -105) * mm, "mid": v(32.78, -105.15) * mm, "end": v(32.63, -105.5) * mm});
            skLineSegment(sketch, "E1497", {"start": v(32.63, -105.5) * mm, "end": v(32.63, -106) * mm});
            skArc(sketch, "E1498", {"start": v(32.63, -106) * mm, "mid": v(32.78, -106.35) * mm, "end": v(33.14, -106.5) * mm});
            skLineSegment(sketch, "E1499", {"start": v(33.14, -106.5) * mm, "end": v(35.49, -106.5) * mm});
            skArc(sketch, "E1500", {"start": v(36, -107) * mm, "mid": v(35.85, -106.65) * mm, "end": v(35.49, -106.5) * mm});
            skLineSegment(sketch, "E1501", {"start": v(36, -107) * mm, "end": v(36, -107.73) * mm});
            skArc(sketch, "E1502", {"start": v(35.85, -108.1) * mm, "mid": v(35.96, -107.93) * mm, "end": v(36, -107.73) * mm});
            skLineSegment(sketch, "E1503", {"start": v(35.85, -108.1) * mm, "end": v(32.74, -111.2) * mm});
            skArc(sketch, "E1504", {"start": v(32.38, -111.35) * mm, "mid": v(32.58, -111.3) * mm, "end": v(32.74, -111.2) * mm});
            skLineSegment(sketch, "E1505", {"start": v(32.38, -111.35) * mm, "end": v(27.62, -111.35) * mm});
            skArc(sketch, "E1506", {"start": v(27.26, -111.2) * mm, "mid": v(27.42, -111.3) * mm, "end": v(27.62, -111.35) * mm});
            skLineSegment(sketch, "E1507", {"start": v(27.26, -111.2) * mm, "end": v(24.15, -108.1) * mm});
            skArc(sketch, "E1508", {"start": v(24, -107.73) * mm, "mid": v(24.04, -107.93) * mm, "end": v(24.15, -108.1) * mm});
            skLineSegment(sketch, "E1509", {"start": v(24, -107) * mm, "end": v(24, -107.73) * mm});
            skArc(sketch, "E1510", {"start": v(24.51, -106.5) * mm, "mid": v(24.15, -106.65) * mm, "end": v(24, -107) * mm});
            skLineSegment(sketch, "E1511", {"start": v(24.51, -106.5) * mm, "end": v(26.86, -106.5) * mm});
            skArc(sketch, "E1512", {"start": v(26.86, -106.5) * mm, "mid": v(27.22, -106.35) * mm, "end": v(27.37, -106) * mm});
            skLineSegment(sketch, "E1513", {"start": v(27.37, -106) * mm, "end": v(27.37, -105.5) * mm});
            skArc(sketch, "E1514", {"start": v(27.37, -105.5) * mm, "mid": v(27.22, -105.15) * mm, "end": v(26.86, -105) * mm});
            skLineSegment(sketch, "E1515", {"start": v(13.14, -105) * mm, "end": v(26.86, -105) * mm});
            skArc(sketch, "E1516", {"start": v(12.63, -105.5) * mm, "mid": v(12.78, -105.15) * mm, "end": v(13.14, -105) * mm});
            skLineSegment(sketch, "E1517", {"start": v(12.63, -106) * mm, "end": v(12.63, -105.5) * mm});
            skArc(sketch, "E1518", {"start": v(13.14, -106.5) * mm, "mid": v(12.78, -106.35) * mm, "end": v(12.63, -106) * mm});
            skLineSegment(sketch, "E1519", {"start": v(15.49, -106.5) * mm, "end": v(13.14, -106.5) * mm});
            skArc(sketch, "E1520", {"start": v(15.49, -106.5) * mm, "mid": v(15.85, -106.65) * mm, "end": v(16, -107) * mm});
            skLineSegment(sketch, "E1521", {"start": v(16, -107) * mm, "end": v(16, -107.73) * mm});
            skArc(sketch, "E1522", {"start": v(16, -107.73) * mm, "mid": v(15.96, -107.93) * mm, "end": v(15.85, -108.1) * mm});
            skLineSegment(sketch, "E1523", {"start": v(12.74, -111.2) * mm, "end": v(15.85, -108.1) * mm});
            skArc(sketch, "E1524", {"start": v(12.74, -111.2) * mm, "mid": v(12.58, -111.3) * mm, "end": v(12.38, -111.35) * mm});
            skLineSegment(sketch, "E1525", {"start": v(10, -111.35) * mm, "end": v(12.38, -111.35) * mm});
            skArc(sketch, "E1526", {"start": v(13.8, -112.26) * mm, "mid": v(13.7, -112.42) * mm, "end": v(13.66, -112.62) * mm});
            skLineSegment(sketch, "E1527", {"start": v(13.8, -112.26) * mm, "end": v(17.35, -108.71) * mm});
            skArc(sketch, "E1528", {"start": v(17.5, -108.36) * mm, "mid": v(17.46, -108.55) * mm, "end": v(17.35, -108.71) * mm});
            skLineSegment(sketch, "E1529", {"start": v(17.5, -107) * mm, "end": v(17.5, -108.36) * mm});
            skArc(sketch, "E1530", {"start": v(17.5, -107) * mm, "mid": v(17.64, -106.65) * mm, "end": v(18, -106.5) * mm});
            skLineSegment(sketch, "E1531", {"start": v(22, -106.5) * mm, "end": v(18, -106.5) * mm});
            skArc(sketch, "E1532", {"start": v(22.5, -107) * mm, "mid": v(22.36, -106.65) * mm, "end": v(22, -106.5) * mm});
            skLineSegment(sketch, "E1533", {"start": v(22.5, -107) * mm, "end": v(22.5, -108.36) * mm});
            skArc(sketch, "E1534", {"start": v(22.5, -108.36) * mm, "mid": v(22.54, -108.55) * mm, "end": v(22.65, -108.71) * mm});
            skLineSegment(sketch, "E1535", {"start": v(26.2, -112.26) * mm, "end": v(22.65, -108.71) * mm});
            skArc(sketch, "E1536", {"start": v(26.35, -112.62) * mm, "mid": v(26.3, -112.42) * mm, "end": v(26.2, -112.26) * mm});
            skLineSegment(sketch, "E1537", {"start": v(26.35, -112.62) * mm, "end": v(26.35, -117.38) * mm});
            skArc(sketch, "E1538", {"start": v(26.2, -117.74) * mm, "mid": v(26.3, -117.58) * mm, "end": v(26.35, -117.38) * mm});
            skLineSegment(sketch, "E1539", {"start": v(26.2, -117.74) * mm, "end": v(22.65, -121.29) * mm});
            skArc(sketch, "E1540", {"start": v(22.65, -121.29) * mm, "mid": v(22.54, -121.45) * mm, "end": v(22.5, -121.64) * mm});
            skLineSegment(sketch, "E1541", {"start": v(22.5, -121.64) * mm, "end": v(22.5, -123) * mm});
            skArc(sketch, "E1542", {"start": v(22, -123.5) * mm, "mid": v(22.36, -123.35) * mm, "end": v(22.5, -123) * mm});
            skLineSegment(sketch, "E1543", {"start": v(22, -123.5) * mm, "end": v(18, -123.5) * mm});
            skArc(sketch, "E1544", {"start": v(18, -123.5) * mm, "mid": v(17.64, -123.35) * mm, "end": v(17.5, -123) * mm});
            skLineSegment(sketch, "E1545", {"start": v(17.5, -121.64) * mm, "end": v(17.5, -123) * mm});
            skArc(sketch, "E1546", {"start": v(17.35, -121.29) * mm, "mid": v(17.46, -121.45) * mm, "end": v(17.5, -121.64) * mm});
            skLineSegment(sketch, "E1547", {"start": v(13.8, -117.74) * mm, "end": v(17.35, -121.29) * mm});
            skArc(sketch, "E1548", {"start": v(13.8, -117.74) * mm, "mid": v(13.7, -117.58) * mm, "end": v(13.66, -117.38) * mm});
            skLineSegment(sketch, "E1549", {"start": v(6.35, -112.62) * mm, "end": v(6.35, -117.38) * mm});
            skArc(sketch, "E1550", {"start": v(7.88, -112.7) * mm, "mid": v(8.64, -112.5) * mm, "end": v(9.2, -113.06) * mm});
            skLineSegment(sketch, "E1551", {"start": v(7.88, -112.7) * mm, "end": v(7.7, -112.88) * mm});
            skArc(sketch, "E1552", {"start": v(8.06, -114.2) * mm, "mid": v(7.5, -113.64) * mm, "end": v(7.7, -112.88) * mm});
            skArc(sketch, "E1553", {"start": v(8.06, -115.8) * mm, "mid": v(7.9, -115) * mm, "end": v(8.06, -114.2) * mm});
            skArc(sketch, "E1554", {"start": v(7.7, -117.12) * mm, "mid": v(7.5, -116.36) * mm, "end": v(8.06, -115.8) * mm});
            skLineSegment(sketch, "E1555", {"start": v(7.7, -117.12) * mm, "end": v(7.88, -117.3) * mm});
            skArc(sketch, "E1556", {"start": v(9.2, -116.94) * mm, "mid": v(8.64, -117.5) * mm, "end": v(7.88, -117.3) * mm});
            skLineSegment(sketch, "E1557", {"start": v(10, -118.65) * mm, "end": v(7.62, -118.65) * mm});
            skArc(sketch, "E1558", {"start": v(7.26, -118.8) * mm, "mid": v(7.42, -118.7) * mm, "end": v(7.62, -118.65) * mm});
            skLineSegment(sketch, "E1559", {"start": v(7.26, -118.8) * mm, "end": v(4.15, -121.9) * mm});
            skArc(sketch, "E1560", {"start": v(4, -122.27) * mm, "mid": v(4.04, -122.07) * mm, "end": v(4.15, -121.9) * mm});
            skLineSegment(sketch, "E1561", {"start": v(4, -122.27) * mm, "end": v(4, -123) * mm});
            skArc(sketch, "E1562", {"start": v(4.51, -123.5) * mm, "mid": v(4.15, -123.35) * mm, "end": v(4, -123) * mm});
            skLineSegment(sketch, "E1563", {"start": v(4.51, -123.5) * mm, "end": v(6.86, -123.5) * mm});
            skArc(sketch, "E1564", {"start": v(6.86, -123.5) * mm, "mid": v(7.22, -123.65) * mm, "end": v(7.37, -124) * mm});
            skLineSegment(sketch, "E1565", {"start": v(7.37, -124.5) * mm, "end": v(7.37, -124) * mm});
            skArc(sketch, "E1566", {"start": v(7.37, -124.5) * mm, "mid": v(7.22, -124.85) * mm, "end": v(6.86, -125) * mm});
            skArc(sketch, "E1567", {"start": v(6.86, -105) * mm, "mid": v(7.22, -105.15) * mm, "end": v(7.37, -105.5) * mm});
            skLineSegment(sketch, "E1568", {"start": v(7.37, -106) * mm, "end": v(7.37, -105.5) * mm});
            skArc(sketch, "E1569", {"start": v(7.37, -106) * mm, "mid": v(7.22, -106.35) * mm, "end": v(6.86, -106.5) * mm});
            skLineSegment(sketch, "E1570", {"start": v(4.51, -106.5) * mm, "end": v(6.86, -106.5) * mm});
            skArc(sketch, "E1571", {"start": v(4, -107) * mm, "mid": v(4.15, -106.65) * mm, "end": v(4.51, -106.5) * mm});
            skLineSegment(sketch, "E1572", {"start": v(4, -107) * mm, "end": v(4, -107.73) * mm});
            skArc(sketch, "E1573", {"start": v(4.15, -108.1) * mm, "mid": v(4.04, -107.93) * mm, "end": v(4, -107.73) * mm});
            skLineSegment(sketch, "E1574", {"start": v(7.26, -111.2) * mm, "end": v(4.15, -108.1) * mm});
            skArc(sketch, "E1575", {"start": v(7.62, -111.35) * mm, "mid": v(7.42, -111.3) * mm, "end": v(7.26, -111.2) * mm});
            skLineSegment(sketch, "E1576", {"start": v(10, -111.35) * mm, "end": v(7.62, -111.35) * mm});
            skArc(sketch, "E1577", {"start": v(6.35, -112.62) * mm, "mid": v(6.3, -112.42) * mm, "end": v(6.2, -112.26) * mm});
            skLineSegment(sketch, "E1578", {"start": v(6.2, -112.26) * mm, "end": v(2.65, -108.71) * mm});
            skArc(sketch, "E1579", {"start": v(2.65, -108.71) * mm, "mid": v(2.54, -108.55) * mm, "end": v(2.5, -108.36) * mm});
            skLineSegment(sketch, "E1580", {"start": v(2.5, -107) * mm, "end": v(2.5, -108.36) * mm});
            skArc(sketch, "E1581", {"start": v(2, -106.5) * mm, "mid": v(2.36, -106.65) * mm, "end": v(2.5, -107) * mm});
            skArc(sketch, "E1582", {"start": v(2.5, -123) * mm, "mid": v(2.36, -123.35) * mm, "end": v(2, -123.5) * mm});
            skLineSegment(sketch, "E1583", {"start": v(2.5, -121.64) * mm, "end": v(2.5, -123) * mm});
            skArc(sketch, "E1584", {"start": v(2.5, -121.64) * mm, "mid": v(2.54, -121.45) * mm, "end": v(2.65, -121.29) * mm});
            skLineSegment(sketch, "E1585", {"start": v(6.2, -117.74) * mm, "end": v(2.65, -121.29) * mm});
            skArc(sketch, "E1586", {"start": v(6.35, -117.38) * mm, "mid": v(6.3, -117.58) * mm, "end": v(6.2, -117.74) * mm});
            skArc(sketch, "E1587", {"start": v(9.2, -113.06) * mm, "mid": v(9.6, -112.94) * mm, "end": v(10, -112.9) * mm});
            skArc(sketch, "E1588", {"start": v(10, -117.1) * mm, "mid": v(9.6, -117.06) * mm, "end": v(9.2, -116.94) * mm});
            skCircle(sketch, "E1589", {"center": v(42.45, -115) * mm, "radius": 4 * mm});
            skSolve(sketch);
        }
        {
            var Q0;
            Q0 = qSketchRegion(id + "F8", true);
            extrude(context, id + "F9", {"entities" : qUnion([Q0]), "depth" : 1000 * mm, "offsetDistance" : 25 * mm});
        }
    });
